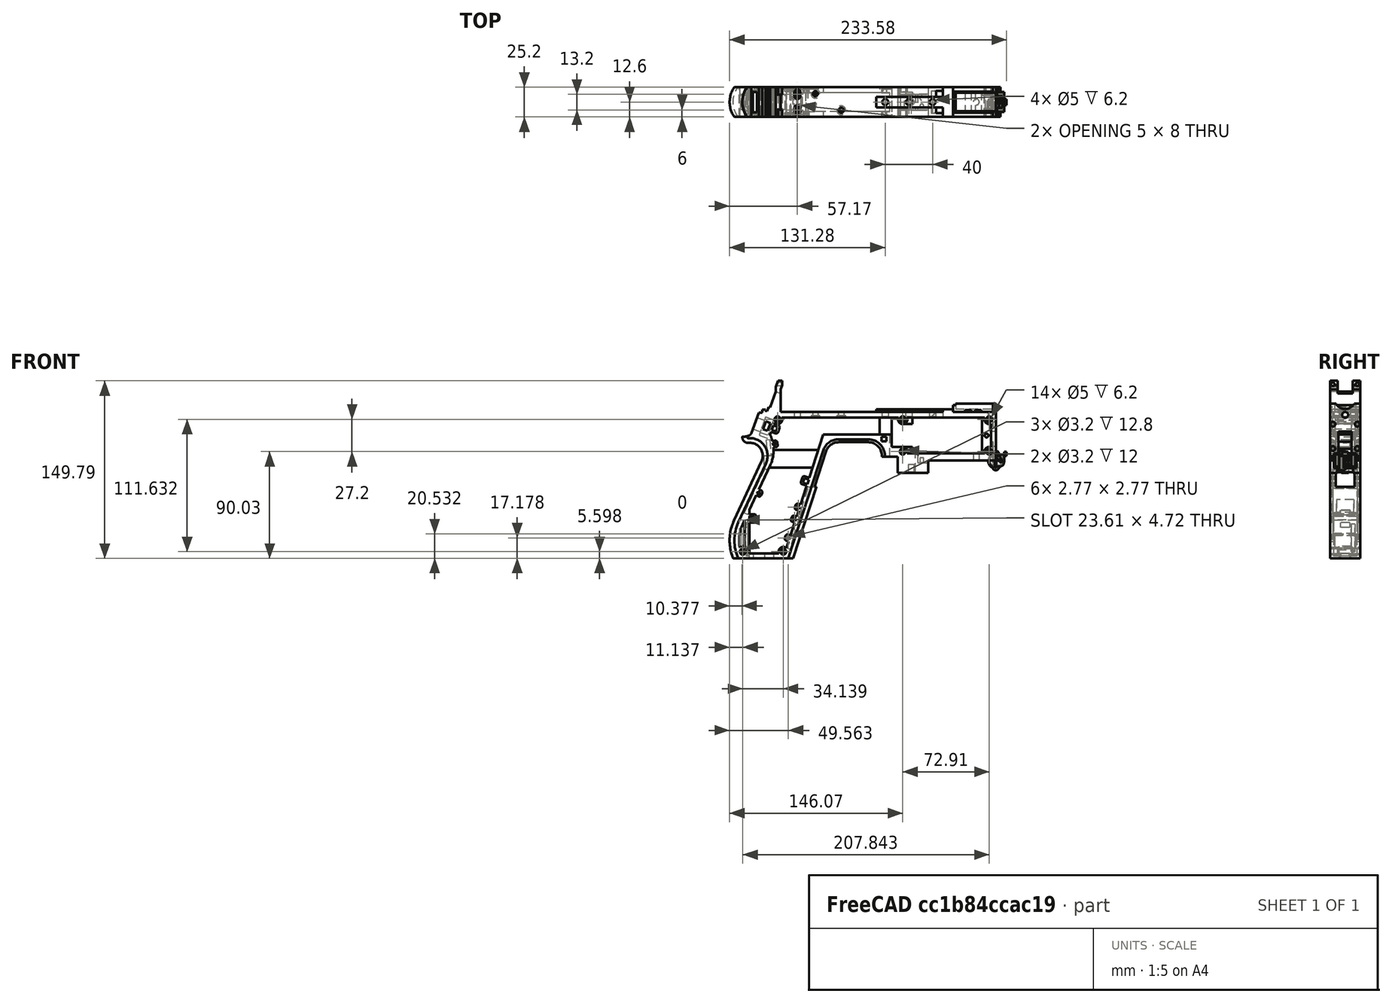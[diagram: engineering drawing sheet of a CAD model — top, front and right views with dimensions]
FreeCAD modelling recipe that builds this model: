
FCSTD DOCUMENT  (FreeCAD 1.0R39319 (Git))
Label: PICON-OF_ver_44
License: All rights reserved
LicenseURL: https://en.wikipedia.org/wiki/All_rights_reserved
objects: Sketcher::SketchObject×114, Part::Extrusion×57, Part::Cut×43, PartDesign::Pad×29, PartDesign::Pocket×18, PartDesign::Chamfer×15, PartDesign::Body×10, PartDesign::Fillet×6, Part::MultiFuse×4, PartDesign::SubtractivePipe×4, Part::Part2DObjectPython×4, PartDesign::SubtractiveLoft×4, PartDesign::Plane×2, PartDesign::SubShapeBinder×2, Part::Sweep×1, PartDesign::ShapeBinder×1, Mesh::Feature×1
note: 580 computed .brp shape members not serialized (recipe doc carries the construction recipe); baked Part::Feature solids carry a one-line shape summary decoded from their .brp

FEATURE [Sketcher::SketchObject] Sketch  label="corpo principale"
  ArcFitTolerance = 1e-06
  AttacherType = Attacher::AttachEngine3D
  AttachmentSupport = -> [XZ_Plane]
  FullyConstrained = true
  MakeInternals = false
  MapMode = 5
  Placement = pos=(0,0,0) rot=(1,0,0;1.5708rad)
  sketch-geometry (65):
    g0: LineSegment StartX=0 StartY=0 StartZ=0 EndX=-57.2 EndY=0 EndZ=0
    g1: LineSegment StartX=-57.2 StartY=0 StartZ=0 EndX=-57.2 EndY=-10.4 EndZ=0
    g2: LineSegment StartX=-57.2 StartY=-10.4 StartZ=0 EndX=-82.8 EndY=-10.4 EndZ=0
    g3: LineSegment StartX=-82.8 StartY=-10.4 StartZ=0 EndX=-82.8 EndY=3.2 EndZ=0
    g4: LineSegment StartX=-82.8 StartY=3.2 StartZ=0 EndX=-93.6 EndY=3.2 EndZ=0
    g5: LineSegment StartX=-93.6 StartY=3.2 StartZ=0 EndX=-93.6 EndY=4 EndZ=0
    g6: LineSegment StartX=-107.6 StartY=18 StartZ=0 EndX=-132.428 EndY=18 EndZ=0
    g7: LineSegment StartX=-145.743 StartY=8.32624 StartZ=0 EndX=-175.232 EndY=-82.4316 EndZ=0
    g8: LineSegment StartX=-175.232 StartY=-82.4316 StartZ=0 EndX=-217.232 EndY=-82.4316 EndZ=0
    g9: LineSegment StartX=-217.232 StartY=-52.1862 StartZ=0 EndX=-193.988 EndY=-2.33927 EndZ=0
    g10: LineSegment StartX=-206.196 StartY=23.0857 StartZ=0 EndX=-199.861 EndY=40.4914 EndZ=0
    g11: LineSegment StartX=-199.861 StartY=40.4914 StartZ=0 EndX=-197.061 EndY=40.4914 EndZ=0
    g12: LineSegment StartX=-197.061 StartY=40.4914 StartZ=0 EndX=-197.061 EndY=42.8914 EndZ=0
    g13: LineSegment StartX=-197.061 StartY=42.8914 StartZ=0 EndX=-194.261 EndY=42.8914 EndZ=0
    g14: LineSegment StartX=-194.261 StartY=42.8914 StartZ=0 EndX=-194.535 EndY=42.1397 EndZ=0
    g15: LineSegment StartX=-194.535 StartY=42.1397 StartZ=0 EndX=-193.031 EndY=41.5924 EndZ=0
    g16: LineSegment StartX=-193.031 StartY=41.5924 StartZ=0 EndX=-191.663 EndY=45.3512 EndZ=0
    g17: LineSegment StartX=-191.663 StartY=45.3512 StartZ=0 EndX=-190.536 EndY=44.9408 EndZ=0
    g18: LineSegment StartX=-190.536 StartY=44.9408 StartZ=0 EndX=-185.747 EndY=58.0965 EndZ=0
    g19: LineSegment StartX=-185.747 StartY=58.0965 StartZ=0 EndX=-185.747 EndY=62.0965 EndZ=0
    g20: LineSegment StartX=-185.747 StartY=62.0965 StartZ=0 EndX=-183.832 EndY=67.3588 EndZ=0
    g21: LineSegment StartX=-183.832 StartY=67.3588 StartZ=0 EndX=-180.232 EndY=67.3588 EndZ=0
    g22: LineSegment StartX=-180.232 StartY=67.3588 StartZ=0 EndX=-180.232 EndY=63.7588 EndZ=0
    g23: LineSegment StartX=-180.232 StartY=63.7588 StartZ=0 EndX=-181.6 EndY=60 EndZ=0
    g24: LineSegment StartX=-181.6 StartY=60 StartZ=0 EndX=-181.6 EndY=41.2 EndZ=0
    g25: LineSegment StartX=-181.6 StartY=41.2 StartZ=0 EndX=-100.8 EndY=41.2 EndZ=0
    g26: LineSegment StartX=-36 StartY=43.2 StartZ=0 EndX=-36 EndY=41.2 EndZ=0
    g27: LineSegment StartX=0 StartY=48 StartZ=0 EndX=0 EndY=0 EndZ=0
    g28: LineSegment StartX=-209.901 StartY=19.85 StartZ=0 EndX=-209.901 EndY=20.1 EndZ=0
    g29: LineSegment StartX=-208.001 StartY=22 StartZ=0 EndX=-207.747 EndY=22 EndZ=0
    g30: LineSegment StartX=-207.583 StartY=19 StartZ=0 EndX=-209.051 EndY=19 EndZ=0
    g31: ArcOfCircle CenterX=-208.001 CenterY=20.1 CenterZ=0 NormalX=0 NormalY=0 NormalZ=1 AngleXU=0 Radius=1.9 StartAngle=1.5708 EndAngle=3.14159
    g32: GeomPoint [constr] X=-209.901 Y=22 Z=0
    g33: ArcOfCircle CenterX=-209.051 CenterY=19.85 CenterZ=0 NormalX=0 NormalY=0 NormalZ=1 AngleXU=0 Radius=0.85 StartAngle=3.14159 EndAngle=4.71239
    g34: GeomPoint [constr] X=-209.901 Y=19 Z=0
    g35: ArcOfCircle CenterX=-207.747 CenterY=23.65 CenterZ=0 NormalX=0 NormalY=0 NormalZ=1 AngleXU=0 Radius=1.65 StartAngle=4.71239 EndAngle=5.93412
    g36: GeomPoint [constr] X=-206.591 Y=22 Z=0
    g37: LineSegment StartX=-4 StartY=6 StartZ=0 EndX=-4 EndY=36.4 EndZ=0
    g38: LineSegment StartX=-4 StartY=36.4 StartZ=0 EndX=-185.2 EndY=36.4 EndZ=0
    g39: LineSegment StartX=-185.2 StartY=36.4 StartZ=0 EndX=-190.441 EndY=22 EndZ=0
    g40: LineSegment StartX=-214.575 StartY=-78.4316 StartZ=0 EndX=-178.142 EndY=-78.4316 EndZ=0
    g41: LineSegment StartX=-178.142 StartY=-78.4316 StartZ=0 EndX=-145.51 EndY=22 EndZ=0
    g42: LineSegment StartX=-145.51 StartY=22 StartZ=0 EndX=-87.91 EndY=22 EndZ=0
    g43: LineSegment StartX=-87.91 StartY=22 StartZ=0 EndX=-87.91 EndY=11.6 EndZ=0
    g44: LineSegment StartX=-87.91 StartY=11.6 StartZ=0 EndX=-80.11 EndY=11.6 EndZ=0
    g45: LineSegment StartX=-80.11 StartY=11.6 StartZ=0 EndX=-80.11 EndY=6 EndZ=0
    g46: LineSegment StartX=-80.11 StartY=6 StartZ=0 EndX=-4 EndY=6 EndZ=0
    g47: LineSegment StartX=-190.363 StartY=-4.02975 StartZ=0 EndX=-213.607 EndY=-53.8767 EndZ=0
    g48: ArcOfCircle CenterX=-132.428 CenterY=4 CenterZ=0 NormalX=0 NormalY=0 NormalZ=1 AngleXU=0 Radius=14 StartAngle=1.5708 EndAngle=2.82743
    g49: GeomPoint [constr] X=-142.6 Y=18 Z=0
    g50: ArcOfCircle CenterX=-107.6 CenterY=4 CenterZ=0 NormalX=0 NormalY=0 NormalZ=1 AngleXU=0 Radius=14 StartAngle=0 EndAngle=1.5708
    g51: GeomPoint [constr] X=-93.6 Y=18 Z=0
    g52: ArcOfCircle CenterX=-184.801 CenterY=-67.3089 CenterZ=0 NormalX=0 NormalY=0 NormalZ=1 AngleXU=0 Radius=35.7833 StartAngle=2.70526 EndAngle=3.57792
    g53: ArcOfCircle CenterX=-207.583 CenterY=4 CenterZ=0 NormalX=0 NormalY=0 NormalZ=1 AngleXU=0 Radius=15 StartAngle=5.84685 EndAngle=7.85398
    g54: LineSegment [constr] StartX=-213.607 StartY=-53.8767 StartZ=0 EndX=-217.232 EndY=-52.1862 EndZ=0
    g55: ArcOfCircle CenterX=-184.801 CenterY=-67.3089 CenterZ=0 NormalX=0 NormalY=0 NormalZ=1 AngleXU=0 Radius=31.7833 StartAngle=2.70526 EndAngle=3.49911
    g56: ArcOfCircle CenterX=-218.095 CenterY=8.90192 CenterZ=0 NormalX=0 NormalY=0 NormalZ=1 AngleXU=0 Radius=30.5989 StartAngle=5.84685 EndAngle=6.72553
    g57: LineSegment StartX=-44.6 StartY=43.2 StartZ=0 EndX=-36 EndY=43.2 EndZ=0
    g58: LineSegment StartX=-100.8 StartY=41.2 StartZ=0 EndX=-44.6 EndY=41.2 EndZ=0
    g59: LineSegment StartX=-44.6 StartY=41.2 StartZ=0 EndX=-44.6 EndY=43.2 EndZ=0
    g60: LineSegment StartX=-2.4 StartY=48 StartZ=0 EndX=0 EndY=48 EndZ=0
    g61: LineSegment StartX=-36 StartY=41.2 StartZ=0 EndX=-2.4 EndY=41.2 EndZ=0
    g62: LineSegment StartX=-2.4 StartY=41.2 StartZ=0 EndX=-2.4 EndY=48 EndZ=0
    g63: LineSegment [constr] StartX=-181.6 StartY=36.4 StartZ=0 EndX=-152.209 EndY=36.4 EndZ=0
    g64: LineSegment [constr] StartX=-181.6 StartY=36.4 StartZ=0 EndX=-130.41 EndY=36.4 EndZ=0
  constraints (183):
    c: Coincident(g-1,g0)
    c: PointOnObject(g0,g-1)
    c: Coincident(g0,g1)
    c: Vertical(g1)
    c: Coincident(g1,g2)
    c: Horizontal(g2)
    c: Coincident(g2,g3)
    c: Vertical(g3)
    c: Coincident(g3,g4)
    c: Coincident(g4,g5)
    c: Vertical(g5)
    c: Horizontal(g6)
    c: Coincident(g7,g8)
    c: Horizontal(g8)
    c: Coincident(g10,g11)
    c: Horizontal(g11)
    c: Coincident(g11,g12)
    c: Vertical(g12)
    c: Coincident(g12,g13)
    c: Horizontal(g13)
    c: Coincident(g13,g14)
    c: Coincident(g14,g15)
    c: Coincident(g15,g16)
    c: Coincident(g16,g17)
    c: Coincident(g17,g18)
    c: Coincident(g18,g19)
    c: Vertical(g19)
    c: Coincident(g19,g20)
    c: Coincident(g20,g21)
    c: Horizontal(g21)
    c: Coincident(g21,g22)
    c: Vertical(g22)
    c: Coincident(g22,g23)
    c: Coincident(g23,g24)
    c: Vertical(g24)
    c: Coincident(g24,g25)
    c: Horizontal(g25)
    c: Coincident(g57,g26)
    c: Vertical(g26)
    c: Coincident(g26,g61)
    c: PointOnObject(g60,g-2)
    c: Coincident(g60,g27)
    c: Coincident(g27,g0)
    c: DistanceY(g27,g27) = 48
    c: DistanceY(g1,g1) = 10.4
    c: DistanceX(g0,g0) = 57.2
    c: DistanceX(g2,g2) = 25.6
    c: Horizontal(g4)
    c: DistanceY(g3,g3) = 13.6
    c: DistanceX(g4,g4) = 10.8
    c: DistanceY(g5,g51) = 14.8
    c: DistanceX(g49,g51) = 49
    c: Distance(g7,g49) = 105.6
    c: DistanceX(g61,g60) = 36
    c: DistanceX(g25,g25) = 80.8
    c: DistanceY(g24,g24) = 18.8
    c: DistanceY(g22,g22) = 3.6
    c: Distance(g23) = 4
    c: Angle(g-1,g23) = 1.22173
    c: DistanceX(g21,g21) = 3.6
    c: Distance(g20) = 5.6
    c: Angle(g-1,g20) = 1.22173
    c: DistanceY(g19,g19) = 4
    c: Distance(g18) = 14
    c: Angle(g-1,g18) = 1.22173
    c: Distance(g17) = 1.2
    c: Distance(g16) = 4
    c: Angle(g16) = 1.22173
    c: Perpendicular(g18,g17)
    c: Distance(g15) = 1.6
    c: Perpendicular(g16,g15)
    c: Distance(g14) = 0.8
    c: DistanceX(g13,g13) = 2.8
    c: Perpendicular(g15,g14)
    c: DistanceY(g12,g12) = 2.4
    c: DistanceX(g11,g11) = 2.8
    c: Distance(g9) = 55
    c: Angle(g9,g-1) = 2.00713
    c: Horizontal(g29)
    c: Vertical(g28)
    c: Horizontal(g30)
    c: PointOnObject(g32,g29)
    c: PointOnObject(g32,g28)
    c: Tangent(g29,g31) = 1.5708
    c: Tangent(g28,g31) = 1.5708
    c: PointOnObject(g34,g28)
    c: PointOnObject(g34,g30)
    c: Tangent(g28,g33) = 1.5708
    c: Tangent(g30,g33) = 1.5708
    c: PointOnObject(g36,g29)
    c: PointOnObject(g36,g10)
    c: Tangent(g29,g35) = -1.5708
    c: Tangent(g10,g35) = -1.5708
    c: Angle(g-1,g10) = 1.22173
    c: Radius(g35) = 1.65
    c: Vertical(g37)
    c: Coincident(g37,g38)
    c: Horizontal(g38)
    c: Coincident(g38,g39)
    c: Horizontal(g40)
    c: Coincident(g40,g41)
    c: Coincident(g41,g42)
    c: Horizontal(g42)
    c: Coincident(g42,g43)
    c: Vertical(g43)
    c: Coincident(g43,g44)
    c: Horizontal(g44)
    c: Coincident(g44,g45)
    c: Vertical(g45)
    c: Coincident(g45,g46)
    c: Coincident(g46,g37)
    c: Horizontal(g46)
    c: DistanceY(g0,g37) = 6
    c: DistanceX(g37,g0) = 4
    c: DistanceY(g37,g25) = 4.8
    c: DistanceX(g38,g38) = 181.2
    c: DistanceX(g42,g42) = 57.6
    c: DistanceY(g49,g41) = 4
    c: DistanceX(g41,g49) = 2.91
    c: DistanceY(g43,g43) = 10.4
    c: DistanceX(g44,g44) = 7.8
    c: DistanceY(g7,g40) = 4
    c: Distance(g47) = 55
    c: Angle(g-1,g39) = 1.22173
    c: PointOnObject(g49,g7)
    c: PointOnObject(g49,g6)
    c: Tangent(g7,g48) = -1.5708
    c: Tangent(g6,g48) = -1.5708
    c: PointOnObject(g51,g5)
    c: PointOnObject(g51,g6)
    c: Tangent(g5,g50) = -1.5708
    c: Tangent(g6,g50) = -1.5708
    c: Radius(g50) = 14
    c: Radius(g48) = 14
    c: DistanceX(g8,g8) = 42
    c: Angle(g7,g-1) = 1.88496
    c: Parallel(g41,g7)
    c: Parallel(g47,g9)
    c: Coincident(g52,g8)
    c: Tangent(g52,g9) = 1.5708
    c: DistanceX(g9,g8) = 0
    c: Tangent(g53,g9) = -1.5708
    c: Tangent(g53,g30) = -1.5708
    c: Diameter(g53) = 30
    c: DistanceY(g53,g0) = -4
    c: Coincident(g54,g47)
    c: Distance(g54) = 4
    c: Coincident(g54,g9)
    c: Coincident(g55,g40)
    c: Tangent(g55,g47) = -1.5708
    c: Coincident(g52,g55)
    c: Coincident(g56,g39)
    c: Tangent(g56,g47) = 1.5708
    c: Horizontal(g57)
    c: DistanceX(g57,g57) = 8.6
    c: Coincident(g58,g25)
    c: Horizontal(g58)
    c: Coincident(g59,g58)
    c: Vertical(g59)
    c: DistanceY(g58,g57) = 2
    c: DistanceX(g58,g58) = 56.2
    c: Coincident(g59,g57)
    c: DistanceY(g41,g36) = 0
    c: DistanceY(g36,g39) = 0
    c: DistanceY(g28,g28) = 0.25
    c: DistanceX(g30,g36) = 2.46
    c: DistanceX(g28,g29) = 1.9
    c: Coincident(g62,g60)
    c: Horizontal(g60)
    c: DistanceX(g62,g27) = 2.4
    c: Coincident(g61,g62)
    c: DistanceY(g26,g26) = 2
    c: Vertical(g62)
    c: DistanceY(g61,g60) = 6.8
    c: Horizontal(g61)
    c: Distance(g63) = 29.391
    c: PointOnObject(g63,g38)
    c: PointOnObject(g63,g38)
    c: Distance(g64) = 51.19
    c: PointOnObject(g64,g38)
    c: PointOnObject(g64,g38)
    c: DistanceX(g24,g63) = 0
    c: DistanceX(g24,g64) = 0
FEATURE [Part::Extrusion] Extrude  label="Extrude corpo principale"
  Base = -> Sketch
  Dir = (0,-1,2e-16)
  DirMode = 2
  FaceMakerClass = Part::FaceMakerBullseye
  FaceMakerMode = 3
  LengthFwd = 25.2
  LengthRev = 12.6
  Solid = true
  Symmetric = true
FEATURE [Sketcher::SketchObject] Sketch002  label="scavo grilletto"
  ArcFitTolerance = 1e-06
  AttachmentSupport = -> [XZ_Plane]
  ExternalGeometry = -> [Sketch]
  FullyConstrained = true
  MakeInternals = false
  MapMode = 5
  Placement = pos=(0,0,0) rot=(1,0,0;1.5708rad)
  sketch-geometry (4):
    g0: LineSegment StartX=-89.51 StartY=22 StartZ=0 EndX=-152.71 EndY=22 EndZ=0
    g1: LineSegment StartX=-152.71 StartY=22 StartZ=0 EndX=-167.006 EndY=-22 EndZ=0
    g2: LineSegment StartX=-167.006 StartY=-22 StartZ=0 EndX=-89.51 EndY=-22 EndZ=0
    g3: LineSegment StartX=-89.51 StartY=-22 StartZ=0 EndX=-89.51 EndY=22 EndZ=0
  constraints (12):
    c: Horizontal(g0)
    c: Coincident(g0,g1)
    c: Coincident(g1,g2)
    c: Horizontal(g2)
    c: Coincident(g2,g3)
    c: Coincident(g3,g0)
    c: Vertical(g3)
    c: Angle(g1,g0) = 1.88496
    c: DistanceY(g3,g3) = 44
    c: DistanceX(g0,g0) = 63.2
    c: DistanceX(g0,g-3) = 1.6
    c: DistanceY(g-3,g0) = 0
FEATURE [Sketcher::SketchObject] Sketch004  label="traiettoria arrotondamento impugnatura anteriore"
  ArcFitTolerance = 1e-06
  AttachmentSupport = -> [XZ_Plane]
  ExternalGeometry = -> [Sketch]
  FullyConstrained = true
  MakeInternals = false
  MapMode = 5
  Placement = pos=(0,0,0) rot=(1,0,0;1.5708rad)
  sketch-geometry (13):
    g0: LineSegment StartX=-175.232 StartY=-82.4316 StartZ=0 EndX=-145.743 EndY=8.32624 EndZ=0
    g1: LineSegment StartX=-93.6 StartY=3.2 StartZ=0 EndX=-93.6 EndY=4 EndZ=0
    g2: LineSegment StartX=-132.428 StartY=18 StartZ=0 EndX=-107.6 EndY=18 EndZ=0
    g3: ArcOfCircle CenterX=-132.428 CenterY=4 CenterZ=0 NormalX=0 NormalY=0 NormalZ=1 AngleXU=0 Radius=14 StartAngle=1.5708 EndAngle=2.82743
    g4: ArcOfCircle CenterX=-107.6 CenterY=4 CenterZ=0 NormalX=0 NormalY=0 NormalZ=1 AngleXU=0 Radius=14 StartAngle=0 EndAngle=1.5708
    g5: LineSegment StartX=-175.232 StartY=-82.4316 StartZ=0 EndX=-217.232 EndY=-82.4316 EndZ=0
    g6: LineSegment StartX=-217.232 StartY=-52.1862 StartZ=0 EndX=-193.988 EndY=-2.33927 EndZ=0
    g7: LineSegment StartX=-209.051 StartY=19 StartZ=0 EndX=-207.583 EndY=19 EndZ=0
    g8: LineSegment StartX=-209.901 StartY=20.1 StartZ=0 EndX=-209.901 EndY=19.85 EndZ=0
    g9: ArcOfCircle CenterX=-184.801 CenterY=-67.3089 CenterZ=0 NormalX=0 NormalY=0 NormalZ=1 AngleXU=0 Radius=35.7833 StartAngle=2.70526 EndAngle=3.57792
    g10: ArcOfCircle CenterX=-207.583 CenterY=4 CenterZ=0 NormalX=0 NormalY=0 NormalZ=1 AngleXU=0 Radius=15 StartAngle=5.84685 EndAngle=7.85398
    g11: ArcOfCircle CenterX=-209.051 CenterY=19.85 CenterZ=0 NormalX=0 NormalY=0 NormalZ=1 AngleXU=0 Radius=0.85 StartAngle=3.14159 EndAngle=4.71239
    g12: ArcOfCircle CenterX=-208.001 CenterY=20.1 CenterZ=0 NormalX=0 NormalY=0 NormalZ=1 AngleXU=0 Radius=1.9 StartAngle=1.5708 EndAngle=3.14159
  constraints (26):
    c: Coincident(g0,g-3)
    c: Coincident(g0,g-6)
    c: Coincident(g1,g-8)
    c: Coincident(g1,g-7)
    c: Coincident(g2,g-5)
    c: Coincident(g2,g-4)
    c: Coincident(g3,g2)
    c: Tangent(g3,g0) = 1.5708
    c: Coincident(g4,g1)
    c: Tangent(g4,g2) = 1.5708
    c: Coincident(g5,g0)
    c: Coincident(g5,g-9)
    c: Coincident(g6,g-12)
    c: Coincident(g6,g-11)
    c: Coincident(g7,g-15)
    c: Coincident(g7,g-14)
    c: Coincident(g8,g-16)
    c: Coincident(g8,g-17)
    c: Tangent(g9,g6) = 1.5708
    c: Coincident(g9,g5)
    c: Coincident(g10,g7)
    c: Tangent(g10,g6) = -1.5708
    c: Tangent(g11,g7) = -1.5708
    c: Coincident(g11,g8)
    c: Tangent(g12,g8) = -1.5708
    c: Coincident(g12,g-17)
FEATURE [PartDesign::Plane] DatumPlane  label="Piano per disegno arrotondamento impugnatura"
  AttachmentSupport = -> [Sketch]
  Length = 73.6581
  MapMode = 7
  Placement = pos=(-145.743,1.8e-15,8.32624) rot=(0.154555,0.154555,0.97582;1.59527rad)
  ResizeMode = 0
  Width = 303.511
FEATURE [Sketcher::SketchObject] Sketch005  label="forma arrotondamento impugnatura anteriore"
  ArcFitTolerance = 1e-06
  AttachmentSupport = -> [DatumPlane]
  FullyConstrained = true
  MakeInternals = false
  MapMode = 5
  Placement = pos=(-145.743,1.8e-15,8.32624) rot=(0.154555,0.154555,0.97582;1.59527rad)
  sketch-geometry (5):
    g0: GeomPoint [constr] X=0 Y=-4 Z=0
    g1: GeomPoint [constr] X=-12.6 Y=7.1e-15 Z=0
    g2: GeomPoint [constr] X=12.6 Y=4.97e-14 Z=0
    g3: LineSegment StartX=-12.6 StartY=7.1e-15 StartZ=0 EndX=12.6 EndY=4.97e-14 EndZ=0
    g4: ArcOfCircle CenterX=-3.88e-14 CenterY=17.845 CenterZ=0 NormalX=0 NormalY=0 NormalZ=1 AngleXU=0 Radius=21.845 StartAngle=4.09759 EndAngle=5.32718
  constraints (11):
    c: DistanceY(g0,g-1) = 4
    c: DistanceX(g-1,g0) = 0
    c: DistanceX(g1,g-1) = 12.6
    c: DistanceX(g-1,g2) = 12.6
    c: DistanceY(g-1,g2) = 0
    c: DistanceY(g-1,g1) = 0
    c: Coincident(g3,g1)
    c: Coincident(g3,g2)
    c: Coincident(g4,g1)
    c: Coincident(g4,g2)
    c: PointOnObject(g0,g4)
FEATURE [Part::Sweep] Sweep  label="Sweep impugnatura"
  Frenet = true
  Sections = -> [Sketch005]
  Solid = true
  Spine = -> Sketch [Edge32,Edge33,Edge34,Edge35,Edge36,Edge37,Edge38,Edge39,Edge40,Edge41,Edge42,Edge43,Edge44]
  Transition = 1
FEATURE [Sketcher::SketchObject] Sketch008  label="buchi e pulizie varie"
  ArcFitTolerance = 1e-06
  AttachmentSupport = -> [XZ_Plane]
  ExternalGeometry = -> [Sketch]
  FullyConstrained = true
  MakeInternals = false
  MapMode = 5
  Placement = pos=(0,0,0) rot=(1,0,0;1.5708rad)
  sketch-geometry (26):
    g0: LineSegment StartX=-96.278 StartY=20.155 StartZ=0 EndX=-92.278 EndY=20.155 EndZ=0
    g1: LineSegment StartX=-92.278 StartY=20.155 StartZ=0 EndX=-92.278 EndY=16.155 EndZ=0
    g2: LineSegment StartX=-92.278 StartY=16.155 StartZ=0 EndX=-96.278 EndY=16.155 EndZ=0
    g3: LineSegment StartX=-96.278 StartY=16.155 StartZ=0 EndX=-96.278 EndY=20.155 EndZ=0
    g4: LineSegment StartX=-222.232 StartY=-82.4316 StartZ=0 EndX=-170.232 EndY=-82.4316 EndZ=0
    g5: LineSegment StartX=-170.232 StartY=-82.4316 StartZ=0 EndX=-170.232 EndY=-86.4316 EndZ=0
    g6: LineSegment StartX=-170.232 StartY=-86.4316 StartZ=0 EndX=-222.232 EndY=-86.4316 EndZ=0
    g7: LineSegment StartX=-222.232 StartY=-86.4316 StartZ=0 EndX=-222.232 EndY=-82.4316 EndZ=0
    g8: LineSegment StartX=-213.901 StartY=20.1 StartZ=0 EndX=-213.901 EndY=26 EndZ=0
    g9: LineSegment StartX=-213.901 StartY=26 StartZ=0 EndX=-206.196 EndY=26 EndZ=0
    g10: LineSegment StartX=-17.4 StartY=42.8 StartZ=0 EndX=-12.4 EndY=42.8 EndZ=0
    g11: LineSegment StartX=-12.4 StartY=42.8 StartZ=0 EndX=-12.4 EndY=41.2 EndZ=0
    g12: LineSegment StartX=-12.4 StartY=41.2 StartZ=0 EndX=-17.4 EndY=41.2 EndZ=0
    g13: LineSegment StartX=-17.4 StartY=41.2 StartZ=0 EndX=-17.4 EndY=42.8 EndZ=0
    g14: LineSegment StartX=-25.9 StartY=42.8 StartZ=0 EndX=-20.9 EndY=42.8 EndZ=0
    g15: LineSegment StartX=-20.9 StartY=42.8 StartZ=0 EndX=-20.9 EndY=41.2 EndZ=0
    g16: LineSegment StartX=-20.9 StartY=41.2 StartZ=0 EndX=-25.9 EndY=41.2 EndZ=0
    g17: LineSegment StartX=-25.9 StartY=41.2 StartZ=0 EndX=-25.9 EndY=42.8 EndZ=0
    g18: GeomPoint [constr] X=-206.196 Y=23.0857 Z=0
    g19: GeomPoint [constr] X=-213.901 Y=20.1 Z=0
    g20: BSplineCurve PolesCount=4 KnotsCount=2 Degree=3 IsPeriodic=0
    g21-g24: Circle [constr] x4 (B-spline internal-alignment scaffolding for g20; pole/knot coordinates omitted)
    g25: LineSegment StartX=-206.196 StartY=26 StartZ=0 EndX=-206.196 EndY=23.0857 EndZ=0
  constraints (73):
    c: Horizontal(g0)
    c: Coincident(g1,g0)
    c: Vertical(g1)
    c: Coincident(g2,g1)
    c: Horizontal(g2)
    c: Coincident(g3,g2)
    c: Coincident(g3,g0)
    c: Vertical(g3)
    c: DistanceX(g0,g-4) = 4.368
    c: DistanceY(g0,g-4) = 1.845
    c: DistanceY(g1,g1) = 4
    c: DistanceX(g2,g2) = 4
    c: Horizontal(g4)
    c: Coincident(g5,g4)
    c: Vertical(g5)
    c: Coincident(g6,g5)
    c: Horizontal(g6)
    c: Coincident(g7,g6)
    c: Coincident(g7,g4)
    c: Vertical(g7)
    c: DistanceY(g7,g7) = 4
    c: DistanceX(g4,g-5) = 5
    c: DistanceX(g-5,g4) = 5
    c: DistanceY(g4,g-5) = 0
    c: Coincident(g9,g8)
    c: Parallel(g9,g-6)
    c: DistanceX(g8,g-8) = 4
    c: Horizontal(g10)
    c: Coincident(g11,g10)
    c: Vertical(g11)
    c: Coincident(g12,g11)
    c: Horizontal(g12)
    c: Coincident(g13,g12)
    c: Coincident(g13,g10)
    c: Vertical(g13)
    c: Horizontal(g14)
    c: Coincident(g15,g14)
    c: Vertical(g15)
    c: Coincident(g16,g15)
    c: Horizontal(g16)
    c: Coincident(g17,g16)
    c: Coincident(g17,g14)
    c: Vertical(g17)
    c: DistanceY(g11,g10) = 1.6
    c: DistanceX(g10,g10) = 5
    c: DistanceY(g15,g14) = 1.6
    c: DistanceX(g14,g14) = 5
    c: DistanceX(g15,g12) = 3.5
    c: DistanceX(g11,g-9) = 10
    c: DistanceY(g-9,g11) = 0
    c: DistanceY(g-9,g15) = 0
    c: Perpendicular(g8,g9)
    c: DistanceY(g-7,g9) = 4
    c: DistanceY(g8,g-8) = 0
    c: InternalAlignment(g18,g20)
    c: InternalAlignment(g19,g20)
    c: InternalAlignment(g21,g20)
    c: Weight(g21) = 1
    c: InternalAlignment(g22,g20)
    c: Equal(g22,g21)
    c: InternalAlignment(g23,g20)
    c: Equal(g23,g21)
    c: InternalAlignment(g24,g20)
    c: Equal(g24,g21)
    c: Coincident(g18,g-12)
    c: Coincident(g19,g8)
    c: Coincident(g25,g9)
    c: Coincident(g25,g20)
    c: Vertical(g25)
    c: DistanceY(g20,g23) = 0
    c: DistanceY(g22,g18) = 2.26
    c: DistanceX(g22,g18) = 0.93
    c: DistanceX(g20,g23) = 2.9
FEATURE [Part::Extrusion] Extrude004  label="Extrude Buchi e pulizie varie"
  Base = -> Sketch008
  Dir = (0,-1,2e-16)
  DirMode = 2
  FaceMakerClass = Part::FaceMakerBullseye
  FaceMakerMode = 3
  LengthFwd = 25.2
  LengthRev = 0
  Solid = true
  Symmetric = true
FEATURE [Sketcher::SketchObject] Sketch009  label="rinforzi"
  ArcFitTolerance = 1e-06
  AttachmentSupport = -> [XZ_Plane]
  ExternalGeometry = -> [Sketch]
  FullyConstrained = true
  MakeInternals = false
  MapMode = 5
  Placement = pos=(0,0,0) rot=(1,0,0;1.5708rad)
  sketch-geometry (9):
    g0: LineSegment StartX=-87.91 StartY=22 StartZ=0 EndX=-87.91 EndY=36.4 EndZ=0
    g1: LineSegment StartX=-87.91 StartY=36.4 StartZ=0 EndX=-97.91 EndY=36.4 EndZ=0
    g2: LineSegment StartX=-97.91 StartY=36.4 StartZ=0 EndX=-97.91 EndY=22 EndZ=0
    g3: LineSegment StartX=-97.91 StartY=22 StartZ=0 EndX=-87.91 EndY=22 EndZ=0
    g4: LineSegment StartX=-149.713 StartY=9.06563 StartZ=0 EndX=-154.586 EndY=-5.93437 EndZ=0
    g5: LineSegment StartX=-154.586 StartY=-5.93437 StartZ=0 EndX=-191.863 EndY=-5.93437 EndZ=0
    g6: LineSegment StartX=-191.863 StartY=-5.93437 StartZ=0 EndX=-191.863 EndY=9.06563 EndZ=0
    g7: LineSegment StartX=-191.863 StartY=9.06563 StartZ=0 EndX=-149.713 EndY=9.06563 EndZ=0
    g8: LineSegment [constr] StartX=-145.51 StartY=22 StartZ=0 EndX=-149.713 EndY=9.06563 EndZ=0
  constraints (25):
    c: Vertical(g0)
    c: Coincident(g1,g0)
    c: Horizontal(g1)
    c: Coincident(g2,g1)
    c: Vertical(g2)
    c: Coincident(g3,g2)
    c: Coincident(g3,g0)
    c: Horizontal(g3)
    c: Coincident(g0,g-4)
    c: DistanceX(g3,g3) = 10
    c: DistanceY(g0,g-3) = 0
    c: Coincident(g5,g4)
    c: Horizontal(g5)
    c: Coincident(g6,g5)
    c: Vertical(g6)
    c: Coincident(g7,g6)
    c: Coincident(g7,g4)
    c: Horizontal(g7)
    c: Distance(g8) = 13.6
    c: Parallel(g-6,g8)
    c: Coincident(g-6,g8)
    c: Parallel(g4,g-6)
    c: DistanceY(g4,g4) = 15
    c: Coincident(g4,g8)
    c: DistanceX(g-5,g5) = -1.5
FEATURE [Part::Extrusion] Extrude001  label="Extrude scavo grilletto"
  Base = -> Sketch002
  Dir = (0,-1,2e-16)
  DirMode = 2
  FaceMakerClass = Part::FaceMakerBullseye
  FaceMakerMode = 3
  LengthFwd = 16
  LengthRev = 0
  Solid = true
  Symmetric = true
FEATURE [Part::Extrusion] Extrude005  label="Extrude Rinforzi"
  Base = -> Sketch009
  Dir = (0,-1,2e-16)
  DirMode = 2
  FaceMakerClass = Part::FaceMakerBullseye
  FaceMakerMode = 3
  LengthFwd = 2
  LengthRev = 0
  Placement = pos=(0,12.6,0) rot=(0,0,1;0rad)
  Solid = true
  Symmetric = false
FEATURE [PartDesign::ShapeBinder] CopyCut
  TraceSupport = false
FEATURE [PartDesign::Plane] DatumPlane001
  AttachmentSupport = -> [CopyCut]
  Length = 283.944
  MapMode = 5
  Placement = pos=(0,12.6,0) rot=(0,0.707107,0.707107;3.14159rad)
  ResizeMode = 0
  Width = 188.15
FEATURE [Sketcher::SketchObject] Sketch010  label="buco neopixel"
  ArcFitTolerance = 1e-06
  AttachmentSupport = -> [XZ_Plane]
  ExternalGeometry = -> [Sketch]
  FullyConstrained = true
  MakeInternals = false
  MapMode = 5
  Placement = pos=(0,0,0) rot=(1,0,0;1.5708rad)
  sketch-geometry (5):
    g0: LineSegment [constr] StartX=-199.861 StartY=40.4914 StartZ=0 EndX=-201.368 EndY=36.3521 EndZ=0
    g1: LineSegment StartX=-201.368 StartY=36.3521 StartZ=0 EndX=-204.932 EndY=26.5605 EndZ=0
    g2: LineSegment StartX=-201.368 StartY=36.3521 StartZ=0 EndX=-180.2 EndY=28.6477 EndZ=0
    g3: LineSegment StartX=-180.2 StartY=28.6477 StartZ=0 EndX=-183.764 EndY=18.8561 EndZ=0
    g4: LineSegment StartX=-183.764 StartY=18.8561 StartZ=0 EndX=-204.932 EndY=26.5605 EndZ=0
  constraints (14):
    c: Parallel(g0,g-3)
    c: Distance(g0) = 4.405
    c: Coincident(g0,g-3)
    c: Coincident(g2,g1)
    c: Coincident(g3,g2)
    c: Coincident(g4,g3)
    c: Coincident(g4,g1)
    c: Parallel(g1,g-3)
    c: Distance(g1) = 10.42
    c: Coincident(g1,g0)
    c: Parallel(g2,g4)
    c: Perpendicular(g1,g2)
    c: DistanceX(g-4,g2) = 5
    c: Parallel(g3,g1)
FEATURE [Part::Extrusion] Extrude006  label="Extrude buco neopixel"
  Base = -> Sketch010
  Dir = (0,-1,2e-16)
  DirMode = 2
  FaceMakerClass = Part::FaceMakerBullseye
  FaceMakerMode = 3
  LengthFwd = 17.2
  LengthRev = 0
  Solid = true
  Symmetric = true
FEATURE [Sketcher::SketchObject] Sketch011  label="fermo grilletto"
  ArcFitTolerance = 1e-06
  AttachmentSupport = -> [XZ_Plane]
  ExternalGeometry = -> [Sketch]
  FullyConstrained = true
  MakeInternals = false
  MapMode = 5
  Placement = pos=(0,0,0) rot=(1,0,0;1.5708rad)
  sketch-geometry (18):
    g0: LineSegment [constr] StartX=-145.51 StartY=22 StartZ=0 EndX=-157.347 EndY=-14.4293 EndZ=0
    g1: LineSegment [constr] StartX=-157.347 StartY=-14.4293 StartZ=0 EndX=-157.841 EndY=-15.951 EndZ=0
    g2: LineSegment StartX=-161.151 StartY=-13.1932 StartZ=0 EndX=-155.825 EndY=-14.9237 EndZ=0
    g3: LineSegment StartX=-163.167 StartY=-14.2205 StartZ=0 EndX=-164.403 EndY=-18.0247 EndZ=0
    g4: LineSegment StartX=-163.376 StartY=-20.0408 StartZ=0 EndX=-158.05 EndY=-21.7713 EndZ=0
    g5: LineSegment StartX=-158.05 StartY=-21.7713 StartZ=0 EndX=-155.825 EndY=-14.9237 EndZ=0
    g6: LineSegment StartX=-161.645 StartY=-14.7149 StartZ=0 EndX=-157.841 EndY=-15.951 EndZ=0
    g7: LineSegment StartX=-157.841 StartY=-15.951 StartZ=0 EndX=-159.077 EndY=-19.7552 EndZ=0
    g8: LineSegment StartX=-159.077 StartY=-19.7552 StartZ=0 EndX=-162.881 EndY=-18.5191 EndZ=0
    g9: LineSegment StartX=-162.881 StartY=-18.5191 StartZ=0 EndX=-161.645 EndY=-14.7149 EndZ=0
    g10: LineSegment [constr] StartX=-161.645 StartY=-14.7149 StartZ=0 EndX=-161.151 EndY=-13.1932 EndZ=0
    g11: LineSegment [constr] StartX=-159.077 StartY=-19.7552 StartZ=0 EndX=-157.555 EndY=-20.2496 EndZ=0
    g12: LineSegment [constr] StartX=-159.077 StartY=-19.7552 StartZ=0 EndX=-159.572 EndY=-21.2769 EndZ=0
    g13: LineSegment [constr] StartX=-161.645 StartY=-14.7149 StartZ=0 EndX=-163.167 EndY=-14.2205 EndZ=0
    g14: ArcOfCircle CenterX=-161.645 CenterY=-14.7149 CenterZ=0 NormalX=0 NormalY=0 NormalZ=1 AngleXU=0 Radius=1.6 StartAngle=1.25664 EndAngle=2.82743
    g15: GeomPoint [constr] X=-162.673 Y=-12.6988 Z=0
    g16: ArcOfCircle CenterX=-162.881 CenterY=-18.5191 CenterZ=0 NormalX=0 NormalY=0 NormalZ=1 AngleXU=0 Radius=1.6 StartAngle=2.82743 EndAngle=4.39823
    g17: GeomPoint [constr] X=-164.897 Y=-19.5464 Z=0
  constraints (48):
    c: Parallel(g0,g-3)
    c: Distance(g0) = 38.304
    c: Coincident(g0,g-3)
    c: Parallel(g1,g-3)
    c: Distance(g1) = 1.6
    c: Coincident(g1,g0)
    c: Coincident(g5,g4)
    c: Coincident(g5,g2)
    c: Coincident(g7,g6)
    c: Coincident(g8,g7)
    c: Coincident(g9,g8)
    c: Coincident(g9,g6)
    c: Parallel(g7,g-3)
    c: Parallel(g9,g7)
    c: Perpendicular(g6,g7)
    c: Parallel(g6,g8)
    c: Distance(g6) = 4
    c: Distance(g9) = 4
    c: Parallel(g5,g7)
    c: Parallel(g9,g3)
    c: Parallel(g2,g6)
    c: Parallel(g4,g8)
    c: Parallel(g13,g6)
    c: Parallel(g10,g9)
    c: Parallel(g11,g8)
    c: Parallel(g12,g7)
    c: Distance(g10) = 1.6
    c: Distance(g13) = 1.6
    c: Distance(g12) = 1.6
    c: Distance(g11) = 1.6
    c: Coincident(g10,g6)
    c: Coincident(g13,g6)
    c: Coincident(g12,g7)
    c: Coincident(g11,g7)
    c: Distance(g10,g15) = 1.6
    c: Distance(g15,g13) = 1.6
    c: Distance(g4,g12) = 1.6
    c: Distance(g4,g11) = 1.6
    c: PointOnObject(g15,g2)
    c: Tangent(g3,g14) = -1.5708
    c: Tangent(g2,g14) = 1.5708
    c: PointOnObject(g17,g4)
    c: PointOnObject(g17,g3)
    c: Tangent(g4,g16) = -1.5708
    c: Tangent(g3,g16) = -1.5708
    c: Equal(g16,g14)
    c: Coincident(g16,g8)
    c: Coincident(g6,g1)
FEATURE [Part::Extrusion] Extrude007  label="Extrude fermo grilletto"
  Base = -> Sketch011
  Dir = (0,-1,2e-16)
  DirMode = 2
  FaceMakerClass = Part::FaceMakerBullseye
  FaceMakerMode = 3
  LengthFwd = 25.2
  LengthRev = 0
  Solid = true
  Symmetric = true
FEATURE [Sketcher::SketchObject] Sketch012  label="buco oled"
  ArcFitTolerance = 1e-06
  AttachmentSupport = -> [XZ_Plane]
  ExternalGeometry = -> [Sketch]
  FullyConstrained = true
  MakeInternals = false
  MapMode = 5
  Placement = pos=(0,0,0) rot=(1,0,0;1.5708rad)
  sketch-geometry (4):
    g0: LineSegment StartX=-185.747 StartY=58.0965 StartZ=0 EndX=-180.232 EndY=56.0891 EndZ=0
    g1: LineSegment StartX=-185.747 StartY=58.0965 StartZ=0 EndX=-185.747 EndY=67.3588 EndZ=0
    g2: LineSegment StartX=-185.747 StartY=67.3588 StartZ=0 EndX=-180.232 EndY=67.3588 EndZ=0
    g3: LineSegment StartX=-180.232 StartY=67.3588 StartZ=0 EndX=-180.232 EndY=56.0891 EndZ=0
  constraints (10):
    c: Coincident(g1,g0)
    c: Coincident(g2,g1)
    c: Coincident(g3,g2)
    c: Coincident(g3,g0)
    c: Parallel(g1,g-5)
    c: Perpendicular(g-3,g0)
    c: Parallel(g2,g-6)
    c: Parallel(g3,g-4)
    c: Coincident(g0,g-5)
    c: Coincident(g2,g-6)
FEATURE [Part::Extrusion] Extrude008  label="Extrude buco oled"
  Base = -> Sketch012
  Dir = (0,-1,2e-16)
  DirMode = 2
  FaceMakerClass = Part::FaceMakerBullseye
  FaceMakerMode = 3
  LengthFwd = 12.8
  LengthRev = 0
  Solid = true
  Symmetric = true
FEATURE [Sketcher::SketchObject] Sketch013  label="buco pompa"
  ArcFitTolerance = 1e-06
  AttachmentSupport = -> [XZ_Plane]
  ExternalGeometry = -> [Sketch]
  FullyConstrained = true
  MakeInternals = false
  MapMode = 5
  Placement = pos=(0,0,0) rot=(1,0,0;1.5708rad)
  sketch-geometry (8):
    g0: LineSegment StartX=-82.8 StartY=-10.4 StartZ=0 EndX=-82.8 EndY=-9.6 EndZ=0
    g1: LineSegment StartX=-82.8 StartY=-9.6 StartZ=0 EndX=-67.9 EndY=-9.6 EndZ=0
    g2: LineSegment StartX=-67.9 StartY=-9.6 StartZ=0 EndX=-67.9 EndY=6 EndZ=0
    g3: LineSegment StartX=-67.9 StartY=6 StartZ=0 EndX=-65.9 EndY=6 EndZ=0
    g4: LineSegment StartX=-65.9 StartY=6 StartZ=0 EndX=-65.9 EndY=-1.7 EndZ=0
    g5: LineSegment StartX=-65.9 StartY=-1.7 StartZ=0 EndX=-57.2 EndY=-1.7 EndZ=0
    g6: LineSegment StartX=-57.2 StartY=-1.7 StartZ=0 EndX=-57.2 EndY=-10.4 EndZ=0
    g7: LineSegment StartX=-57.2 StartY=-10.4 StartZ=0 EndX=-82.8 EndY=-10.4 EndZ=0
  constraints (22):
    c: Vertical(g0)
    c: Coincident(g1,g0)
    c: Horizontal(g1)
    c: Coincident(g2,g1)
    c: Vertical(g2)
    c: Coincident(g3,g2)
    c: Horizontal(g3)
    c: Coincident(g4,g3)
    c: Vertical(g4)
    c: Coincident(g5,g4)
    c: Horizontal(g5)
    c: Coincident(g6,g5)
    c: Vertical(g6)
    c: Coincident(g7,g6)
    c: Coincident(g7,g0)
    c: DistanceY(g0,g0) = 0.8
    c: DistanceY(g6,g6) = 8.7
    c: DistanceX(g1,g1) = 14.9
    c: DistanceX(g3,g3) = 2
    c: Coincident(g0,g-4)
    c: DistanceY(g2,g-6) = 0
    c: Coincident(g6,g-5)
FEATURE [Part::Extrusion] Extrude009  label="Extrude buco pompa"
  Base = -> Sketch013
  Dir = (0,-1,2e-16)
  DirMode = 2
  FaceMakerClass = Part::FaceMakerBullseye
  FaceMakerMode = 3
  LengthFwd = 13.2
  LengthRev = 0
  Solid = true
  Symmetric = true
FEATURE [Sketcher::SketchObject] Sketch014  label="buco frontale"
  ArcFitTolerance = 1e-06
  AttachmentSupport = -> [XZ_Plane]
  ExternalGeometry = -> [Sketch]
  FullyConstrained = true
  MakeInternals = false
  MapMode = 5
  Placement = pos=(0,0,0) rot=(1,0,0;1.5708rad)
  sketch-geometry (10):
    g0: LineSegment StartX=0 StartY=0 StartZ=0 EndX=0 EndY=24.671 EndZ=0
    g1: LineSegment StartX=0 StartY=24.671 StartZ=0 EndX=-4 EndY=24.671 EndZ=0
    g2: LineSegment StartX=-4 StartY=24.671 StartZ=0 EndX=-4 EndY=16 EndZ=0
    g3: LineSegment StartX=-4 StartY=16 StartZ=0 EndX=-2.4 EndY=16 EndZ=0
    g4: LineSegment StartX=-2.4 StartY=16 StartZ=0 EndX=-2.4 EndY=10 EndZ=0
    g5: LineSegment StartX=-2.4 StartY=10 StartZ=0 EndX=-12 EndY=10 EndZ=0
    g6: LineSegment StartX=-12 StartY=10 StartZ=0 EndX=-12 EndY=6 EndZ=0
    g7: LineSegment StartX=-12 StartY=6 StartZ=0 EndX=-2.4 EndY=6 EndZ=0
    g8: LineSegment StartX=-2.4 StartY=6 StartZ=0 EndX=-2.4 EndY=0 EndZ=0
    g9: LineSegment StartX=-2.4 StartY=0 StartZ=0 EndX=0 EndY=0 EndZ=0
  constraints (29):
    c: Vertical(g0)
    c: Coincident(g1,g0)
    c: Horizontal(g1)
    c: Coincident(g2,g1)
    c: Vertical(g2)
    c: Coincident(g3,g2)
    c: Horizontal(g3)
    c: Coincident(g4,g3)
    c: Vertical(g4)
    c: Coincident(g5,g4)
    c: Horizontal(g5)
    c: Coincident(g6,g5)
    c: Vertical(g6)
    c: Coincident(g7,g6)
    c: Coincident(g8,g7)
    c: Vertical(g8)
    c: Coincident(g9,g8)
    c: Coincident(g9,g0)
    c: Horizontal(g9)
    c: DistanceY(g0,g0) = 24.671
    c: Horizontal(g7)
    c: DistanceY(g6,g6) = 4
    c: DistanceY(g4,g4) = 6
    c: DistanceX(g9,g9) = 2.4
    c: Coincident(g0,g-1)
    c: DistanceY(g-3,g7) = 0
    c: DistanceX(g8,g4) = 0
    c: DistanceX(g-3,g1) = 0
    c: DistanceX(g6,g-3) = 8
FEATURE [Part::Extrusion] Extrude010  label="Extrude buco frontale"
  Base = -> Sketch014
  Dir = (0,-1,2e-16)
  DirMode = 2
  FaceMakerClass = Part::FaceMakerBullseye
  FaceMakerMode = 3
  LengthFwd = 11.2
  LengthRev = 0
  Solid = true
  Symmetric = true
FEATURE [Sketcher::SketchObject] Sketch015  label="guida rail"
  ArcFitTolerance = 1e-06
  AttachmentSupport = -> [XZ_Plane]
  ExternalGeometry = -> [Sketch]
  FullyConstrained = true
  MakeInternals = false
  MapMode = 5
  Placement = pos=(0,0,0) rot=(1,0,0;1.5708rad)
  sketch-geometry (4):
    g0: LineSegment StartX=-100.8 StartY=43.2 StartZ=0 EndX=-44.6 EndY=43.2 EndZ=0
    g1: LineSegment StartX=-44.6 StartY=43.2 StartZ=0 EndX=-44.6 EndY=41.2 EndZ=0
    g2: LineSegment StartX=-44.6 StartY=41.2 StartZ=0 EndX=-100.8 EndY=41.2 EndZ=0
    g3: LineSegment StartX=-100.8 StartY=41.2 StartZ=0 EndX=-100.8 EndY=43.2 EndZ=0
  constraints (9):
    c: Horizontal(g0)
    c: Coincident(g1,g0)
    c: Coincident(g2,g1)
    c: Coincident(g3,g2)
    c: Coincident(g3,g0)
    c: Vertical(g3)
    c: Coincident(g2,g-3)
    c: Coincident(g1,g-3)
    c: Coincident(g0,g-4)
FEATURE [Part::Extrusion] Extrude011  label="Extrude guida rail"
  Base = -> Sketch015
  Dir = (0,-1,2e-16)
  DirMode = 2
  FaceMakerClass = Part::FaceMakerBullseye
  FaceMakerMode = 3
  LengthFwd = 9
  LengthRev = 0
  Solid = true
  Symmetric = true
FEATURE [Sketcher::SketchObject] Sketch016  label="guide per coperture laterali"
  ArcFitTolerance = 1e-06
  AttachmentSupport = -> [XZ_Plane]
  ExternalGeometry = -> [Sketch]
  FullyConstrained = true
  MakeInternals = false
  MapMode = 5
  Placement = pos=(0,0,0) rot=(1,0,0;1.5708rad)
  sketch-geometry (14):
    g0: Circle CenterX=-5.6 CenterY=7.6 CenterZ=0 NormalX=0 NormalY=0 NormalZ=1 AngleXU=0 Radius=1.6
    g1: Circle CenterX=-5.6 CenterY=7.6 CenterZ=0 NormalX=0 NormalY=0 NormalZ=1 AngleXU=0 Radius=4
    g2: Circle CenterX=-5.6 CenterY=34.8 CenterZ=0 NormalX=0 NormalY=0 NormalZ=1 AngleXU=0 Radius=1.6
    g3: Circle CenterX=-5.6 CenterY=34.8 CenterZ=0 NormalX=0 NormalY=0 NormalZ=1 AngleXU=0 Radius=4
    g4: Circle CenterX=-184.08 CenterY=34.8 CenterZ=0 NormalX=0 NormalY=0 NormalZ=1 AngleXU=0 Radius=1.6
    g5: Circle CenterX=-184.08 CenterY=34.8 CenterZ=0 NormalX=0 NormalY=0 NormalZ=1 AngleXU=0 Radius=4
    g6: Circle CenterX=-179.305 CenterY=-76.8316 CenterZ=0 NormalX=0 NormalY=0 NormalZ=1 AngleXU=0 Radius=1.6
    g7: Circle CenterX=-179.305 CenterY=-76.8316 CenterZ=0 NormalX=0 NormalY=0 NormalZ=1 AngleXU=0 Radius=4
    g8: Circle CenterX=-213.443 CenterY=-76.8316 CenterZ=0 NormalX=0 NormalY=0 NormalZ=1 AngleXU=0 Radius=1.6
    g9: Circle CenterX=-213.443 CenterY=-76.8316 CenterZ=0 NormalX=0 NormalY=0 NormalZ=1 AngleXU=0 Radius=4
    g10: Circle CenterX=-78.51 CenterY=7.6 CenterZ=0 NormalX=0 NormalY=0 NormalZ=1 AngleXU=0 Radius=1.6
    g11: Circle CenterX=-78.51 CenterY=7.6 CenterZ=0 NormalX=0 NormalY=0 NormalZ=1 AngleXU=0 Radius=4
    g12: Circle CenterX=-78.51 CenterY=34.8 CenterZ=0 NormalX=0 NormalY=0 NormalZ=1 AngleXU=0 Radius=1.6
    g13: Circle CenterX=-78.51 CenterY=34.8 CenterZ=0 NormalX=0 NormalY=0 NormalZ=1 AngleXU=0 Radius=4
  constraints (35):
    c: Diameter(g0) = 3.2
    c: Diameter(g1) = 8
    c: Coincident(g0,g1)
    c: Diameter(g2) = 3.2
    c: Diameter(g3) = 8
    c: Coincident(g3,g2)
    c: Tangent(g2,g-7)
    c: Diameter(g4) = 3.2
    c: Diameter(g5) = 8
    c: Coincident(g5,g4)
    c: Tangent(g4,g-7)
    c: Tangent(g4,g-8)
    c: Diameter(g6) = 3.2
    c: Diameter(g7) = 8
    c: Coincident(g7,g6)
    c: Tangent(g6,g-9)
    c: Tangent(g6,g-10)
    c: Diameter(g8) = 3.2
    c: Diameter(g9) = 8
    c: Coincident(g9,g8)
    c: Tangent(g8,g-10)
    c: Tangent(g8,g-11)
    c: Diameter(g10) = 3.2
    c: Diameter(g11) = 8
    c: Diameter(g12) = 3.2
    c: Diameter(g13) = 8
    c: Coincident(g12,g13)
    c: Coincident(g10,g11)
    c: Tangent(g12,g-7)
    c: DistanceX(g12,g10) = 0
    c: Tangent(g2,g-6)
    c: Tangent(g0,g-6)
    c: Tangent(g0,g-3)
    c: Tangent(g10,g-3)
    c: Tangent(g10,g-4)
FEATURE [Part::Extrusion] Extrude012  label="extrude guide per coperture laterali"
  Base = -> Sketch016
  Dir = (0,-1,2e-16)
  DirMode = 2
  FaceMakerClass = Part::FaceMakerBullseye
  FaceMakerMode = 3
  LengthFwd = 25.2
  LengthRev = 0
  Solid = true
  Symmetric = true
FEATURE [Sketcher::SketchObject] Sketch017  label="supporto CAM"
  ArcFitTolerance = 1e-06
  AttachmentSupport = -> [XZ_Plane]
  ExternalGeometry = -> [Sketch]
  FullyConstrained = true
  MakeInternals = false
  MapMode = 5
  Placement = pos=(0,0,0) rot=(1,0,0;1.5708rad)
  sketch-geometry (6):
    g0: LineSegment StartX=-2.4 StartY=48 StartZ=0 EndX=-2.4 EndY=41.2 EndZ=0
    g1: LineSegment StartX=-2.4 StartY=48 StartZ=0 EndX=-34 EndY=48 EndZ=0
    g2: LineSegment StartX=-34 StartY=48 StartZ=0 EndX=-34 EndY=46.72 EndZ=0
    g3: LineSegment StartX=-34 StartY=46.72 StartZ=0 EndX=-36 EndY=46.72 EndZ=0
    g4: LineSegment StartX=-36 StartY=46.72 StartZ=0 EndX=-36 EndY=41.2 EndZ=0
    g5: LineSegment StartX=-36 StartY=41.2 StartZ=0 EndX=-2.4 EndY=41.2 EndZ=0
  constraints (15):
    c: Coincident(g1,g0)
    c: Horizontal(g1)
    c: Coincident(g2,g1)
    c: Vertical(g2)
    c: Coincident(g3,g2)
    c: Horizontal(g3)
    c: Coincident(g4,g3)
    c: Coincident(g5,g4)
    c: DistanceX(g1,g0) = 31.6
    c: Coincident(g5,g0)
    c: Vertical(g4)
    c: DistanceY(g2,g1) = 1.28
    c: Coincident(g0,g-3)
    c: Coincident(g0,g-3)
    c: Coincident(g4,g-4)
FEATURE [Part::Extrusion] Extrude013  label="Extrude supporto CAM"
  Base = -> Sketch017
  Dir = (0,-1,2e-16)
  DirMode = 2
  FaceMakerClass = Part::FaceMakerBullseye
  FaceMakerMode = 3
  LengthFwd = 17.8
  LengthRev = 0
  Solid = true
  Symmetric = true
FEATURE [Sketcher::SketchObject] Sketch018  label="Scavo CAM"
  ArcFitTolerance = 1e-06
  AttachmentSupport = -> [YZ_Plane]
  ExternalGeometry = -> [Sketch]
  FullyConstrained = true
  MakeInternals = false
  MapMode = 5
  Placement = pos=(0,0,0) rot=(0.57735,0.57735,0.57735;2.0944rad)
  sketch-geometry (4):
    g0: LineSegment StartX=-7.73 StartY=48 StartZ=0 EndX=7.73 EndY=48 EndZ=0
    g1: LineSegment [constr] StartX=1.07e-14 StartY=48 StartZ=0 EndX=0 EndY=43.5155 EndZ=0
    g2: ArcOfCircle CenterX=9e-15 CenterY=52.42 CenterZ=0 NormalX=0 NormalY=0 NormalZ=1 AngleXU=0 Radius=8.90445 StartAngle=3.66102 EndAngle=5.76376
    g3: Circle [constr] CenterX=9e-15 CenterY=52.42 CenterZ=0 NormalX=0 NormalY=0 NormalZ=1 AngleXU=0 Radius=8.9
  constraints (13):
    c: Horizontal(g0)
    c: DistanceY(g-3,g0) = 0
    c: DistanceX(g0,g0) = 15.46
    c: DistanceX(g0,g-3) = 7.73
    c: DistanceX(g-3) = 0
    c: Coincident(g1,g-3)
    c: PointOnObject(g1,g-2)
    c: Coincident(g2,g0)
    c: Coincident(g2,g0)
    c: PointOnObject(g1,g2)
    c: Diameter(g3) = 17.8
    c: DistanceY(g1,g3) = 4.42
    c: Coincident(g2,g3)
FEATURE [Part::Extrusion] Extrude014  label="Extrude Scavo CAM"
  Base = -> Sketch018
  Dir = (1,0,0)
  DirMode = 2
  FaceMakerClass = Part::FaceMakerBullseye
  FaceMakerMode = 3
  LengthFwd = -34
  LengthRev = 0
  Solid = true
  Symmetric = false
FEATURE [Sketcher::SketchObject] Sketch019  label="scavo rumble"
  ArcFitTolerance = 1e-06
  AttachmentSupport = -> [XZ_Plane]
  ExternalGeometry = -> [Sketch]
  FullyConstrained = true
  MakeInternals = false
  MapMode = 5
  Placement = pos=(0,0,0) rot=(1,0,0;1.5708rad)
  sketch-geometry (6):
    g0: LineSegment StartX=-163.771 StartY=-21.9058 StartZ=0 EndX=-158.636 EndY=-23.5745 EndZ=0
    g1: LineSegment StartX=-158.636 StartY=-23.5745 StartZ=0 EndX=-165.743 EndY=-45.4488 EndZ=0
    g2: LineSegment StartX=-165.743 StartY=-45.4488 StartZ=0 EndX=-170.879 EndY=-43.7801 EndZ=0
    g3: LineSegment StartX=-170.879 StartY=-43.7801 StartZ=0 EndX=-163.771 EndY=-21.9058 EndZ=0
    g4: LineSegment [constr] StartX=-145.51 StartY=22 StartZ=0 EndX=-160.157 EndY=-23.0801 EndZ=0
    g5: LineSegment [constr] StartX=-158.636 StartY=-23.5745 StartZ=0 EndX=-160.157 EndY=-23.0801 EndZ=0
  constraints (17):
    c: Coincident(g1,g0)
    c: Coincident(g2,g1)
    c: Coincident(g3,g2)
    c: Coincident(g3,g0)
    c: Parallel(g3,g-3)
    c: Parallel(g3,g1)
    c: Perpendicular(g3,g0)
    c: Perpendicular(g2,g3)
    c: Distance(g2,g0) = 23
    c: Parallel(g4,g-3)
    c: Distance(g4) = 47.4
    c: Coincident(g4,g-3)
    c: Parallel(g5,g0)
    c: Distance(g5) = 1.6
    c: Coincident(g5,g0)
    c: Distance(g5,g0) = 3.8
    c: Coincident(g5,g4)
FEATURE [Part::Extrusion] Extrude015  label="scavo rumble001"
  Base = -> Sketch019
  Dir = (0,-1,2e-16)
  DirMode = 2
  FaceMakerClass = Part::FaceMakerBullseye
  FaceMakerMode = 3
  LengthFwd = 21
  LengthRev = 0
  Solid = true
  Symmetric = true
FEATURE [Sketcher::SketchObject] Sketch020  label="fermo rumble"
  ArcFitTolerance = 1e-06
  AttachmentSupport = -> [XZ_Plane]
  ExternalGeometry = -> [Sketch019,Sketch]
  FullyConstrained = true
  MakeInternals = false
  MapMode = 5
  Placement = pos=(0,0,0) rot=(1,0,0;1.5708rad)
  sketch-geometry (16):
    g0: LineSegment [constr] StartX=-165.905 StartY=-40.7697 StartZ=0 EndX=-167.265 EndY=-44.9544 EndZ=0
    g1: LineSegment [constr] StartX=-167.265 StartY=-44.9544 StartZ=0 EndX=-165.743 EndY=-45.4488 EndZ=0
    g2: LineSegment StartX=-167.318 StartY=-37.9976 StartZ=0 EndX=-165.225 EndY=-38.6774 EndZ=0
    g3: LineSegment StartX=-165.225 StartY=-38.6774 StartZ=0 EndX=-165.905 EndY=-40.7697 EndZ=0
    g4: LineSegment StartX=-165.905 StartY=-40.7697 StartZ=0 EndX=-167.997 EndY=-40.0899 EndZ=0
    g5: LineSegment StartX=-167.997 StartY=-40.0899 StartZ=0 EndX=-167.318 EndY=-37.9976 EndZ=0
    g6: LineSegment StartX=-166.823 StartY=-36.4759 StartZ=0 EndX=-163.399 EndY=-37.5883 EndZ=0
    g7: LineSegment StartX=-163.399 StartY=-37.5883 StartZ=0 EndX=-165.006 EndY=-42.5338 EndZ=0
    g8: LineSegment StartX=-165.006 StartY=-42.5338 StartZ=0 EndX=-168.43 EndY=-41.4214 EndZ=0
    g9: LineSegment StartX=-169.457 StartY=-39.4053 StartZ=0 EndX=-168.839 EndY=-37.5031 EndZ=0
    g10: LineSegment [constr] StartX=-168.839 StartY=-37.5031 StartZ=0 EndX=-168.345 EndY=-35.9815 EndZ=0
    g11: LineSegment [constr] StartX=-168.345 StartY=-35.9815 StartZ=0 EndX=-166.823 EndY=-36.4759 EndZ=0
    g12: ArcOfCircle CenterX=-167.936 CenterY=-39.8997 CenterZ=0 NormalX=0 NormalY=0 NormalZ=1 AngleXU=0 Radius=1.6 StartAngle=2.82743 EndAngle=4.39823
    g13: GeomPoint [constr] X=-169.952 Y=-40.9269 Z=0
    g14: ArcOfCircle CenterX=-167.318 CenterY=-37.9976 CenterZ=0 NormalX=0 NormalY=0 NormalZ=1 AngleXU=0 Radius=1.6 StartAngle=1.25664 EndAngle=2.82743
    g15: GeomPoint [constr] X=-168.345 Y=-35.9815 Z=0
  constraints (42):
    c: Parallel(g0,g-4)
    c: Distance(g0) = 4.4
    c: Coincident(g1,g0)
    c: Perpendicular(g0,g1)
    c: Distance(g1) = 1.6
    c: Coincident(g1,g-5)
    c: Coincident(g3,g2)
    c: Coincident(g4,g3)
    c: Coincident(g5,g4)
    c: Coincident(g5,g2)
    c: Parallel(g3,g-4)
    c: Parallel(g3,g5)
    c: Perpendicular(g2,g3)
    c: Parallel(g4,g2)
    c: Distance(g2) = 2.2
    c: Distance(g3) = 2.2
    c: Coincident(g7,g6)
    c: Coincident(g8,g7)
    c: Parallel(g7,g-4)
    c: Parallel(g7,g9)
    c: Perpendicular(g6,g7)
    c: Parallel(g6,g8)
    c: Distance(g6,g15) = 5.2
    c: Distance(g7) = 5.2
    c: Coincident(g11,g10)
    c: Parallel(g10,g9)
    c: Parallel(g11,g6)
    c: Distance(g10) = 1.6
    c: Distance(g11) = 1.6
    c: Coincident(g10,g15)
    c: Distance(g11,g2) = 1.6
    c: Distance(g2,g10) = 1.6
    c: PointOnObject(g13,g8)
    c: PointOnObject(g13,g9)
    c: Tangent(g8,g12) = 1.5708
    c: Tangent(g9,g12) = 1.5708
    c: PointOnObject(g15,g9)
    c: Tangent(g6,g14) = 1.5708
    c: Tangent(g9,g14) = 1.5708
    c: Equal(g12,g14)
    c: Coincident(g6,g11)
    c: Coincident(g3,g0)
FEATURE [Part::Extrusion] Extrude016  label="Extrude fermo rumble"
  Base = -> Sketch020
  Dir = (0,-1,2e-16)
  DirMode = 2
  FaceMakerClass = Part::FaceMakerBullseye
  FaceMakerMode = 3
  LengthFwd = 25.2
  LengthRev = 0
  Solid = true
  Symmetric = true
FEATURE [Sketcher::SketchObject] Sketch021  label="perno fermo rumble001"
  ArcFitTolerance = 1e-06
  AttachmentSupport = -> [XZ_Plane001]
  FullyConstrained = true
  MakeInternals = false
  MapMode = 5
  Placement = pos=(0,0,0) rot=(1,0,0;1.5708rad)
  sketch-geometry (16):
    g0: LineSegment StartX=0 StartY=0.45 StartZ=0 EndX=0 EndY=1.55 EndZ=0
    g1: LineSegment StartX=0.45 StartY=2 StartZ=0 EndX=1.55 EndY=2 EndZ=0
    g2: LineSegment StartX=2 StartY=1.55 StartZ=0 EndX=2 EndY=0.45 EndZ=0
    g3: LineSegment StartX=1.55 StartY=0 StartZ=0 EndX=0.45 EndY=0 EndZ=0
    g4: ArcOfCircle [constr] CenterX=0.45 CenterY=1.55 CenterZ=0 NormalX=0 NormalY=0 NormalZ=1 AngleXU=0 Radius=0.45 StartAngle=1.5708 EndAngle=3.14159
    g5: GeomPoint [constr] X=0 Y=2 Z=0
    g6: LineSegment StartX=0.45 StartY=2 StartZ=0 EndX=0 EndY=1.55 EndZ=0
    g7: ArcOfCircle [constr] CenterX=1.55 CenterY=1.55 CenterZ=0 NormalX=0 NormalY=0 NormalZ=1 AngleXU=0 Radius=0.45 StartAngle=0 EndAngle=1.5708
    g8: GeomPoint [constr] X=2 Y=2 Z=0
    g9: LineSegment StartX=2 StartY=1.55 StartZ=0 EndX=1.55 EndY=2 EndZ=0
    g10: ArcOfCircle [constr] CenterX=1.55 CenterY=0.45 CenterZ=0 NormalX=0 NormalY=0 NormalZ=1 AngleXU=0 Radius=0.45 StartAngle=4.71239 EndAngle=6.28319
    g11: GeomPoint [constr] X=2 Y=0 Z=0
    g12: LineSegment StartX=1.55 StartY=0 StartZ=0 EndX=2 EndY=0.45 EndZ=0
    g13: ArcOfCircle [constr] CenterX=0.45 CenterY=0.45 CenterZ=0 NormalX=0 NormalY=0 NormalZ=1 AngleXU=0 Radius=0.45 StartAngle=3.14159 EndAngle=4.71239
    g14: GeomPoint [constr] X=0 Y=0 Z=0
    g15: LineSegment StartX=0 StartY=0.45 StartZ=0 EndX=0.45 EndY=0 EndZ=0
  constraints (35):
    c: Coincident(g14,g-1)
    c: PointOnObject(g5,g-2)
    c: Horizontal(g1)
    c: Vertical(g2)
    c: Horizontal(g3)
    c: DistanceX(g5,g8) = 2
    c: DistanceY(g11,g8) = 2
    c: PointOnObject(g5,g0)
    c: PointOnObject(g5,g1)
    c: Tangent(g0,g4) = 1.5708
    c: Tangent(g1,g4) = 1.5708
    c: Coincident(g6,g0)
    c: Coincident(g6,g1)
    c: PointOnObject(g8,g2)
    c: PointOnObject(g8,g1)
    c: Tangent(g2,g7) = 1.5708
    c: Tangent(g1,g7) = 1.5708
    c: Coincident(g9,g2)
    c: Coincident(g9,g1)
    c: PointOnObject(g11,g2)
    c: PointOnObject(g11,g3)
    c: Tangent(g2,g10) = 1.5708
    c: Tangent(g3,g10) = 1.5708
    c: Coincident(g12,g2)
    c: Coincident(g12,g3)
    c: PointOnObject(g14,g0)
    c: PointOnObject(g14,g3)
    c: Tangent(g0,g13) = 1.5708
    c: Tangent(g3,g13) = 1.5708
    c: Coincident(g15,g0)
    c: Coincident(g15,g3)
    c: Equal(g6,g9)
    c: Equal(g9,g12)
    c: Equal(g12,g15)
    c: DistanceX(g14,g3) = 0.45
FEATURE [Sketcher::SketchObject] Sketch022  label="fori per M3x5(OD)x6(L)"
  ArcFitTolerance = 1e-06
  AttachmentSupport = -> [XZ_Plane]
  ExternalGeometry = -> [Sketch016]
  FullyConstrained = true
  MakeInternals = false
  MapMode = 5
  Placement = pos=(0,0,0) rot=(1,0,0;1.5708rad)
  sketch-geometry (7):
    g0: Circle CenterX=-5.6 CenterY=34.8 CenterZ=0 NormalX=0 NormalY=0 NormalZ=1 AngleXU=0 Radius=2.5
    g1: Circle CenterX=-5.6 CenterY=7.6 CenterZ=0 NormalX=0 NormalY=0 NormalZ=1 AngleXU=0 Radius=2.5
    g2: Circle CenterX=-78.51 CenterY=34.8 CenterZ=0 NormalX=0 NormalY=0 NormalZ=1 AngleXU=0 Radius=2.5
    g3: Circle CenterX=-78.51 CenterY=7.6 CenterZ=0 NormalX=0 NormalY=0 NormalZ=1 AngleXU=0 Radius=2.5
    g4: Circle CenterX=-184.08 CenterY=34.8 CenterZ=0 NormalX=0 NormalY=0 NormalZ=1 AngleXU=0 Radius=2.5
    g5: Circle CenterX=-179.305 CenterY=-76.8316 CenterZ=0 NormalX=0 NormalY=0 NormalZ=1 AngleXU=0 Radius=2.5
    g6: Circle CenterX=-213.443 CenterY=-76.8316 CenterZ=0 NormalX=0 NormalY=0 NormalZ=1 AngleXU=0 Radius=2.5
  constraints (14):
    c: Diameter(g0) = 5
    c: Diameter(g1) = 5
    c: Diameter(g2) = 5
    c: Diameter(g3) = 5
    c: Diameter(g4) = 5
    c: Diameter(g5) = 5
    c: Diameter(g6) = 5
    c: Coincident(g0,g-8)
    c: Coincident(g1,g-9)
    c: Coincident(g2,g-6)
    c: Coincident(g3,g-7)
    c: Coincident(g4,g-5)
    c: Coincident(g5,g-4)
    c: Coincident(g6,g-3)
FEATURE [Part::Extrusion] Extrude018  label="Extrude fori M3x5x6 - dx"
  Base = -> Sketch022
  Dir = (0,-1,2e-16)
  DirMode = 2
  FaceMakerClass = Part::FaceMakerBullseye
  FaceMakerMode = 3
  LengthFwd = 6.2
  LengthRev = 0
  Placement = pos=(0,-9.5,0) rot=(0,0,1;0rad)
  Solid = true
  Symmetric = true
FEATURE [Part::Extrusion] Extrude019  label="Extrude fori M3x5x6 - sx"
  Base = -> Sketch022
  Dir = (0,-1,2e-16)
  DirMode = 2
  FaceMakerClass = Part::FaceMakerBullseye
  FaceMakerMode = 3
  LengthFwd = 6.2
  LengthRev = 0
  Placement = pos=(0,9.5,0) rot=(0,0,1;0rad)
  Solid = true
  Symmetric = true
FEATURE [Sketcher::SketchObject] Sketch023  label="foro anteriore M3x5x6"
  ArcFitTolerance = 1e-06
  AttachmentSupport = -> [YZ_Plane]
  FullyConstrained = true
  MakeInternals = false
  MapMode = 5
  Placement = pos=(0,0,0) rot=(0.57735,0.57735,0.57735;2.0944rad)
  sketch-geometry (2):
    g0: LineSegment [constr] StartX=0 StartY=0 StartZ=0 EndX=0 EndY=38.6 EndZ=0
    g1: Circle CenterX=0 CenterY=38.6 CenterZ=0 NormalX=0 NormalY=0 NormalZ=1 AngleXU=0 Radius=2.5
  constraints (5):
    c: Coincident(g0,g-1)
    c: PointOnObject(g0,g-2)
    c: DistanceY(g0,g0) = 38.6
    c: Diameter(g1) = 5
    c: Coincident(g1,g0)
FEATURE [Part::Extrusion] Extrude020  label="Extrude foro anteriore M3x5x6"
  Base = -> Sketch023
  Dir = (1,0,0)
  DirMode = 2
  FaceMakerClass = Part::FaceMakerBullseye
  FaceMakerMode = 3
  LengthFwd = -6.2
  LengthRev = 0
  Solid = true
  Symmetric = false
FEATURE [Sketcher::SketchObject] Sketch024  label="fori per viti frontale"
  ArcFitTolerance = 1e-06
  AttachmentSupport = -> [YZ_Plane]
  FullyConstrained = true
  MakeInternals = false
  MapMode = 5
  Placement = pos=(0,0,0) rot=(0.57735,0.57735,0.57735;2.0944rad)
  sketch-geometry (9):
    g0: LineSegment [constr] StartX=-10.3 StartY=30.721 StartZ=0 EndX=10.3 EndY=30.721 EndZ=0
    g1: LineSegment [constr] StartX=10.3 StartY=30.721 StartZ=0 EndX=10.3 EndY=10.121 EndZ=0
    g2: LineSegment [constr] StartX=10.3 StartY=10.121 StartZ=0 EndX=-10.3 EndY=10.121 EndZ=0
    g3: LineSegment [constr] StartX=-10.3 StartY=10.121 StartZ=0 EndX=-10.3 EndY=30.721 EndZ=0
    g4: LineSegment [constr] StartX=0 StartY=0 StartZ=0 EndX=0 EndY=10.121 EndZ=0
    g5: Circle CenterX=-10.3 CenterY=30.721 CenterZ=0 NormalX=0 NormalY=0 NormalZ=1 AngleXU=0 Radius=2
    g6: Circle CenterX=10.3 CenterY=30.721 CenterZ=0 NormalX=0 NormalY=0 NormalZ=1 AngleXU=0 Radius=2
    g7: Circle CenterX=-10.3 CenterY=10.121 CenterZ=0 NormalX=0 NormalY=0 NormalZ=1 AngleXU=0 Radius=2
    g8: Circle CenterX=10.3 CenterY=10.121 CenterZ=0 NormalX=0 NormalY=0 NormalZ=1 AngleXU=0 Radius=2
  constraints (22):
    c: Horizontal(g0)
    c: Coincident(g1,g0)
    c: Vertical(g1)
    c: Coincident(g2,g1)
    c: Horizontal(g2)
    c: Coincident(g3,g2)
    c: Coincident(g3,g0)
    c: Vertical(g3)
    c: DistanceX(g0,g0) = 20.6
    c: DistanceY(g3,g3) = 20.6
    c: Coincident(g4,g-1)
    c: PointOnObject(g4,g-2)
    c: DistanceY(g4,g4) = 10.121
    c: Symmetric(g2,g2,g4)
    c: Diameter(g5) = 4
    c: Diameter(g6) = 4
    c: Diameter(g7) = 4
    c: Diameter(g8) = 4
    c: Coincident(g5,g0)
    c: Coincident(g6,g0)
    c: Coincident(g7,g2)
    c: Coincident(g8,g1)
FEATURE [Part::Extrusion] Extrude021  label="Extrude fori per viti frontale"
  Base = -> Sketch024
  Dir = (1,0,0)
  DirMode = 2
  FaceMakerClass = Part::FaceMakerBullseye
  FaceMakerMode = 3
  LengthFwd = -2.4
  LengthRev = 0
  Solid = true
  Symmetric = false
FEATURE [Sketcher::SketchObject] Sketch025  label="foro per filo CAM"
  ArcFitTolerance = 1e-06
  AttachmentSupport = -> [XZ_Plane]
  ExternalGeometry = -> [Sketch]
  FullyConstrained = true
  MakeInternals = false
  MapMode = 5
  Placement = pos=(0,0,0) rot=(1,0,0;1.5708rad)
  sketch-geometry (4):
    g0: LineSegment StartX=-44.6 StartY=41.2 StartZ=0 EndX=-44.6 EndY=36.4 EndZ=0
    g1: LineSegment StartX=-44.6 StartY=36.4 StartZ=0 EndX=-54.6 EndY=36.4 EndZ=0
    g2: LineSegment StartX=-54.6 StartY=36.4 StartZ=0 EndX=-50.4 EndY=41.2 EndZ=0
    g3: LineSegment StartX=-50.4 StartY=41.2 StartZ=0 EndX=-44.6 EndY=41.2 EndZ=0
  constraints (11):
    c: Vertical(g0)
    c: Coincident(g1,g0)
    c: Horizontal(g1)
    c: Coincident(g2,g1)
    c: Coincident(g3,g2)
    c: Coincident(g3,g0)
    c: Horizontal(g3)
    c: Coincident(g0,g-3)
    c: DistanceY(g0,g-4) = 0
    c: DistanceX(g3,g3) = 5.8
    c: DistanceX(g1,g1) = 10
FEATURE [Part::Extrusion] Extrude022  label="Extrude foro per filo CAM dx"
  Base = -> Sketch025
  Dir = (0,-1,2e-16)
  DirMode = 2
  FaceMakerClass = Part::FaceMakerBullseye
  FaceMakerMode = 3
  LengthFwd = 4.9
  LengthRev = 0
  Placement = pos=(0,6.95,0) rot=(0,0,1;0rad)
  Solid = true
  Symmetric = true
FEATURE [Part::Extrusion] Extrude023  label="Extrude foro per filo CAM sx"
  Base = -> Sketch025
  Dir = (0,-1,2e-16)
  DirMode = 2
  FaceMakerClass = Part::FaceMakerBullseye
  FaceMakerMode = 3
  LengthFwd = 4.9
  LengthRev = 0
  Placement = pos=(0,-6.95,0) rot=(0,0,1;0rad)
  Solid = true
  Symmetric = true
FEATURE [Sketcher::SketchObject] Sketch026  label="foro sotto anteriore M3x5x6"
  ArcFitTolerance = 1e-06
  AttachmentSupport = -> [XY_Plane]
  FullyConstrained = true
  MakeInternals = false
  MapMode = 5
  sketch-geometry (2):
    g0: LineSegment [constr] StartX=0 StartY=0 StartZ=0 EndX=-16.5 EndY=0 EndZ=0
    g1: Circle CenterX=-16.5 CenterY=0 CenterZ=0 NormalX=0 NormalY=0 NormalZ=1 AngleXU=0 Radius=2.5
  constraints (5):
    c: Distance(g0) = 16.5
    c: Coincident(g0,g-1)
    c: PointOnObject(g0,g-1)
    c: Diameter(g1) = 5
    c: Coincident(g0,g1)
FEATURE [Sketcher::SketchObject] Sketch027  label="foro sotto posteriore M3x5x6"
  ArcFitTolerance = 1e-06
  AttachmentSupport = -> [XY_Plane]
  ExternalGeometry = -> [Sketch]
  FullyConstrained = true
  MakeInternals = false
  MapMode = 5
  sketch-geometry (2):
    g0: LineSegment [constr] StartX=-82.8 StartY=2e-16 StartZ=0 EndX=-71.3 EndY=2e-16 EndZ=0
    g1: Circle CenterX=-71.3 CenterY=2e-16 CenterZ=0 NormalX=0 NormalY=0 NormalZ=1 AngleXU=0 Radius=2.5
  constraints (5):
    c: Distance(g0) = 11.5
    c: Coincident(g0,g-3)
    c: PointOnObject(g0,g-3)
    c: Diameter(g1) = 5
    c: Coincident(g1,g0)
FEATURE [Sketcher::SketchObject] Sketch029  label="fori sotto impugnatura"
  ArcFitTolerance = 1e-06
  AttachmentSupport = -> [XY_Plane]
  ExternalGeometry = -> [Sketch]
  FullyConstrained = true
  MakeInternals = false
  MapMode = 5
  sketch-geometry (15):
    g0: LineSegment [constr] StartX=-175.232 StartY=-1.83e-14 StartZ=0 EndX=-191.232 EndY=0 EndZ=0
    g1: Circle CenterX=-191.232 CenterY=0 CenterZ=0 NormalX=0 NormalY=0 NormalZ=1 AngleXU=0 Radius=3.95
    g2: LineSegment [constr] StartX=-175.232 StartY=-1.83e-14 StartZ=0 EndX=-204.275 EndY=0 EndZ=0
    g3: LineSegment StartX=-204.275 StartY=3.525 StartZ=0 EndX=-204.275 EndY=-3.525 EndZ=0
    g4: LineSegment StartX=-205.4 StartY=-4.65 StartZ=0 EndX=-206.65 EndY=-4.65 EndZ=0
    g5: LineSegment StartX=-207.775 StartY=-3.525 StartZ=0 EndX=-207.775 EndY=3.525 EndZ=0
    g6: LineSegment StartX=-206.65 StartY=4.65 StartZ=0 EndX=-205.4 EndY=4.65 EndZ=0
    g7: ArcOfCircle CenterX=-206.65 CenterY=3.525 CenterZ=0 NormalX=0 NormalY=0 NormalZ=1 AngleXU=0 Radius=1.125 StartAngle=1.5708 EndAngle=3.14159
    g8: GeomPoint [constr] X=-207.775 Y=4.65 Z=0
    g9: ArcOfCircle CenterX=-205.4 CenterY=3.525 CenterZ=0 NormalX=0 NormalY=0 NormalZ=1 AngleXU=0 Radius=1.125 StartAngle=0 EndAngle=1.5708
    g10: GeomPoint [constr] X=-204.275 Y=4.65 Z=0
    g11: ArcOfCircle CenterX=-205.4 CenterY=-3.525 CenterZ=0 NormalX=0 NormalY=0 NormalZ=1 AngleXU=0 Radius=1.125 StartAngle=4.71239 EndAngle=6.28319
    g12: GeomPoint [constr] X=-204.275 Y=-4.65 Z=0
    g13: ArcOfCircle CenterX=-206.65 CenterY=-3.525 CenterZ=0 NormalX=0 NormalY=0 NormalZ=1 AngleXU=0 Radius=1.125 StartAngle=3.14159 EndAngle=4.71239
    g14: GeomPoint [constr] X=-207.775 Y=-4.65 Z=0
  constraints (35):
    c: Distance(g0) = 16
    c: Coincident(g0,g-3)
    c: PointOnObject(g0,g-1)
    c: Diameter(g1) = 7.9
    c: Coincident(g1,g0)
    c: Coincident(g2,g0)
    c: PointOnObject(g2,g-1)
    c: Vertical(g3)
    c: Horizontal(g4)
    c: Vertical(g5)
    c: Horizontal(g6)
    c: DistanceY(g12,g10) = 9.3
    c: DistanceX(g8,g10) = 3.5
    c: Symmetric(g10,g12,g2)
    c: PointOnObject(g8,g5)
    c: PointOnObject(g8,g6)
    c: Tangent(g5,g7) = 1.5708
    c: Tangent(g6,g7) = 1.5708
    c: PointOnObject(g10,g3)
    c: PointOnObject(g10,g6)
    c: Tangent(g3,g9) = 1.5708
    c: Tangent(g6,g9) = 1.5708
    c: PointOnObject(g12,g3)
    c: PointOnObject(g12,g4)
    c: Tangent(g3,g11) = 1.5708
    c: Tangent(g4,g11) = 1.5708
    c: PointOnObject(g14,g4)
    c: PointOnObject(g14,g5)
    c: Tangent(g4,g13) = 1.5708
    c: Tangent(g5,g13) = 1.5708
    c: Equal(g7,g9)
    c: Equal(g9,g11)
    c: Equal(g11,g13)
    c: DistanceX(g6,g6) = 1.25
    c: DistanceX(g-5,g5) = 6.8
FEATURE [Sketcher::SketchObject] Sketch030  label="fori superiori per solenoide e oled"
  ArcFitTolerance = 1e-06
  AttachmentSupport = -> [XY_Plane]
  ExternalGeometry = -> [Sketch]
  FullyConstrained = true
  MakeInternals = false
  MapMode = 5
  sketch-geometry (33):
    g0: LineSegment [constr] StartX=-181.6 StartY=1.12e-14 StartZ=0 EndX=-169.91 EndY=0 EndZ=0
    g1: LineSegment [constr] StartX=-169.91 StartY=0 StartZ=0 EndX=-169.91 EndY=-2.6 EndZ=0
    g2: LineSegment [constr] StartX=-169.91 StartY=0 StartZ=0 EndX=-169.91 EndY=2.6 EndZ=0
    g3: LineSegment StartX=-169.91 StartY=4.975 StartZ=0 EndX=-169.91 EndY=8.225 EndZ=0
    g4: LineSegment StartX=-167.535 StartY=10.6 StartZ=0 EndX=-167.285 EndY=10.6 EndZ=0
    g5: LineSegment StartX=-164.91 StartY=8.225 StartZ=0 EndX=-164.91 EndY=4.975 EndZ=0
    g6: LineSegment StartX=-167.285 StartY=2.6 StartZ=0 EndX=-167.535 EndY=2.6 EndZ=0
    g7: LineSegment StartX=-169.91 StartY=-4.975 StartZ=0 EndX=-169.91 EndY=-8.225 EndZ=0
    g8: LineSegment StartX=-167.535 StartY=-10.6 StartZ=0 EndX=-167.285 EndY=-10.6 EndZ=0
    g9: LineSegment StartX=-164.91 StartY=-8.225 StartZ=0 EndX=-164.91 EndY=-4.975 EndZ=0
    g10: LineSegment StartX=-167.285 StartY=-2.6 StartZ=0 EndX=-167.535 EndY=-2.6 EndZ=0
    g11: ArcOfCircle CenterX=-167.535 CenterY=8.225 CenterZ=0 NormalX=0 NormalY=0 NormalZ=1 AngleXU=0 Radius=2.375 StartAngle=1.5708 EndAngle=3.14159
    g12: GeomPoint [constr] X=-169.91 Y=10.6 Z=0
    g13: ArcOfCircle CenterX=-167.285 CenterY=8.225 CenterZ=0 NormalX=0 NormalY=0 NormalZ=1 AngleXU=0 Radius=2.375 StartAngle=0 EndAngle=1.5708
    g14: GeomPoint [constr] X=-164.91 Y=10.6 Z=0
    g15: ArcOfCircle CenterX=-167.285 CenterY=4.975 CenterZ=0 NormalX=0 NormalY=0 NormalZ=1 AngleXU=0 Radius=2.375 StartAngle=4.71239 EndAngle=6.28319
    g16: GeomPoint [constr] X=-164.91 Y=2.6 Z=0
    g17: ArcOfCircle CenterX=-167.535 CenterY=4.975 CenterZ=0 NormalX=0 NormalY=0 NormalZ=1 AngleXU=0 Radius=2.375 StartAngle=3.14159 EndAngle=4.71239
    g18: GeomPoint [constr] X=-169.91 Y=2.6 Z=0
    g19: ArcOfCircle CenterX=-167.535 CenterY=-4.975 CenterZ=0 NormalX=0 NormalY=0 NormalZ=1 AngleXU=0 Radius=2.375 StartAngle=1.5708 EndAngle=3.14159
    g20: GeomPoint [constr] X=-169.91 Y=-2.6 Z=0
    g21: ArcOfCircle CenterX=-167.285 CenterY=-4.975 CenterZ=0 NormalX=0 NormalY=0 NormalZ=1 AngleXU=0 Radius=2.375 StartAngle=0 EndAngle=1.5708
    g22: GeomPoint [constr] X=-164.91 Y=-2.6 Z=0
    g23: ArcOfCircle CenterX=-167.285 CenterY=-8.225 CenterZ=0 NormalX=0 NormalY=0 NormalZ=1 AngleXU=0 Radius=2.375 StartAngle=4.71239 EndAngle=6.28319
    g24: GeomPoint [constr] X=-164.91 Y=-10.6 Z=0
    g25: ArcOfCircle CenterX=-167.535 CenterY=-8.225 CenterZ=0 NormalX=0 NormalY=0 NormalZ=1 AngleXU=0 Radius=2.375 StartAngle=3.14159 EndAngle=4.71239
    g26: GeomPoint [constr] X=-169.91 Y=-10.6 Z=0
    g27: LineSegment [constr] StartX=-181.6 StartY=1.12e-14 StartZ=0 EndX=-152.209 EndY=0 EndZ=0
    g28: LineSegment [constr] StartX=-181.6 StartY=1.12e-14 StartZ=0 EndX=-130.41 EndY=0 EndZ=0
    g29: LineSegment [constr] StartX=-152.209 StartY=0 StartZ=0 EndX=-152.209 EndY=6.95 EndZ=0
    g30: LineSegment [constr] StartX=-130.41 StartY=0 StartZ=0 EndX=-130.41 EndY=-6.95 EndZ=0
    g31: Circle CenterX=-152.209 CenterY=6.95 CenterZ=0 NormalX=0 NormalY=0 NormalZ=1 AngleXU=0 Radius=2.1
    g32: Circle CenterX=-130.41 CenterY=-6.95 CenterZ=0 NormalX=0 NormalY=0 NormalZ=1 AngleXU=0 Radius=2.1
  constraints (79):
    c: Distance(g0) = 11.69
    c: PointOnObject(g0,g-1)
    c: Coincident(g-4,g0)
    c: Distance(g1) = 2.6
    c: Coincident(g1,g0)
    c: Vertical(g1)
    c: Distance(g2) = 2.6
    c: Coincident(g2,g0)
    c: Vertical(g2)
    c: Distance(g18,g12) = 8
    c: Coincident(g18,g2)
    c: Vertical(g3)
    c: Distance(g14,g12) = 5
    c: Horizontal(g4)
    c: Distance(g16,g14) = 8
    c: Vertical(g5)
    c: Distance(g26,g20) = 8
    c: Coincident(g20,g1)
    c: Vertical(g7)
    c: Distance(g26,g24) = 5
    c: Horizontal(g8)
    c: Distance(g24,g22) = 8
    c: Vertical(g9)
    c: PointOnObject(g12,g3)
    c: PointOnObject(g12,g4)
    c: Tangent(g3,g11) = 1.5708
    c: Tangent(g4,g11) = 1.5708
    c: PointOnObject(g14,g5)
    c: PointOnObject(g14,g4)
    c: Tangent(g5,g13) = 1.5708
    c: Tangent(g4,g13) = 1.5708
    c: PointOnObject(g16,g5)
    c: PointOnObject(g16,g6)
    c: Tangent(g5,g15) = 1.5708
    c: Tangent(g6,g15) = 1.5708
    c: PointOnObject(g18,g3)
    c: PointOnObject(g18,g6)
    c: Tangent(g3,g17) = 1.5708
    c: Tangent(g6,g17) = 1.5708
    c: Equal(g11,g13)
    c: Equal(g13,g15)
    c: Equal(g15,g17)
    c: DistanceX(g4,g4) = 0.25
    c: PointOnObject(g20,g7)
    c: PointOnObject(g20,g10)
    c: Tangent(g7,g19) = -1.5708
    c: Tangent(g10,g19) = -1.5708
    c: PointOnObject(g22,g9)
    c: PointOnObject(g22,g10)
    c: Tangent(g9,g21) = -1.5708
    c: Tangent(g10,g21) = -1.5708
    c: PointOnObject(g24,g9)
    c: PointOnObject(g24,g8)
    c: Tangent(g9,g23) = -1.5708
    c: Tangent(g8,g23) = -1.5708
    c: PointOnObject(g26,g8)
    c: PointOnObject(g26,g7)
    c: Tangent(g8,g25) = -1.5708
    c: Tangent(g7,g25) = -1.5708
    c: Equal(g19,g21)
    c: Equal(g21,g23)
    c: Equal(g23,g25)
    c: DistanceX(g10,g10) = 0.25
    c: Distance(g27) = 29.391
    c: Coincident(g27,g0)
    c: PointOnObject(g27,g-1)
    c: Distance(g28) = 51.19
    c: Coincident(g28,g0)
    c: PointOnObject(g28,g-1)
    c: Distance(g29) = 6.95
    c: Coincident(g29,g27)
    c: Vertical(g29)
    c: Distance(g30) = 6.95
    c: Coincident(g30,g28)
    c: Vertical(g30)
    c: Diameter(g31) = 4.2
    c: Diameter(g32) = 4.2
    c: Coincident(g32,g30)
    c: Coincident(g31,g29)
FEATURE [Sketcher::SketchObject] Sketch031  label="fori inferiori switch pompa"
  ArcFitTolerance = 1e-06
  AttachmentSupport = -> [XY_Plane]
  ExternalGeometry = -> [Sketch]
  FullyConstrained = true
  MakeInternals = false
  MapMode = 5
  sketch-geometry (4):
    g0: LineSegment [constr] StartX=-57.2 StartY=1.9e-15 StartZ=0 EndX=-62.45 EndY=1.9e-15 EndZ=0
    g1: LineSegment [constr] StartX=-62.45 StartY=3.25 StartZ=0 EndX=-62.45 EndY=-3.25 EndZ=0
    g2: Circle CenterX=-62.45 CenterY=3.25 CenterZ=0 NormalX=0 NormalY=0 NormalZ=1 AngleXU=0 Radius=1.6
    g3: Circle CenterX=-62.45 CenterY=-3.25 CenterZ=0 NormalX=0 NormalY=0 NormalZ=1 AngleXU=0 Radius=1.6
  constraints (10):
    c: Distance(g0) = 5.25
    c: Coincident(g0,g-3)
    c: PointOnObject(g0,g-3)
    c: Vertical(g1)
    c: DistanceY(g1,g1) = 6.5
    c: Symmetric(g1,g1,g0)
    c: Diameter(g2) = 3.2
    c: Diameter(g3) = 3.2
    c: Coincident(g2,g1)
    c: Coincident(g3,g1)
FEATURE [Sketcher::SketchObject] Sketch032  label="spazio per PILA 18650"
  ArcFitTolerance = 1e-06
  AttachmentSupport = -> [XY_Plane]
  ExternalGeometry = -> [Sketch]
  FullyConstrained = true
  MakeInternals = false
  MapMode = 5
  sketch-geometry (2):
    g0: LineSegment [constr] StartX=-178.142 StartY=-1.74e-14 StartZ=0 EndX=-191.142 EndY=-1.83e-14 EndZ=0
    g1: Circle CenterX=-191.142 CenterY=-1.83e-14 CenterZ=0 NormalX=0 NormalY=0 NormalZ=1 AngleXU=0 Radius=10.5
  constraints (5):
    c: Distance(g0) = 13
    c: Coincident(g0,g-3)
    c: PointOnObject(g0,g-4)
    c: Diameter(g1) = 21
    c: Coincident(g1,g0)
FEATURE [Part::Extrusion] Extrude030  label="Extrude spazio per PILA 18650"
  Base = -> Sketch032
  Dir = (0,0,1)
  DirLink = -> Sketch [Edge45]
  DirMode = 2
  FaceMakerClass = Part::FaceMakerBullseye
  FaceMakerMode = 3
  LengthFwd = 76
  LengthRev = 0
  Placement = pos=(6,0,-72) rot=(0,0,1;0rad)
  Solid = true
  Symmetric = false
FEATURE [Sketcher::SketchObject] Sketch033  label="fermo per scheda micro"
  ArcFitTolerance = 1e-06
  AttachmentSupport = -> [XZ_Plane]
  ExternalGeometry = -> [Sketch]
  FullyConstrained = true
  MakeInternals = false
  MapMode = 5
  Placement = pos=(0,0,0) rot=(1,0,0;1.5708rad)
  sketch-geometry (12):
    g0: LineSegment StartX=-11.6 StartY=6 StartZ=0 EndX=-4 EndY=6 EndZ=0
    g1: LineSegment StartX=-4 StartY=6 StartZ=0 EndX=-4 EndY=36.4 EndZ=0
    g2: LineSegment StartX=-4 StartY=36.4 StartZ=0 EndX=-11.6 EndY=36.4 EndZ=0
    g3: LineSegment StartX=-11.6 StartY=36.4 StartZ=0 EndX=-11.6 EndY=6 EndZ=0
    g4: LineSegment StartX=-80.11 StartY=11.6 StartZ=0 EndX=-70.51 EndY=11.6 EndZ=0
    g5: LineSegment StartX=-70.51 StartY=11.6 StartZ=0 EndX=-70.51 EndY=6 EndZ=0
    g6: LineSegment StartX=-70.51 StartY=6 StartZ=0 EndX=-80.11 EndY=6 EndZ=0
    g7: LineSegment StartX=-80.11 StartY=6 StartZ=0 EndX=-80.11 EndY=11.6 EndZ=0
    g8: LineSegment StartX=-78.51 StartY=36.4 StartZ=0 EndX=-70.51 EndY=36.4 EndZ=0
    g9: LineSegment StartX=-70.51 StartY=36.4 StartZ=0 EndX=-70.51 EndY=30.8 EndZ=0
    g10: LineSegment StartX=-70.51 StartY=30.8 StartZ=0 EndX=-78.51 EndY=30.8 EndZ=0
    g11: LineSegment StartX=-78.51 StartY=30.8 StartZ=0 EndX=-78.51 EndY=36.4 EndZ=0
  constraints (33):
    c: Horizontal(g0)
    c: Coincident(g1,g0)
    c: Coincident(g2,g1)
    c: Horizontal(g2)
    c: Coincident(g3,g2)
    c: Coincident(g3,g0)
    c: Vertical(g3)
    c: DistanceX(g2,g2) = 7.6
    c: Coincident(g1,g-3)
    c: Coincident(g0,g-3)
    c: Horizontal(g4)
    c: Coincident(g5,g4)
    c: Vertical(g5)
    c: Coincident(g6,g5)
    c: Horizontal(g6)
    c: Coincident(g7,g6)
    c: Coincident(g7,g4)
    c: Vertical(g7)
    c: DistanceY(g5,g5) = 5.6
    c: DistanceX(g4,g4) = 9.6
    c: Coincident(g9,g8)
    c: Vertical(g9)
    c: Coincident(g10,g9)
    c: Horizontal(g10)
    c: Coincident(g11,g10)
    c: Coincident(g11,g8)
    c: Vertical(g11)
    c: DistanceY(g9,g9) = 5.6
    c: DistanceX(g10,g10) = 8
    c: Coincident(g4,g-4)
    c: DistanceX(g4,g10) = 1.6
    c: Horizontal(g8)
    c: DistanceY(g8,g1) = 0
FEATURE [Sketcher::SketchObject] Sketch034  label="buchi guida rail"
  ArcFitTolerance = 1e-06
  AttachmentSupport = -> [XY_Plane]
  ExternalGeometry = -> [Sketch]
  FullyConstrained = true
  MakeInternals = false
  MapMode = 5
  sketch-geometry (6):
    g0: LineSegment [constr] StartX=-100.8 StartY=9.1e-15 StartZ=0 EndX=-93.3 EndY=0 EndZ=0
    g1: LineSegment [constr] StartX=-93.3 StartY=0 StartZ=0 EndX=-73.3 EndY=0 EndZ=0
    g2: LineSegment [constr] StartX=-73.3 StartY=0 StartZ=0 EndX=-53.3 EndY=0 EndZ=0
    g3: Circle CenterX=-93.3 CenterY=0 CenterZ=0 NormalX=0 NormalY=0 NormalZ=1 AngleXU=0 Radius=2.5
    g4: Circle CenterX=-73.3 CenterY=0 CenterZ=0 NormalX=0 NormalY=0 NormalZ=1 AngleXU=0 Radius=2.5
    g5: Circle CenterX=-53.3 CenterY=0 CenterZ=0 NormalX=0 NormalY=0 NormalZ=1 AngleXU=0 Radius=2.5
  constraints (15):
    c: Distance(g0) = 7.5
    c: Coincident(g0,g-3)
    c: PointOnObject(g0,g-1)
    c: Distance(g1) = 20
    c: Coincident(g1,g0)
    c: PointOnObject(g1,g-1)
    c: Distance(g2) = 20
    c: Coincident(g2,g1)
    c: PointOnObject(g2,g-1)
    c: Diameter(g3) = 5
    c: Diameter(g4) = 5
    c: Diameter(g5) = 5
    c: Coincident(g3,g0)
    c: Coincident(g4,g1)
    c: Coincident(g5,g2)
FEATURE [Part::Extrusion] Extrude032  label="Extrude buchi guida rail"
  Base = -> Sketch034
  Dir = (0,0,1)
  DirMode = 2
  FaceMakerClass = Part::FaceMakerBullseye
  FaceMakerMode = 3
  LengthFwd = -6.2
  LengthRev = 0
  Placement = pos=(0,0,43.2) rot=(0,0,1;0rad)
  Solid = true
  Symmetric = false
FEATURE [Part::Extrusion] Extrude033  label="Extrude fori superiori per solenoide e oled001"
  Base = -> Sketch030
  Dir = (0,0,1)
  DirMode = 2
  FaceMakerClass = Part::FaceMakerBullseye
  FaceMakerMode = 3
  LengthFwd = -4.8
  LengthRev = 0
  Placement = pos=(0,0,41.2) rot=(0,0,1;0rad)
  Solid = true
  Symmetric = false
FEATURE [Part::Extrusion] Extrude034  label="Extrude fori sotto impugnatura001"
  Base = -> Sketch029
  Dir = (0,0,1)
  DirMode = 2
  FaceMakerClass = Part::FaceMakerBullseye
  FaceMakerMode = 3
  LengthFwd = 5
  LengthRev = 0
  Placement = pos=(0,0,-83) rot=(0,0,1;0rad)
  Solid = true
  Symmetric = false
FEATURE [Part::Extrusion] Extrude035  label="Extrude fori inferiori switch pompa001"
  Base = -> Sketch031
  Dir = (0,0,1)
  DirMode = 2
  FaceMakerClass = Part::FaceMakerBullseye
  FaceMakerMode = 3
  LengthFwd = 4
  LengthRev = 0
  Placement = pos=(0,0,-1.7) rot=(0,0,1;0rad)
  Solid = true
  Symmetric = false
FEATURE [Part::Extrusion] Extrude036  label="Extrude foro sotto posteriore M3x5x007"
  Base = -> Sketch027
  Dir = (0,0,1)
  DirMode = 2
  FaceMakerClass = Part::FaceMakerBullseye
  FaceMakerMode = 3
  LengthFwd = 6.2
  LengthRev = 0
  Placement = pos=(0,0,-9.6) rot=(0,0,1;0rad)
  Solid = true
  Symmetric = false
FEATURE [Part::Extrusion] Extrude037  label="Extrude foro sotto anteriore M3x5x007"
  Base = -> Sketch026
  Dir = (0,0,1)
  DirMode = 2
  FaceMakerClass = Part::FaceMakerBullseye
  FaceMakerMode = 3
  LengthFwd = 6.2
  LengthRev = 0
  Solid = true
  Symmetric = false
FEATURE [Sketcher::SketchObject] Sketch035  label="foro per fissaggio micro"
  ArcFitTolerance = 1e-06
  AttachmentSupport = -> [XZ_Plane]
  ExternalGeometry = -> [Sketch,Sketch033]
  FullyConstrained = true
  MakeInternals = false
  MapMode = 5
  Placement = pos=(0,0,0) rot=(1,0,0;1.5708rad)
  sketch-geometry (3):
    g0: Circle CenterX=-7.8 CenterY=21.2 CenterZ=0 NormalX=0 NormalY=0 NormalZ=1 AngleXU=0 Radius=1.6
    g1: GeomPoint [constr] X=-4 Y=21.2 Z=0
    g2: LineSegment [constr] StartX=-4 StartY=21.2 StartZ=0 EndX=-11.6 EndY=21.2 EndZ=0
  constraints (6):
    c: Diameter(g0) = 3.2
    c: Symmetric(g-3,g-3,g1)
    c: Coincident(g2,g1)
    c: Horizontal(g2)
    c: DistanceX(g-4,g2) = 0
    c: Symmetric(g2,g1,g0)
FEATURE [Part::Extrusion] Extrude038  label="Extrude foro per fissaggio micro"
  Base = -> Sketch035
  Dir = (0,-1,2e-16)
  DirMode = 2
  FaceMakerClass = Part::FaceMakerBullseye
  FaceMakerMode = 3
  LengthFwd = 3
  LengthRev = 0
  Placement = pos=(0,8.6,0) rot=(0,0,1;0rad)
  Solid = true
  Symmetric = false
FEATURE [Sketcher::SketchObject] Sketch036  label="supporto per alimentatore"
  ArcFitTolerance = 1e-06
  AttachmentSupport = -> [XZ_Plane]
  ExternalGeometry = -> [Sketch,Sketch016,Sketch022]
  FullyConstrained = true
  MakeInternals = false
  MapMode = 5
  Placement = pos=(0,0,0) rot=(1,0,0;1.5708rad)
  sketch-geometry (5):
    g0: LineSegment StartX=-211.843 StartY=-50.0944 StartZ=0 EndX=-211.843 EndY=-80.4316 EndZ=0
    g1: LineSegment StartX=-211.843 StartY=-50.0944 StartZ=0 EndX=-207.775 EndY=-41.3701 EndZ=0
    g2: LineSegment [constr] StartX=-209.443 StartY=-50.0944 StartZ=0 EndX=-209.443 EndY=-80.4316 EndZ=0
    g3: LineSegment StartX=-207.775 StartY=-41.3701 StartZ=0 EndX=-207.775 EndY=-80.4316 EndZ=0
    g4: LineSegment StartX=-211.843 StartY=-80.4316 StartZ=0 EndX=-207.775 EndY=-80.4316 EndZ=0
  constraints (15):
    c: Vertical(g0)
    c: Coincident(g1,g0)
    c: Vertical(g2)
    c: Tangent(g2,g-5)
    c: Coincident(g3,g1)
    c: Vertical(g3)
    c: DistanceY(g-3,g3) = -2
    c: Tangent(g1,g-8)
    c: DistanceY(g-3,g0) = -2
    c: Coincident(g4,g0)
    c: Coincident(g4,g3)
    c: Tangent(g0,g-6)
    c: DistanceY(g-3,g2) = -2
    c: DistanceY(g2,g0) = 0
    c: DistanceX(g-3,g3) = 6.8
FEATURE [Part::Extrusion] Extrude039  label="Extrude039 supporto alimentatore"
  Base = -> Sketch036
  Dir = (0,-1,2e-16)
  DirMode = 2
  FaceMakerClass = Part::FaceMakerBullseye
  FaceMakerMode = 3
  LengthFwd = 25.2
  LengthRev = 0
  Solid = true
  Symmetric = true
FEATURE [Sketcher::SketchObject] Sketch037  label="scavo per alimentatore"
  ArcFitTolerance = 1e-06
  AttachmentSupport = -> [XZ_Plane]
  ExternalGeometry = -> [Sketch036]
  FullyConstrained = true
  MakeInternals = false
  MapMode = 5
  Placement = pos=(0,0,0) rot=(1,0,0;1.5708rad)
  sketch-geometry (4):
    g0: LineSegment StartX=-209.575 StartY=-50.4316 StartZ=0 EndX=-209.575 EndY=-80.4316 EndZ=0
    g1: LineSegment StartX=-209.575 StartY=-50.4316 StartZ=0 EndX=-207.775 EndY=-50.4316 EndZ=0
    g2: LineSegment StartX=-207.775 StartY=-50.4316 StartZ=0 EndX=-207.775 EndY=-80.4316 EndZ=0
    g3: LineSegment StartX=-207.775 StartY=-80.4316 StartZ=0 EndX=-209.575 EndY=-80.4316 EndZ=0
  constraints (11):
    c: Vertical(g0)
    c: Coincident(g1,g0)
    c: Horizontal(g1)
    c: Coincident(g2,g1)
    c: Vertical(g2)
    c: Coincident(g3,g2)
    c: Coincident(g3,g0)
    c: Horizontal(g3)
    c: DistanceX(g1,g1) = 1.8
    c: Coincident(g2,g-3)
    c: DistanceY(g2,g2) = 30
FEATURE [Part::Extrusion] Extrude040  label="Extrude040 scavo alimentatore"
  Base = -> Sketch037
  Dir = (0,-1,2e-16)
  DirMode = 2
  FaceMakerClass = Part::FaceMakerBullseye
  FaceMakerMode = 3
  LengthFwd = 19.5
  LengthRev = 0
  Solid = true
  Symmetric = true
FEATURE [Part::Extrusion] Extrude031  label="Extrude fermo per scheda micro"
  Base = -> Sketch033
  Dir = (0,-1,2e-16)
  DirMode = 2
  FaceMakerClass = Part::FaceMakerBullseye
  FaceMakerMode = 3
  LengthFwd = 3
  LengthRev = 0
  Placement = pos=(0,8.6,0) rot=(0,0,1;0rad)
  Solid = true
  Symmetric = false
FEATURE [Sketcher::SketchObject] Sketch038  label="scavo driver solenoide"
  ArcFitTolerance = 1e-06
  AttachmentSupport = -> [XZ_Plane]
  ExternalGeometry = -> [Sketch,Sketch036]
  FullyConstrained = true
  MakeInternals = false
  MapMode = 5
  Placement = pos=(0,0,0) rot=(1,0,0;1.5708rad)
  sketch-geometry (7):
    g0: LineSegment StartX=-192.222 StartY=-8.0175 StartZ=0 EndX=-194.941 EndY=-6.74965 EndZ=0
    g1: LineSegment StartX=-194.941 StartY=-6.74965 StartZ=0 EndX=-212.269 EndY=-43.9083 EndZ=0
    g2: LineSegment StartX=-192.222 StartY=-8.0175 StartZ=0 EndX=-188.779 EndY=-9.62345 EndZ=0
    g3: LineSegment StartX=-188.779 StartY=-9.62345 StartZ=0 EndX=-205.357 EndY=-45.1761 EndZ=0
    g4: LineSegment StartX=-205.357 StartY=-45.1761 StartZ=0 EndX=-209.55 EndY=-45.1761 EndZ=0
    g5: LineSegment [constr] StartX=-212.269 StartY=-43.9083 StartZ=0 EndX=-209.55 EndY=-45.1761 EndZ=0
    g6: LineSegment StartX=-212.269 StartY=-43.9083 StartZ=0 EndX=-209.55 EndY=-45.1761 EndZ=0
  constraints (20):
    c: Coincident(g1,g0)
    c: Coincident(g3,g2)
    c: Coincident(g4,g3)
    c: Distance(g2) = 3.8
    c: Distance(g1) = 41
    c: Coincident(g5,g1)
    c: Distance(g5) = 3
    c: Perpendicular(g5,g-3)
    c: Parallel(g1,g-3)
    c: Perpendicular(g1,g0)
    c: Distance(g0) = 3
    c: Coincident(g6,g1)
    c: Parallel(g3,g-3)
    c: Perpendicular(g2,g3)
    c: Coincident(g2,g0)
    c: Perpendicular(g-4,g4)
    c: PointOnObject(g5,g-3)
    c: Distance(g-3,g5) = 9.6
    c: Coincident(g4,g5)
    c: Coincident(g6,g4)
FEATURE [Part::Extrusion] Extrude041  label="Extrude scavo driver solenoide"
  Base = -> Sketch038
  Dir = (0,-1,2e-16)
  DirMode = 2
  FaceMakerClass = Part::FaceMakerBullseye
  FaceMakerMode = 3
  LengthFwd = 20.6
  LengthRev = 0
  Solid = true
  Symmetric = true
FEATURE [Sketcher::SketchObject] Sketch039  label="scavo per cavo usb per micro"
  ArcFitTolerance = 1e-06
  AttachmentSupport = -> [XZ_Plane]
  ExternalGeometry = -> [Sketch,Sketch016]
  FullyConstrained = true
  MakeInternals = false
  MapMode = 5
  Placement = pos=(0,0,0) rot=(1,0,0;1.5708rad)
  sketch-geometry (4):
    g0: LineSegment StartX=-82.51 StartY=36.4 StartZ=0 EndX=-74.51 EndY=36.4 EndZ=0
    g1: LineSegment StartX=-74.51 StartY=36.4 StartZ=0 EndX=-74.51 EndY=30.8 EndZ=0
    g2: LineSegment StartX=-74.51 StartY=30.8 StartZ=0 EndX=-82.51 EndY=30.8 EndZ=0
    g3: LineSegment StartX=-82.51 StartY=30.8 StartZ=0 EndX=-82.51 EndY=36.4 EndZ=0
  constraints (11):
    c: Coincident(g1,g0)
    c: Vertical(g1)
    c: Coincident(g2,g1)
    c: Horizontal(g2)
    c: Coincident(g3,g2)
    c: Coincident(g3,g0)
    c: Vertical(g3)
    c: Tangent(g0,g-3)
    c: Tangent(g2,g-4)
    c: Tangent(g3,g-4)
    c: Tangent(g1,g-4)
FEATURE [Part::Extrusion] Extrude042  label="Extrude scavo per cavo usb per micro"
  Base = -> Sketch039
  Dir = (0,-1,2e-16)
  DirMode = 2
  FaceMakerClass = Part::FaceMakerBullseye
  FaceMakerMode = 3
  LengthFwd = 11.2
  LengthRev = 0
  Solid = true
  Symmetric = true
FEATURE [Sketcher::SketchObject] Sketch040  label="scavo saldature alimentatore connettore 5v"
  ArcFitTolerance = 1e-06
  AttachmentSupport = -> [XZ_Plane]
  ExternalGeometry = -> [Sketch037]
  FullyConstrained = true
  MakeInternals = false
  MapMode = 5
  Placement = pos=(0,0,0) rot=(1,0,0;1.5708rad)
  sketch-geometry (4):
    g0: LineSegment StartX=-211.175 StartY=-52.4316 StartZ=0 EndX=-211.175 EndY=-56.4316 EndZ=0
    g1: LineSegment StartX=-211.175 StartY=-52.4316 StartZ=0 EndX=-209.575 EndY=-52.4316 EndZ=0
    g2: LineSegment StartX=-209.575 StartY=-52.4316 StartZ=0 EndX=-209.575 EndY=-56.4316 EndZ=0
    g3: LineSegment StartX=-209.575 StartY=-56.4316 StartZ=0 EndX=-211.175 EndY=-56.4316 EndZ=0
  constraints (11):
    c: Vertical(g0)
    c: Coincident(g1,g0)
    c: Horizontal(g1)
    c: Coincident(g2,g1)
    c: Coincident(g3,g2)
    c: Coincident(g3,g0)
    c: Horizontal(g3)
    c: DistanceX(g1,g1) = 1.6
    c: DistanceY(g2,g2) = 4
    c: Tangent(g2,g-3)
    c: DistanceY(g1,g-3) = 2
FEATURE [Part::Extrusion] Extrude043  label="Extrude scavo saldature alimentatore connettore 5v"
  Base = -> Sketch040
  Dir = (0,-1,2e-16)
  DirMode = 2
  FaceMakerClass = Part::FaceMakerBullseye
  FaceMakerMode = 3
  LengthFwd = 8
  LengthRev = 0
  Solid = true
  Symmetric = true
FEATURE [Sketcher::SketchObject] Sketch041  label="scavo saldature alimentatore connettore 5v verticali"
  ArcFitTolerance = 1e-06
  AttachmentSupport = -> [XZ_Plane]
  ExternalGeometry = -> [Sketch037]
  FullyConstrained = true
  MakeInternals = false
  MapMode = 5
  Placement = pos=(0,0,0) rot=(1,0,0;1.5708rad)
  sketch-geometry (4):
    g0: LineSegment StartX=-211.175 StartY=-53.6316 StartZ=0 EndX=-209.575 EndY=-53.6316 EndZ=0
    g1: LineSegment StartX=-209.575 StartY=-53.6316 StartZ=0 EndX=-209.575 EndY=-76.6316 EndZ=0
    g2: LineSegment StartX=-209.575 StartY=-76.6316 StartZ=0 EndX=-211.175 EndY=-76.6316 EndZ=0
    g3: LineSegment StartX=-211.175 StartY=-76.6316 StartZ=0 EndX=-211.175 EndY=-53.6316 EndZ=0
  constraints (11):
    c: Horizontal(g0)
    c: Coincident(g1,g0)
    c: Coincident(g2,g1)
    c: Horizontal(g2)
    c: Coincident(g3,g2)
    c: Coincident(g3,g0)
    c: Vertical(g3)
    c: DistanceY(g3,g3) = 23
    c: DistanceX(g0,g0) = 1.6
    c: Tangent(g1,g-3)
    c: DistanceY(g0,g-3) = 3.2
FEATURE [Part::Extrusion] Extrude044  label="Extrude scavo saldature alimentatore connettore 5v verticali"
  Base = -> Sketch041
  Dir = (0,-1,2e-16)
  DirMode = 2
  FaceMakerClass = Part::FaceMakerBullseye
  FaceMakerMode = 3
  LengthFwd = 3.2
  LengthRev = 0
  Placement = pos=(0,8.3,0) rot=(0,0,1;0rad)
  Solid = true
  Symmetric = false
FEATURE [Sketcher::SketchObject] Sketch042  label="fermi per driver solenoide e alimentatore"
  ArcFitTolerance = 1e-06
  AttachmentSupport = -> [XZ_Plane]
  ExternalGeometry = -> [Sketch036,Sketch037,Sketch,Sketch038]
  FullyConstrained = true
  MakeInternals = false
  MapMode = 5
  Placement = pos=(0,0,0) rot=(1,0,0;1.5708rad)
  sketch-geometry (27):
    g0: LineSegment StartX=-200.506 StartY=-25.7811 StartZ=0 EndX=-201.436 EndY=-27.775 EndZ=0
    g1: LineSegment StartX=-201.436 StartY=-27.775 StartZ=0 EndX=-199.442 EndY=-28.7048 EndZ=0
    g2: LineSegment StartX=-199.442 StartY=-28.7048 StartZ=0 EndX=-198.512 EndY=-26.7109 EndZ=0
    g3: LineSegment StartX=-198.512 StartY=-26.7109 StartZ=0 EndX=-200.506 EndY=-25.7811 EndZ=0
    g4: LineSegment StartX=-201.28 StartY=-23.6549 StartZ=0 EndX=-203.562 EndY=-28.5489 EndZ=0
    g5: LineSegment StartX=-203.562 StartY=-28.5489 StartZ=0 EndX=-200.118 EndY=-30.1549 EndZ=0
    g6: LineSegment StartX=-197.992 StartY=-29.381 StartZ=0 EndX=-197.062 EndY=-27.3871 EndZ=0
    g7: LineSegment StartX=-197.836 StartY=-25.2608 StartZ=0 EndX=-201.28 EndY=-23.6549 EndZ=0
    g8: LineSegment [constr] StartX=-198.668 StartY=-30.8311 StartZ=0 EndX=-197.992 EndY=-29.381 EndZ=0
    g9: LineSegment [constr] StartX=-198.668 StartY=-30.8311 StartZ=0 EndX=-200.118 EndY=-30.1549 EndZ=0
    g10: ArcOfCircle CenterX=-198.512 CenterY=-26.7109 CenterZ=0 NormalX=0 NormalY=0 NormalZ=1 AngleXU=0 Radius=1.6 StartAngle=5.84685 EndAngle=7.41765
    g11: GeomPoint [constr] X=-196.386 Y=-25.937 Z=0
    g12: ArcOfCircle CenterX=-199.442 CenterY=-28.7048 CenterZ=0 NormalX=0 NormalY=0 NormalZ=1 AngleXU=0 Radius=1.6 StartAngle=4.27606 EndAngle=5.84685
    g13: GeomPoint [constr] X=-198.668 Y=-30.8311 Z=0
    g14: LineSegment StartX=-207.775 StartY=-46.8316 StartZ=0 EndX=-207.775 EndY=-50.8316 EndZ=0
    g15: LineSegment StartX=-207.775 StartY=-46.8316 StartZ=0 EndX=-203.775 EndY=-46.8316 EndZ=0
    g16: LineSegment StartX=-203.775 StartY=-46.8316 StartZ=0 EndX=-203.775 EndY=-50.8316 EndZ=0
    g17: LineSegment StartX=-207.775 StartY=-50.8316 StartZ=0 EndX=-203.775 EndY=-50.8316 EndZ=0
    g18: LineSegment StartX=-209.375 StartY=-52.4316 StartZ=0 EndX=-203.775 EndY=-52.4316 EndZ=0
    g19: LineSegment StartX=-202.175 StartY=-50.8316 StartZ=0 EndX=-202.175 EndY=-46.8316 EndZ=0
    g20: LineSegment StartX=-203.775 StartY=-45.2316 StartZ=0 EndX=-209.375 EndY=-45.2316 EndZ=0
    g21: LineSegment StartX=-209.375 StartY=-45.2316 StartZ=0 EndX=-209.375 EndY=-52.4316 EndZ=0
    g22: ArcOfCircle CenterX=-203.775 CenterY=-46.8316 CenterZ=0 NormalX=0 NormalY=0 NormalZ=1 AngleXU=0 Radius=1.6 StartAngle=1.8e-15 EndAngle=1.5708
    g23: GeomPoint [constr] X=-202.175 Y=-45.2316 Z=0
    g24: ArcOfCircle CenterX=-203.775 CenterY=-50.8316 CenterZ=0 NormalX=0 NormalY=0 NormalZ=1 AngleXU=0 Radius=1.6 StartAngle=4.71239 EndAngle=6.28319
    g25: GeomPoint [constr] X=-202.175 Y=-52.4316 Z=0
    g26: LineSegment [constr] StartX=-207.775 StartY=-50.4316 StartZ=0 EndX=-207.775 EndY=-50.8316 EndZ=0
  constraints (69):
    c: Coincident(g1,g0)
    c: Coincident(g2,g1)
    c: Coincident(g3,g2)
    c: Coincident(g3,g0)
    c: Parallel(g0,g2)
    c: Perpendicular(g3,g0)
    c: Perpendicular(g1,g0)
    c: Coincident(g5,g4)
    c: Coincident(g7,g4)
    c: Distance(g3) = 2.2
    c: Distance(g2) = 2.2
    c: Parallel(g6,g2)
    c: Parallel(g6,g4)
    c: Perpendicular(g5,g6)
    c: Perpendicular(g7,g6)
    c: Distance(g13,g11) = 5.4
    c: Distance(g5,g13) = 5.4
    c: Coincident(g9,g8)
    c: Distance(g8) = 1.6
    c: Distance(g9) = 1.6
    c: Perpendicular(g9,g8)
    c: Parallel(g8,g6)
    c: Coincident(g8,g13)
    c: Distance(g8,g1) = 1.6
    c: Distance(g9,g1) = 1.6
    c: Tangent(g0,g-5)
    c: Distance(g0,g-6) = 19.2
    c: PointOnObject(g11,g7)
    c: PointOnObject(g11,g6)
    c: Tangent(g7,g10) = -1.5708
    c: Tangent(g6,g10) = -1.5708
    c: PointOnObject(g13,g5)
    c: Tangent(g5,g12) = -1.5708
    c: Tangent(g6,g12) = -1.5708
    c: Equal(g10,g12)
    c: Coincident(g10,g2)
    c: Vertical(g14)
    c: Coincident(g15,g14)
    c: Horizontal(g15)
    c: Coincident(g16,g15)
    c: Vertical(g16)
    c: Coincident(g17,g14)
    c: Coincident(g17,g16)
    c: Horizontal(g17)
    c: Distance(g16) = 4
    c: Distance(g15) = 4
    c: Horizontal(g18)
    c: Vertical(g19)
    c: Horizontal(g20)
    c: Coincident(g21,g20)
    c: Coincident(g21,g18)
    c: Vertical(g21)
    c: Distance(g20,g23) = 7.2
    c: Distance(g25,g23) = 7.2
    c: DistanceY(g18,g14) = 1.6
    c: DistanceX(g18,g14) = 1.6
    c: PointOnObject(g23,g20)
    c: PointOnObject(g23,g19)
    c: Tangent(g20,g22) = -1.5708
    c: Tangent(g19,g22) = -1.5708
    c: PointOnObject(g25,g19)
    c: Tangent(g18,g24) = -1.5708
    c: Tangent(g19,g24) = -1.5708
    c: Equal(g22,g24)
    c: Coincident(g22,g15)
    c: Vertical(g26)
    c: Distance(g26) = 0.4
    c: Coincident(g26,g-4)
    c: Coincident(g14,g26)
FEATURE [Part::Extrusion] Extrude045  label="Extrude fermi per driver solenoide e alimentatore"
  Base = -> Sketch042
  Dir = (0,-1,2e-16)
  DirMode = 2
  FaceMakerClass = Part::FaceMakerBullseye
  FaceMakerMode = 3
  LengthFwd = 25.2
  LengthRev = 0
  Solid = true
  Symmetric = true
FEATURE [Sketcher::SketchObject] Sketch043  label="scavo pulizia fermo alimentatore"
  ArcFitTolerance = 1e-06
  AttachmentSupport = -> [XZ_Plane]
  ExternalGeometry = -> [Sketch042,Sketch036,Sketch037]
  FullyConstrained = true
  MakeInternals = false
  MapMode = 5
  Placement = pos=(0,0,0) rot=(1,0,0;1.5708rad)
  sketch-geometry (6):
    g0: LineSegment StartX=-209.375 StartY=-52.4316 StartZ=0 EndX=-209.375 EndY=-50.4316 EndZ=0
    g1: LineSegment StartX=-209.375 StartY=-50.4316 StartZ=0 EndX=-207.775 EndY=-50.4316 EndZ=0
    g2: LineSegment StartX=-207.775 StartY=-50.4316 StartZ=0 EndX=-207.775 EndY=-45.2316 EndZ=0
    g3: LineSegment StartX=-207.775 StartY=-45.2316 StartZ=0 EndX=-202.175 EndY=-45.2316 EndZ=0
    g4: LineSegment StartX=-202.175 StartY=-45.2316 StartZ=0 EndX=-202.175 EndY=-52.4316 EndZ=0
    g5: LineSegment StartX=-202.175 StartY=-52.4316 StartZ=0 EndX=-209.375 EndY=-52.4316 EndZ=0
  constraints (13):
    c: Vertical(g0)
    c: Coincident(g1,g0)
    c: Coincident(g2,g1)
    c: Coincident(g3,g2)
    c: Coincident(g4,g3)
    c: Coincident(g5,g4)
    c: Coincident(g5,g0)
    c: Horizontal(g5)
    c: Coincident(g0,g-6)
    c: Tangent(g1,g-8)
    c: Tangent(g2,g-4)
    c: Tangent(g3,g-7)
    c: Tangent(g4,g-3)
FEATURE [Part::Extrusion] Extrude046  label="Extrude scavo pulizia fermo alimentatore"
  Base = -> Sketch043
  Dir = (0,-1,2e-16)
  DirMode = 2
  FaceMakerClass = Part::FaceMakerBullseye
  FaceMakerMode = 3
  LengthFwd = 19.5
  LengthRev = 0
  Solid = true
  Symmetric = true
FEATURE [Sketcher::SketchObject] Sketch044  label="buchini per fissaggio oled"
  ArcFitTolerance = 1e-06
  AttachmentSupport = -> [YZ_Plane]
  ExternalGeometry = -> [Sketch]
  FullyConstrained = true
  MakeInternals = false
  MapMode = 5
  Placement = pos=(0,0,0) rot=(0.57735,0.57735,0.57735;2.0944rad)
  sketch-geometry (5):
    g0: LineSegment [constr] StartX=1.5e-14 StartY=67.3588 StartZ=0 EndX=0 EndY=64.3588 EndZ=0
    g1: LineSegment [constr] StartX=0 StartY=64.3588 StartZ=0 EndX=10.4 EndY=64.3588 EndZ=0
    g2: LineSegment [constr] StartX=0 StartY=64.3588 StartZ=0 EndX=-10.4 EndY=64.3588 EndZ=0
    g3: Circle CenterX=10.4 CenterY=64.3588 CenterZ=0 NormalX=0 NormalY=0 NormalZ=1 AngleXU=0 Radius=1.5
    g4: Circle CenterX=-10.4 CenterY=64.3588 CenterZ=0 NormalX=0 NormalY=0 NormalZ=1 AngleXU=0 Radius=1.5
  constraints (13):
    c: Distance(g0) = 3
    c: PointOnObject(g0,g-2)
    c: Coincident(g1,g0)
    c: Horizontal(g1)
    c: Coincident(g2,g0)
    c: Horizontal(g2)
    c: DistanceX(g1,g1) = 10.4
    c: Coincident(g3,g1)
    c: Diameter(g4) = 3
    c: Coincident(g4,g2)
    c: Coincident(g0,g-7)
    c: Equal(g1,g2)
    c: Equal(g4,g3)
FEATURE [Part::Extrusion] Extrude047  label="Extrude buchini per fissaggio oled"
  Base = -> Sketch044
  Dir = (1,0,0)
  DirMode = 2
  FaceMakerClass = Part::FaceMakerBullseye
  FaceMakerMode = 3
  LengthFwd = 10
  LengthRev = 0
  Placement = pos=(-186,0,0) rot=(0,0,1;0rad)
  Solid = true
  Symmetric = false
FEATURE [Sketcher::SketchObject] Sketch046  label="scavo 5x5 neopixel"
  ArcFitTolerance = 1e-06
  AttachmentSupport = -> [YZ_Plane002]
  FullyConstrained = true
  MakeInternals = false
  MapMode = 5
  Placement = pos=(0,0,0) rot=(0.57735,0.57735,0.57735;2.0944rad)
  sketch-geometry (4):
    g0: LineSegment StartX=-2.7 StartY=2.7 StartZ=0 EndX=2.7 EndY=2.7 EndZ=0
    g1: LineSegment StartX=2.7 StartY=2.7 StartZ=0 EndX=2.7 EndY=-2.7 EndZ=0
    g2: LineSegment StartX=2.7 StartY=-2.7 StartZ=0 EndX=-2.7 EndY=-2.7 EndZ=0
    g3: LineSegment StartX=-2.7 StartY=-2.7 StartZ=0 EndX=-2.7 EndY=2.7 EndZ=0
  constraints (11):
    c: Horizontal(g0)
    c: Coincident(g1,g0)
    c: Vertical(g1)
    c: Coincident(g2,g1)
    c: Horizontal(g2)
    c: Coincident(g3,g2)
    c: Coincident(g3,g0)
    c: Vertical(g3)
    c: DistanceX(g0,g0) = 5.4
    c: DistanceY(g1,g1) = 5.4
    c: Symmetric(g0,g1,g-1)
FEATURE [Sketcher::SketchObject] Sketch047  label="scavo 10x10 neopixel corpo"
  ArcFitTolerance = 1e-06
  AttachmentOffset = pos=(0,0,1) rot=(0,0,1;0rad)
  AttachmentSupport = -> [YZ_Plane002]
  FullyConstrained = true
  MakeInternals = false
  MapMode = 5
  Placement = pos=(1,0,0) rot=(0.57735,0.57735,0.57735;2.0944rad)
  sketch-geometry (4):
    g0: LineSegment StartX=-5 StartY=5.1 StartZ=0 EndX=5 EndY=5.1 EndZ=0
    g1: LineSegment StartX=5 StartY=5.1 StartZ=0 EndX=5 EndY=-5.1 EndZ=0
    g2: LineSegment StartX=5 StartY=-5.1 StartZ=0 EndX=-5 EndY=-5.1 EndZ=0
    g3: LineSegment StartX=-5 StartY=-5.1 StartZ=0 EndX=-5 EndY=5.1 EndZ=0
  constraints (11):
    c: Horizontal(g0)
    c: Coincident(g1,g0)
    c: Vertical(g1)
    c: Coincident(g2,g1)
    c: Horizontal(g2)
    c: Coincident(g3,g2)
    c: Coincident(g3,g0)
    c: Vertical(g3)
    c: DistanceX(g0,g0) = 10
    c: DistanceY(g1,g1) = 10.2
    c: Symmetric(g0,g2,g-1)
FEATURE [Sketcher::SketchObject] Sketch048  label="buco per perno blocco neopixel"
  ArcFitTolerance = 1e-06
  AttachmentSupport = -> [XZ_Plane002]
  FullyConstrained = true
  MakeInternals = false
  MapMode = 5
  Placement = pos=(0,0,0) rot=(1,0,0;1.5708rad)
  sketch-geometry (4):
    g0: LineSegment StartX=3 StartY=1.2 StartZ=0 EndX=3 EndY=-1.2 EndZ=0
    g1: LineSegment StartX=3 StartY=-1.2 StartZ=0 EndX=5.4 EndY=-1.2 EndZ=0
    g2: LineSegment StartX=5.4 StartY=-1.2 StartZ=0 EndX=5.4 EndY=1.2 EndZ=0
    g3: LineSegment StartX=5.4 StartY=1.2 StartZ=0 EndX=3 EndY=1.2 EndZ=0
  constraints (11):
    c: Coincident(g1,g0)
    c: Horizontal(g1)
    c: Coincident(g2,g1)
    c: Vertical(g2)
    c: Coincident(g3,g2)
    c: Coincident(g3,g0)
    c: Horizontal(g3)
    c: DistanceX(g1,g1) = 2.4
    c: DistanceY(g2,g2) = 2.4
    c: Symmetric(g0,g0,g-1)
    c: DistanceX(g-1,g0) = 3
FEATURE [Sketcher::SketchObject] Sketch045  label="blocco principale per neopixel"
  ArcFitTolerance = 1e-06
  AttachmentSupport = -> [XZ_Plane002]
  ExternalGeometry = -> [Sketch048]
  FullyConstrained = true
  MakeInternals = false
  MapMode = 5
  Placement = pos=(0,0,0) rot=(1,0,0;1.5708rad)
  sketch-geometry (6):
    g0: LineSegment StartX=0 StartY=5.1 StartZ=0 EndX=0 EndY=-5.1 EndZ=0
    g1: LineSegment StartX=0 StartY=-5.1 StartZ=0 EndX=3 EndY=-5.1 EndZ=0
    g2: LineSegment StartX=7 StartY=-1.1 StartZ=0 EndX=7 EndY=5.1 EndZ=0
    g3: LineSegment StartX=7 StartY=5.1 StartZ=0 EndX=0 EndY=5.1 EndZ=0
    g4: ArcOfCircle CenterX=3 CenterY=-1.1 CenterZ=0 NormalX=0 NormalY=0 NormalZ=1 AngleXU=0 Radius=4 StartAngle=4.71239 EndAngle=6.28319
    g5: GeomPoint [constr] X=7 Y=-5.1 Z=0
  constraints (15):
    c: Vertical(g0)
    c: Coincident(g1,g0)
    c: Horizontal(g1)
    c: Vertical(g2)
    c: Coincident(g3,g2)
    c: Coincident(g3,g0)
    c: Horizontal(g3)
    c: DistanceY(g0,g0) = 10.2
    c: Symmetric(g0,g0,g-1)
    c: DistanceX(g3,g3) = 7
    c: PointOnObject(g5,g2)
    c: PointOnObject(g5,g1)
    c: Tangent(g2,g4) = -1.5708
    c: Tangent(g1,g4) = -1.5708
    c: DistanceX(g-3,g1) = 0
FEATURE [Sketcher::SketchObject] Sketch049  label="rinforzi esterni per corpo neopoixel"
  ArcFitTolerance = 1e-06
  AttachmentSupport = -> [XZ_Plane002]
  ExternalGeometry = -> [Sketch045]
  FullyConstrained = true
  MakeInternals = false
  MapMode = 5
  Placement = pos=(0,0,0) rot=(1,0,0;1.5708rad)
  sketch-geometry (8):
    g0: LineSegment StartX=1 StartY=-4.1 StartZ=0 EndX=2 EndY=-4.1 EndZ=0
    g1: LineSegment StartX=2 StartY=-4.1 StartZ=0 EndX=2 EndY=-5.1 EndZ=0
    g2: LineSegment StartX=2 StartY=-5.1 StartZ=0 EndX=1 EndY=-5.1 EndZ=0
    g3: LineSegment StartX=1 StartY=-5.1 StartZ=0 EndX=1 EndY=-4.1 EndZ=0
    g4: LineSegment StartX=1 StartY=5.1 StartZ=0 EndX=2 EndY=5.1 EndZ=0
    g5: LineSegment StartX=2 StartY=5.1 StartZ=0 EndX=2 EndY=4.1 EndZ=0
    g6: LineSegment StartX=2 StartY=4.1 StartZ=0 EndX=1 EndY=4.1 EndZ=0
    g7: LineSegment StartX=1 StartY=4.1 StartZ=0 EndX=1 EndY=5.1 EndZ=0
  constraints (24):
    c: Horizontal(g0)
    c: Coincident(g1,g0)
    c: Vertical(g1)
    c: Coincident(g2,g1)
    c: Horizontal(g2)
    c: Coincident(g3,g2)
    c: Coincident(g3,g0)
    c: Vertical(g3)
    c: Horizontal(g4)
    c: Coincident(g5,g4)
    c: Vertical(g5)
    c: Coincident(g6,g5)
    c: Horizontal(g6)
    c: Coincident(g7,g6)
    c: Coincident(g7,g4)
    c: Vertical(g7)
    c: DistanceX(g4,g4) = 1
    c: DistanceY(g5,g5) = 1
    c: DistanceX(g0,g0) = 1
    c: DistanceY(g1,g1) = 1
    c: DistanceX(g-3,g4) = 1
    c: DistanceY(g-3,g4) = 0
    c: DistanceX(g-4,g2) = 1
    c: DistanceY(g2,g-4) = 0
FEATURE [Sketcher::SketchObject] Sketch052  label="scavo saldature driver solenoide"
  ArcFitTolerance = 1e-06
  AttachmentSupport = -> [XZ_Plane]
  ExternalGeometry = -> [Sketch038]
  FullyConstrained = true
  MakeInternals = false
  MapMode = 5
  Placement = pos=(0,0,0) rot=(1,0,0;1.5708rad)
  sketch-geometry (4):
    g0: LineSegment StartX=-195.304 StartY=-6.5806 StartZ=0 EndX=-196.994 EndY=-10.2058 EndZ=0
    g1: LineSegment StartX=-196.994 StartY=-10.2058 StartZ=0 EndX=-196.632 EndY=-10.3749 EndZ=0
    g2: LineSegment StartX=-196.632 StartY=-10.3749 StartZ=0 EndX=-194.941 EndY=-6.74965 EndZ=0
    g3: LineSegment StartX=-194.941 StartY=-6.74965 StartZ=0 EndX=-195.304 EndY=-6.5806 EndZ=0
  constraints (11):
    c: Coincident(g1,g0)
    c: Coincident(g2,g1)
    c: Coincident(g3,g2)
    c: Coincident(g3,g0)
    c: Parallel(g2,g0)
    c: Perpendicular(g2,g3)
    c: Perpendicular(g1,g2,g1) = 1.5708
    c: Parallel(g2,g-3)
    c: Distance(g2) = 4
    c: Distance(g3) = 0.4
    c: Coincident(g2,g-3)
FEATURE [Part::Extrusion] Extrude055  label="Extrude scavo saldature driver solenoide"
  Base = -> Sketch052
  Dir = (0,-1,2e-16)
  DirMode = 2
  FaceMakerClass = Part::FaceMakerBullseye
  FaceMakerMode = 3
  LengthFwd = 6
  LengthRev = 0
  Solid = true
  Symmetric = true
FEATURE [Sketcher::SketchObject] Sketch053  label="scavo saldature rumble"
  ArcFitTolerance = 1e-06
  AttachmentSupport = -> [XZ_Plane]
  ExternalGeometry = -> [Sketch019]
  FullyConstrained = true
  MakeInternals = false
  MapMode = 5
  Placement = pos=(0,0,0) rot=(1,0,0;1.5708rad)
  sketch-geometry (4):
    g0: LineSegment StartX=-164.507 StartY=-41.6446 StartZ=0 EndX=-165.743 EndY=-45.4488 EndZ=0
    g1: LineSegment StartX=-165.743 StartY=-45.4488 StartZ=0 EndX=-164.602 EndY=-45.8196 EndZ=0
    g2: LineSegment StartX=-164.602 StartY=-45.8196 StartZ=0 EndX=-163.366 EndY=-42.0154 EndZ=0
    g3: LineSegment StartX=-163.366 StartY=-42.0154 StartZ=0 EndX=-164.507 EndY=-41.6446 EndZ=0
  constraints (11):
    c: Coincident(g1,g0)
    c: Coincident(g2,g1)
    c: Coincident(g3,g2)
    c: Coincident(g3,g0)
    c: Parallel(g0,g2)
    c: Perpendicular(g3,g0)
    c: Perpendicular(g1,g0)
    c: Parallel(g0,g-3)
    c: Distance(g0) = 4
    c: Distance(g1) = 1.2
    c: Coincident(g0,g-3)
FEATURE [Part::Extrusion] Extrude056  label="Extrude scavo saldature rumble"
  Base = -> Sketch053
  Dir = (0,-1,2e-16)
  DirMode = 2
  FaceMakerClass = Part::FaceMakerBullseye
  FaceMakerMode = 3
  LengthFwd = 8.4
  LengthRev = 0
  Solid = true
  Symmetric = true
FEATURE [Sketcher::SketchObject] Sketch054  label="scavo saldature alimentatore connettore USB"
  ArcFitTolerance = 1e-06
  AttachmentSupport = -> [XZ_Plane]
  ExternalGeometry = -> [Sketch037]
  FullyConstrained = true
  MakeInternals = false
  MapMode = 5
  Placement = pos=(0,0,0) rot=(1,0,0;1.5708rad)
  sketch-geometry (4):
    g0: LineSegment StartX=-209.575 StartY=-80.4316 StartZ=0 EndX=-210.375 EndY=-80.4316 EndZ=0
    g1: LineSegment StartX=-210.375 StartY=-80.4316 StartZ=0 EndX=-210.375 EndY=-72.4316 EndZ=0
    g2: LineSegment StartX=-210.375 StartY=-72.4316 StartZ=0 EndX=-209.575 EndY=-72.4316 EndZ=0
    g3: LineSegment StartX=-209.575 StartY=-72.4316 StartZ=0 EndX=-209.575 EndY=-80.4316 EndZ=0
  constraints (11):
    c: Horizontal(g0)
    c: Coincident(g1,g0)
    c: Vertical(g1)
    c: Coincident(g2,g1)
    c: Horizontal(g2)
    c: Coincident(g3,g2)
    c: Coincident(g3,g0)
    c: Vertical(g3)
    c: DistanceX(g0,g0) = 0.8
    c: DistanceY(g3,g3) = 8
    c: Coincident(g0,g-4)
FEATURE [Part::Extrusion] Extrude057  label="Extrude scavo saldature alimentatore connettore USB"
  Base = -> Sketch054
  Dir = (0,-1,2e-16)
  DirMode = 2
  FaceMakerClass = Part::FaceMakerBullseye
  FaceMakerMode = 3
  LengthFwd = 11
  LengthRev = 0
  Solid = true
  Symmetric = true
FEATURE [Sketcher::SketchObject] Sketch055  label="buco interno per micro switch"
  ArcFitTolerance = 1e-06
  AttachmentSupport = -> [XZ_Plane]
  ExternalGeometry = -> [Sketch]
  FullyConstrained = true
  MakeInternals = false
  MapMode = 5
  Placement = pos=(0,0,0) rot=(1,0,0;1.5708rad)
  sketch-geometry (11):
    g0: LineSegment [constr] StartX=-194.483 StartY=34.2854 StartZ=0 EndX=-196.022 EndY=30.0568 EndZ=0
    g1: LineSegment [constr] StartX=-196.022 StartY=30.0568 StartZ=0 EndX=-197.561 EndY=25.8282 EndZ=0
    g2: LineSegment [constr] StartX=-196.022 StartY=30.0568 StartZ=0 EndX=-194.143 EndY=29.3727 EndZ=0
    g3: LineSegment [constr] StartX=-196.022 StartY=30.0568 StartZ=0 EndX=-197.902 EndY=30.7408 EndZ=0
    g4: LineSegment StartX=-196.362 StartY=34.9694 StartZ=0 EndX=-192.604 EndY=33.6014 EndZ=0
    g5: LineSegment StartX=-199.441 StartY=26.5122 StartZ=0 EndX=-195.682 EndY=25.1441 EndZ=0
    g6: LineSegment StartX=-192.604 StartY=33.6014 StartZ=0 EndX=-195.682 EndY=25.1441 EndZ=0
    g7: LineSegment StartX=-196.362 StartY=34.9694 StartZ=0 EndX=-199.441 EndY=26.5122 EndZ=0
    g8: GeomPoint [constr] X=-187.821 Y=29.2 Z=0
    g9: LineSegment [constr] StartX=-188.505 StartY=27.3206 StartZ=0 EndX=-196.022 EndY=30.0568 EndZ=0
    g10: LineSegment [constr] StartX=-187.821 StartY=29.2 StartZ=0 EndX=-188.505 EndY=27.3206 EndZ=0
  constraints (27):
    c: Coincident(g2,g0)
    c: Parallel(g0,g-3)
    c: Tangent(g1,g0) = -1.5708
    c: Perpendicular(g0,g2)
    c: Tangent(g2,g3)
    c: Distance(g0,g1) = 9
    c: Equal(g0,g1)
    c: Distance(g3,g2) = 4
    c: Equal(g2,g3)
    c: Parallel(g3,g4)
    c: Symmetric(g4,g4,g0)
    c: Parallel(g6,g1)
    c: Parallel(g7,g1)
    c: Symmetric(g6,g6,g2)
    c: Symmetric(g5,g5,g1)
    c: Symmetric(g7,g7,g3)
    c: Coincident(g7,g4)
    c: Coincident(g6,g4)
    c: Coincident(g5,g6)
    c: Symmetric(g-3,g-3,g8)
    c: Perpendicular(g-3,g9)
    c: Distance(g9) = 8
    c: Coincident(g3,g9)
    c: Coincident(g10,g8)
    c: Parallel(g10,g-3)
    c: Distance(g10) = 2
    c: Coincident(g10,g9)
FEATURE [Sketcher::SketchObject] Sketch056  label="buco esterno per micro switch"
  ArcFitTolerance = 1e-06
  AttachmentSupport = -> [XZ_Plane]
  ExternalGeometry = -> [Sketch055]
  FullyConstrained = true
  MakeInternals = false
  MapMode = 5
  Placement = pos=(0,0,0) rot=(1,0,0;1.5708rad)
  sketch-geometry (17):
    g0: GeomPoint [constr] X=-194.143 Y=29.3727 Z=0
    g1: GeomPoint [constr] X=-194.483 Y=34.2854 Z=0
    g2: GeomPoint [constr] X=-197.902 Y=30.7408 Z=0
    g3: GeomPoint [constr] X=-197.561 Y=25.8282 Z=0
    g4: GeomPoint [constr] X=-196.022 Y=30.0568 Z=0
    g5: LineSegment [constr] StartX=-194.483 StartY=34.2854 StartZ=0 EndX=-196.022 EndY=30.0568 EndZ=0
    g6: LineSegment [constr] StartX=-196.022 StartY=30.0568 StartZ=0 EndX=-197.561 EndY=25.8282 EndZ=0
    g7: LineSegment [constr] StartX=-197.902 StartY=30.7408 StartZ=0 EndX=-196.022 EndY=30.0568 EndZ=0
    g8: LineSegment [constr] StartX=-196.022 StartY=30.0568 StartZ=0 EndX=-194.143 EndY=29.3727 EndZ=0
    g9: LineSegment [constr] StartX=-195.338 StartY=31.9362 StartZ=0 EndX=-196.022 EndY=30.0568 EndZ=0
    g10: LineSegment [constr] StartX=-196.022 StartY=30.0568 StartZ=0 EndX=-196.706 EndY=28.1774 EndZ=0
    g11: LineSegment [constr] StartX=-196.022 StartY=30.0568 StartZ=0 EndX=-196.821 EndY=30.3475 EndZ=0
    g12: LineSegment [constr] StartX=-196.022 StartY=30.0568 StartZ=0 EndX=-195.223 EndY=29.7661 EndZ=0
    g13: LineSegment StartX=-194.539 StartY=31.6454 StartZ=0 EndX=-195.907 EndY=27.8867 EndZ=0
    g14: LineSegment StartX=-196.137 StartY=32.2269 StartZ=0 EndX=-197.505 EndY=28.4681 EndZ=0
    g15: LineSegment StartX=-196.137 StartY=32.2269 StartZ=0 EndX=-194.539 EndY=31.6454 EndZ=0
    g16: LineSegment StartX=-197.505 StartY=28.4681 StartZ=0 EndX=-195.907 EndY=27.8867 EndZ=0
  constraints (34):
    c: Symmetric(g-5,g-5,g1)
    c: Symmetric(g-5,g-6,g0)
    c: Symmetric(g-6,g-6,g3)
    c: Symmetric(g-5,g-6,g2)
    c: Coincident(g5,g1)
    c: Coincident(g5,g4)
    c: Coincident(g6,g4)
    c: Coincident(g6,g3)
    c: Equal(g5,g6)
    c: Coincident(g7,g2)
    c: Coincident(g7,g4)
    c: Coincident(g8,g4)
    c: Coincident(g8,g0)
    c: Equal(g7,g8)
    c: Coincident(g11,g9)
    c: Coincident(g12,g9)
    c: Tangent(g10,g9) = -1.5708
    c: Perpendicular(g11,g9)
    c: Parallel(g9,g-4)
    c: Equal(g9,g10)
    c: Parallel(g12,g11)
    c: Equal(g11,g12)
    c: Distance(g11,g12) = 1.7
    c: Distance(g9,g10) = 4
    c: Symmetric(g13,g13,g12)
    c: Parallel(g13,g9)
    c: Symmetric(g14,g14,g11)
    c: Symmetric(g15,g15,g9)
    c: Parallel(g15,g11)
    c: Symmetric(g16,g16,g10)
    c: Coincident(g16,g14)
    c: Coincident(g15,g14)
    c: Coincident(g13,g15)
    c: Coincident(g9,g4)
FEATURE [Sketcher::SketchObject] Sketch057  label="buco interno per SWITCH"
  ArcFitTolerance = 1e-06
  AttachmentSupport = -> [XZ_Plane]
  ExternalGeometry = -> [Sketch]
  FullyConstrained = true
  MakeInternals = false
  MapMode = 5
  Placement = pos=(0,0,0) rot=(1,0,0;1.5708rad)
  sketch-geometry (10):
    g0: GeomPoint [constr] X=-187.821 Y=29.2 Z=0
    g1: LineSegment [constr] StartX=-188.505 StartY=27.3206 StartZ=0 EndX=-193.203 EndY=29.0307 EndZ=0
    g2: LineSegment [constr] StartX=-190.809 StartY=35.6086 StartZ=0 EndX=-195.597 EndY=22.4529 EndZ=0
    g3: GeomPoint [constr] X=-193.203 Y=29.0307 Z=0
    g4: LineSegment [constr] StartX=-196.492 StartY=30.2278 StartZ=0 EndX=-189.914 EndY=27.8336 EndZ=0
    g5: LineSegment StartX=-194.098 StartY=36.8056 StartZ=0 EndX=-187.52 EndY=34.4115 EndZ=0
    g6: LineSegment StartX=-194.098 StartY=36.8056 StartZ=0 EndX=-198.886 EndY=23.6499 EndZ=0
    g7: LineSegment StartX=-187.52 StartY=34.4115 StartZ=0 EndX=-192.308 EndY=21.2558 EndZ=0
    g8: LineSegment StartX=-198.886 StartY=23.6499 StartZ=0 EndX=-192.308 EndY=21.2558 EndZ=0
    g9: LineSegment [constr] StartX=-187.821 StartY=29.2 StartZ=0 EndX=-188.505 EndY=27.3206 EndZ=0
  constraints (23):
    c: Symmetric(g-3,g-3,g0)
    c: Perpendicular(g1,g-3)
    c: Parallel(g2,g-3)
    c: Symmetric(g2,g2,g3)
    c: Perpendicular(g2,g4)
    c: Symmetric(g4,g4,g3)
    c: Distance(g2) = 14
    c: Distance(g4) = 7
    c: Distance(g1) = 5
    c: Parallel(g5,g4)
    c: Parallel(g7,g2)
    c: Symmetric(g5,g5,g2)
    c: Symmetric(g6,g6,g4)
    c: Symmetric(g7,g7,g4)
    c: Symmetric(g8,g8,g2)
    c: Coincident(g6,g5)
    c: Coincident(g7,g5)
    c: Coincident(g8,g7)
    c: Coincident(g3,g1)
    c: Coincident(g9,g0)
    c: Parallel(g9,g-3)
    c: Distance(g9) = 2
    c: Coincident(g1,g9)
FEATURE [Sketcher::SketchObject] Sketch058  label="buco esterno per SWITCH"
  ArcFitTolerance = 1e-06
  AttachmentSupport = -> [XZ_Plane]
  ExternalGeometry = -> [Sketch057]
  FullyConstrained = true
  MakeInternals = false
  MapMode = 5
  Placement = pos=(0,0,0) rot=(1,0,0;1.5708rad)
  sketch-geometry (12):
    g0: GeomPoint [constr] X=-190.809 Y=35.6086 Z=0
    g1: GeomPoint [constr] X=-196.492 Y=30.2278 Z=0
    g2: GeomPoint [constr] X=-189.914 Y=27.8336 Z=0
    g3: GeomPoint [constr] X=-195.597 Y=22.4529 Z=0
    g4: GeomPoint [constr] X=-193.203 Y=29.0307 Z=0
    g5: LineSegment [constr] StartX=-192.006 StartY=32.3196 StartZ=0 EndX=-194.4 EndY=25.7418 EndZ=0
    g6: GeomPoint [constr] X=-193.203 Y=29.0307 Z=0
    g7: LineSegment [constr] StartX=-195.082 StartY=29.7148 StartZ=0 EndX=-191.324 EndY=28.3467 EndZ=0
    g8: LineSegment StartX=-193.885 StartY=33.0037 StartZ=0 EndX=-190.127 EndY=31.6356 EndZ=0
    g9: LineSegment StartX=-190.127 StartY=31.6356 StartZ=0 EndX=-192.521 EndY=25.0578 EndZ=0
    g10: LineSegment StartX=-196.28 StartY=26.4258 StartZ=0 EndX=-192.521 EndY=25.0578 EndZ=0
    g11: LineSegment StartX=-193.885 StartY=33.0037 StartZ=0 EndX=-196.28 EndY=26.4258 EndZ=0
  constraints (21):
    c: Symmetric(g-6,g-6,g3)
    c: Symmetric(g-4,g-6,g2)
    c: Symmetric(g-5,g-4,g0)
    c: Symmetric(g-5,g-6,g1)
    c: Symmetric(g1,g2,g4)
    c: Parallel(g5,g-4)
    c: Symmetric(g5,g5,g6)
    c: Perpendicular(g7,g5)
    c: Symmetric(g7,g7,g6)
    c: Distance(g5) = 7
    c: Distance(g7) = 4
    c: Parallel(g8,g7)
    c: Parallel(g11,g5)
    c: Symmetric(g8,g8,g5)
    c: Symmetric(g9,g9,g7)
    c: Symmetric(g10,g10,g5)
    c: Symmetric(g11,g11,g7)
    c: Coincident(g11,g8)
    c: Coincident(g9,g8)
    c: Coincident(g9,g10)
    c: Coincident(g6,g4)
FEATURE [Part::Extrusion] Extrude060  label="Extrude buco interno per SWITCH destro"
  Base = -> Sketch057
  Dir = (0,-1,2e-16)
  DirMode = 2
  FaceMakerClass = Part::FaceMakerBullseye
  FaceMakerMode = 3
  LengthFwd = 13.2
  LengthRev = 0
  Placement = pos=(0,2.6,0) rot=(0,0,1;0rad)
  Solid = true
  Symmetric = false
FEATURE [Part::Extrusion] Extrude061  label="Extrude buco esterno per SWITCH destro"
  Base = -> Sketch058
  Dir = (0,-1,2e-16)
  DirMode = 2
  FaceMakerClass = Part::FaceMakerBullseye
  FaceMakerMode = 3
  LengthFwd = 2
  LengthRev = 0
  Placement = pos=(0,-10.6,0) rot=(0,0,1;0rad)
  Solid = true
  Symmetric = false
FEATURE [Sketcher::SketchObject] Sketch059  label="buco per spazio introduzione SWITCH"
  ArcFitTolerance = 1e-06
  AttachmentSupport = -> [XZ_Plane]
  ExternalGeometry = -> [Sketch057,Sketch010]
  FullyConstrained = true
  MakeInternals = false
  MapMode = 5
  Placement = pos=(0,0,0) rot=(1,0,0;1.5708rad)
  sketch-geometry (8):
    g0: LineSegment [constr] StartX=-201.368 StartY=36.3521 StartZ=0 EndX=-195.094 EndY=34.0687 EndZ=0
    g1: LineSegment [constr] StartX=-194.098 StartY=36.8056 StartZ=0 EndX=-195.094 EndY=34.0687 EndZ=0
    g2: LineSegment StartX=-198.658 StartY=24.2771 StartZ=0 EndX=-199.654 EndY=21.5401 EndZ=0
    g3: LineSegment StartX=-199.654 StartY=21.5401 StartZ=0 EndX=-181.196 EndY=14.822 EndZ=0
    g4: LineSegment StartX=-181.196 StartY=14.822 StartZ=0 EndX=-180.2 EndY=17.559 EndZ=0
    g5: LineSegment StartX=-180.2 StartY=17.559 StartZ=0 EndX=-198.658 EndY=24.2771 EndZ=0
    g6: LineSegment [constr] StartX=-204.932 StartY=26.5605 StartZ=0 EndX=-198.658 EndY=24.2771 EndZ=0
    g7: LineSegment [constr] StartX=-198.658 StartY=24.2771 StartZ=0 EndX=-199.654 EndY=21.5401 EndZ=0
  constraints (20):
    c: Parallel(g1,g-3)
    c: Parallel(g0,g-4)
    c: Coincident(g0,g-4)
    c: Coincident(g1,g-3)
    c: Coincident(g0,g1)
    c: Coincident(g3,g2)
    c: Coincident(g4,g3)
    c: Coincident(g5,g4)
    c: Coincident(g5,g2)
    c: Parallel(g5,g-5)
    c: Parallel(g3,g-5)
    c: Parallel(g4,g-6)
    c: DistanceX(g-6,g4) = 0
    c: Coincident(g6,g-5)
    c: Equal(g6,g0)
    c: Coincident(g7,g6)
    c: Equal(g7,g1)
    c: Tangent(g7,g-3)
    c: Coincident(g2,g6)
    c: Coincident(g2,g7)
FEATURE [Part::Extrusion] Extrude062  label="Extrude buco per spazio introduzione SWITCH"
  Base = -> Sketch059
  Dir = (0,-1,2e-16)
  DirMode = 2
  FaceMakerClass = Part::FaceMakerBullseye
  FaceMakerMode = 3
  LengthFwd = 13.2
  LengthRev = 0
  Solid = true
  Symmetric = true
FEATURE [Part::Extrusion] Extrude063  label="Extrude buco interno per SWITCH sinistro"
  Base = -> Sketch057
  Dir = (0,-1,2e-16)
  DirMode = 2
  FaceMakerClass = Part::FaceMakerBullseye
  FaceMakerMode = 3
  LengthFwd = 13.2
  LengthRev = 0
  Placement = pos=(0,10.6,0) rot=(0,0,1;0rad)
  Solid = true
  Symmetric = false
FEATURE [Part::Extrusion] Extrude064  label="Extrude buco esterno per SWITCH sinistro"
  Base = -> Sketch058
  Dir = (0,-1,2e-16)
  DirMode = 2
  FaceMakerClass = Part::FaceMakerBullseye
  FaceMakerMode = 3
  LengthFwd = 2
  LengthRev = 0
  Placement = pos=(0,12.6,0) rot=(0,0,1;0rad)
  Solid = true
  Symmetric = false
FEATURE [Sketcher::SketchObject] Sketch061  label="struttura esterna blocco switch"
  ArcFitTolerance = 1e-06
  AttachmentSupport = -> [XZ_Plane003]
  FullyConstrained = true
  MakeInternals = false
  MapMode = 5
  Placement = pos=(0,0,0) rot=(1,0,0;1.5708rad)
  sketch-geometry (5):
    g0: LineSegment StartX=-1 StartY=-5.1 StartZ=0 EndX=1 EndY=-5.1 EndZ=0
    g1: LineSegment StartX=1 StartY=-5.1 StartZ=0 EndX=1 EndY=5.1 EndZ=0
    g2: LineSegment StartX=1 StartY=5.1 StartZ=0 EndX=-1 EndY=5.1 EndZ=0
    g3: LineSegment StartX=-1 StartY=5.1 StartZ=0 EndX=-1 EndY=-5.1 EndZ=0
    g4: GeomPoint [constr] X=0 Y=0 Z=0
  constraints (12):
    c: Coincident(g0,g1)
    c: Coincident(g1,g2)
    c: Coincident(g2,g3)
    c: Coincident(g3,g0)
    c: Horizontal(g0)
    c: Horizontal(g2)
    c: Vertical(g1)
    c: Vertical(g3)
    c: Symmetric(g2,g0,g4)
    c: Distance(g1,g3) = 2
    c: Distance(g0,g2) = 10.2
    c: Coincident(g4,g-1)
FEATURE [Sketcher::SketchObject] Sketch062  label="struttura interna blocco switch"
  ArcFitTolerance = 1e-06
  AttachmentSupport = -> [XZ_Plane003]
  ExternalGeometry = -> [Sketch061]
  FullyConstrained = true
  MakeInternals = false
  MapMode = 5
  Placement = pos=(0,0,0) rot=(1,0,0;1.5708rad)
  sketch-geometry (5):
    g0: LineSegment StartX=-1 StartY=3.1 StartZ=0 EndX=-1 EndY=-3.1 EndZ=0
    g1: LineSegment StartX=-1 StartY=-3.1 StartZ=0 EndX=1 EndY=-3.1 EndZ=0
    g2: LineSegment StartX=1 StartY=-3.1 StartZ=0 EndX=1 EndY=3.1 EndZ=0
    g3: LineSegment StartX=1 StartY=3.1 StartZ=0 EndX=-1 EndY=3.1 EndZ=0
    g4: GeomPoint [constr] X=0 Y=0 Z=0
  constraints (12):
    c: Coincident(g0,g1)
    c: Coincident(g1,g2)
    c: Coincident(g2,g3)
    c: Coincident(g3,g0)
    c: Vertical(g0)
    c: Vertical(g2)
    c: Horizontal(g1)
    c: Horizontal(g3)
    c: Symmetric(g2,g0,g4)
    c: Coincident(g4,g-1)
    c: Distance(g0) = 6.2
    c: Equal(g3,g-3)
FEATURE [Sketcher::SketchObject] Sketch063  label="blocchi tra switch"
  ArcFitTolerance = 1e-06
  AttachmentSupport = -> [XZ_Plane003]
  ExternalGeometry = -> [Sketch061,Sketch062]
  FullyConstrained = true
  MakeInternals = false
  MapMode = 5
  Placement = pos=(0,0,0) rot=(1,0,0;1.5708rad)
  sketch-geometry (8):
    g0: LineSegment StartX=-3 StartY=5.1 StartZ=0 EndX=-1 EndY=5.1 EndZ=0
    g1: LineSegment StartX=-1 StartY=5.1 StartZ=0 EndX=-1 EndY=3.1 EndZ=0
    g2: LineSegment StartX=-1 StartY=3.1 StartZ=0 EndX=-3 EndY=3.1 EndZ=0
    g3: LineSegment StartX=-3 StartY=3.1 StartZ=0 EndX=-3 EndY=5.1 EndZ=0
    g4: LineSegment StartX=-3 StartY=-3.1 StartZ=0 EndX=-1 EndY=-3.1 EndZ=0
    g5: LineSegment StartX=-1 StartY=-3.1 StartZ=0 EndX=-1 EndY=-5.1 EndZ=0
    g6: LineSegment StartX=-1 StartY=-5.1 StartZ=0 EndX=-3 EndY=-5.1 EndZ=0
    g7: LineSegment StartX=-3 StartY=-5.1 StartZ=0 EndX=-3 EndY=-3.1 EndZ=0
  constraints (20):
    c: Horizontal(g0)
    c: Coincident(g1,g0)
    c: Coincident(g2,g1)
    c: Horizontal(g2)
    c: Coincident(g3,g2)
    c: Coincident(g3,g0)
    c: Vertical(g3)
    c: Horizontal(g4)
    c: Coincident(g5,g4)
    c: Coincident(g6,g5)
    c: Horizontal(g6)
    c: Coincident(g7,g6)
    c: Coincident(g7,g4)
    c: Vertical(g7)
    c: Coincident(g0,g-4)
    c: Coincident(g1,g-5)
    c: Coincident(g4,g-6)
    c: Coincident(g5,g-7)
    c: Distance(g0) = 2
    c: Distance(g4) = 2
FEATURE [Sketcher::SketchObject] Sketch066  label="piano per rampino"
  ArcFitTolerance = 1e-06
  AttachmentSupport = -> [XZ_Plane002]
  ExternalGeometry = -> [Sketch045]
  FullyConstrained = true
  MakeInternals = false
  MapMode = 5
  Placement = pos=(0,0,0) rot=(1,0,0;1.5708rad)
  sketch-geometry (4):
    g0: LineSegment StartX=5.4 StartY=5.1 StartZ=0 EndX=5.4 EndY=3.9 EndZ=0
    g1: LineSegment StartX=5.4 StartY=3.9 StartZ=0 EndX=7 EndY=3.9 EndZ=0
    g2: LineSegment StartX=7 StartY=3.9 StartZ=0 EndX=7 EndY=5.1 EndZ=0
    g3: LineSegment StartX=7 StartY=5.1 StartZ=0 EndX=5.4 EndY=5.1 EndZ=0
  constraints (11):
    c: Coincident(g0,g1)
    c: Coincident(g1,g2)
    c: Coincident(g2,g3)
    c: Coincident(g3,g0)
    c: Vertical(g0)
    c: Vertical(g2)
    c: Horizontal(g1)
    c: Horizontal(g3)
    c: Distance(g0,g2) = 1.6
    c: Distance(g1,g3) = 1.2
    c: Coincident(g2,g-3)
FEATURE [Sketcher::SketchObject] Sketch064  label="rampini_per_serraggio_struttura"
  ArcFitTolerance = 1e-06
  AttachmentSupport = -> [XZ_Plane002]
  ExternalGeometry = -> [Sketch066,Sketch045]
  FullyConstrained = true
  MakeInternals = false
  MapMode = 5
  Placement = pos=(0,0,0) rot=(1,0,0;1.5708rad)
  sketch-geometry (7):
    g0: LineSegment StartX=7 StartY=5.1 StartZ=0 EndX=7 EndY=3.9 EndZ=0
    g1: LineSegment StartX=7 StartY=3.9 StartZ=0 EndX=9 EndY=3.9 EndZ=0
    g2: LineSegment StartX=7 StartY=5.1 StartZ=0 EndX=7 EndY=5.1 EndZ=0
    g3: LineSegment StartX=7 StartY=5.1 StartZ=0 EndX=7 EndY=7.5 EndZ=0
    g4: LineSegment StartX=9 StartY=5.1 StartZ=0 EndX=9 EndY=3.9 EndZ=0
    g5: LineSegment StartX=7 StartY=7.5 StartZ=0 EndX=9 EndY=7.5 EndZ=0
    g6: LineSegment StartX=9 StartY=7.5 StartZ=0 EndX=9 EndY=5.1 EndZ=0
  constraints (20):
    c: Vertical(g0)
    c: Coincident(g1,g0)
    c: Horizontal(g1)
    c: Coincident(g2,g0)
    c: Horizontal(g2)
    c: Coincident(g3,g2)
    c: Vertical(g3)
    c: Coincident(g5,g3)
    c: Coincident(g4,g6)
    c: Coincident(g4,g1)
    c: Vertical(g4)
    c: Coincident(g0,g-3)
    c: DistanceY(g-4,g3) = 2.4
    c: DistanceX(g1,g1) = 2
    c: DistanceY(g2,g6) = 0
    c: DistanceX(g2,g2) = 0
    c: DistanceY(g0,g0) = 1.2
    c: Coincident(g5,g6)
    c: Horizontal(g5)
    c: Vertical(g6)
FEATURE [Sketcher::SketchObject] Sketch067  label="perno per blocco switch"
  ArcFitTolerance = 1e-06
  AttachmentSupport = -> [XZ_Plane]
  ExternalGeometry = -> [Sketch,Sketch010]
  FullyConstrained = true
  MakeInternals = false
  MapMode = 5
  Placement = pos=(0,0,0) rot=(1,0,0;1.5708rad)
  sketch-geometry (14):
    g0: LineSegment StartX=-191.073 StartY=24.9429 StartZ=0 EndX=-185.81 EndY=23.0276 EndZ=0
    g1: LineSegment StartX=-183.76 StartY=23.9839 StartZ=0 EndX=-182.392 EndY=27.7427 EndZ=0
    g2: LineSegment StartX=-183.348 StartY=29.7934 StartZ=0 EndX=-188.61 EndY=31.7087 EndZ=0
    g3: LineSegment StartX=-188.61 StartY=31.7087 StartZ=0 EndX=-191.073 EndY=24.9429 EndZ=0
    g4: GeomPoint [constr] X=-186.459 Y=27.0946 Z=0
    g5: LineSegment StartX=-189.022 StartY=25.8992 StartZ=0 EndX=-185.263 EndY=24.5311 EndZ=0
    g6: LineSegment StartX=-185.263 StartY=24.5311 StartZ=0 EndX=-183.895 EndY=28.2899 EndZ=0
    g7: LineSegment StartX=-183.895 StartY=28.2899 StartZ=0 EndX=-187.654 EndY=29.658 EndZ=0
    g8: LineSegment StartX=-187.654 StartY=29.658 StartZ=0 EndX=-189.022 EndY=25.8992 EndZ=0
    g9: GeomPoint [constr] X=-186.459 Y=27.0946 Z=0
    g10: ArcOfCircle CenterX=-185.263 CenterY=24.5311 CenterZ=0 NormalX=0 NormalY=0 NormalZ=1 AngleXU=0 Radius=1.6 StartAngle=4.36332 EndAngle=5.93412
    g11: GeomPoint [constr] X=-184.307 Y=22.4804 Z=0
    g12: ArcOfCircle CenterX=-183.895 CenterY=28.2899 CenterZ=0 NormalX=0 NormalY=0 NormalZ=1 AngleXU=0 Radius=1.6 StartAngle=5.93412 EndAngle=7.50492
    g13: GeomPoint [constr] X=-181.844 Y=29.2462 Z=0
  constraints (30):
    c: Coincident(g2,g3)
    c: Coincident(g3,g0)
    c: Symmetric(g13,g0,g4)
    c: Distance(g11,g3) = 7.2
    c: Distance(g0,g2) = 7.2
    c: Parallel(g3,g1)
    c: Parallel(g2,g0)
    c: Perpendicular(g2,g3)
    c: Coincident(g5,g6)
    c: Coincident(g6,g7)
    c: Coincident(g7,g8)
    c: Coincident(g8,g5)
    c: Symmetric(g7,g5,g9)
    c: Distance(g6,g8) = 4
    c: Distance(g5,g7) = 4
    c: Coincident(g9,g4)
    c: Parallel(g8,g6)
    c: Parallel(g7,g5)
    c: Perpendicular(g7,g8)
    c: Tangent(g8,g-3)
    c: Tangent(g2,g-4)
    c: PointOnObject(g11,g1)
    c: PointOnObject(g11,g0)
    c: Tangent(g1,g10) = -1.5708
    c: Tangent(g0,g10) = -1.5708
    c: PointOnObject(g13,g1)
    c: Tangent(g1,g12) = -1.5708
    c: Tangent(g2,g12) = -1.5708
    c: Equal(g10,g12)
    c: Coincident(g10,g5)
FEATURE [Part::Extrusion] Extrude072  label="Extrude perno per blocco switch"
  Base = -> Sketch067
  Dir = (0,-1,2e-16)
  DirMode = 2
  FaceMakerClass = Part::FaceMakerBullseye
  FaceMakerMode = 3
  LengthFwd = 25.2
  LengthRev = 0
  Solid = true
  Symmetric = true
FEATURE [Part::MultiFuse] Fusion
  Refine = true
  Shapes = -> [Extrude,Sweep,Extrude007,Extrude011,Extrude005,Extrude012,Extrude013,Extrude016,Extrude031,Extrude039,Extrude045,Extrude072]
FEATURE [Part::Cut] Cut
  Base = -> Fusion
  Refine = true
  Tool = -> Extrude001
FEATURE [Part::Cut] Cut001
  Base = -> Cut
  Refine = true
  Tool = -> Extrude004
FEATURE [Part::Cut] Cut002
  Base = -> Cut001
  Refine = true
  Tool = -> Extrude006
FEATURE [Part::Cut] Cut003
  Base = -> Cut002
  Refine = true
  Tool = -> Extrude008
FEATURE [Part::Cut] Cut004
  Base = -> Cut003
  Refine = true
  Tool = -> Extrude009
FEATURE [Part::Cut] Cut005
  Base = -> Cut004
  Refine = true
  Tool = -> Extrude010
FEATURE [Part::Cut] Cut006
  Base = -> Cut005
  Refine = true
  Tool = -> Extrude014
FEATURE [Part::Cut] Cut007
  Base = -> Cut006
  Refine = true
  Tool = -> Extrude015
FEATURE [Part::Cut] Cut008
  Base = -> Cut007
  Refine = true
  Tool = -> Extrude018
FEATURE [Part::Cut] Cut009
  Base = -> Cut008
  Refine = true
  Tool = -> Extrude019
FEATURE [Part::Cut] Cut010
  Base = -> Cut009
  Refine = true
  Tool = -> Extrude020
FEATURE [Part::Cut] Cut011
  Base = -> Cut010
  Refine = true
  Tool = -> Extrude021
FEATURE [Part::Cut] Cut012
  Base = -> Cut011
  Refine = true
  Tool = -> Extrude022
FEATURE [Part::Cut] Cut013
  Base = -> Cut012
  Refine = true
  Tool = -> Extrude023
FEATURE [Part::Cut] Cut014
  Base = -> Cut013
  Refine = true
  Tool = -> Extrude032
FEATURE [Part::Cut] Cut015
  Base = -> Cut014
  Refine = true
  Tool = -> Extrude033
FEATURE [Part::Cut] Cut016
  Base = -> Cut015
  Refine = true
  Tool = -> Extrude034
FEATURE [Part::Cut] Cut017
  Base = -> Cut016
  Refine = true
  Tool = -> Extrude035
FEATURE [Part::Cut] Cut018
  Base = -> Cut017
  Refine = true
  Tool = -> Extrude036
FEATURE [Part::Cut] Cut019
  Base = -> Cut018
  Refine = true
  Tool = -> Extrude037
FEATURE [Part::Cut] Cut020
  Base = -> Cut019
  Refine = true
  Tool = -> Extrude030
FEATURE [Part::Cut] Cut022
  Base = -> Cut020
  Refine = true
  Tool = -> Extrude038
FEATURE [Part::Cut] Cut023
  Base = -> Cut022
  Refine = true
  Tool = -> Extrude041
FEATURE [Part::Cut] Cut024
  Base = -> Cut023
  Refine = true
  Tool = -> Extrude040
FEATURE [Part::Cut] Cut025
  Base = -> Cut024
  Refine = true
  Tool = -> Extrude042
FEATURE [Part::Cut] Cut026
  Base = -> Cut025
  Refine = true
  Tool = -> Extrude043
FEATURE [Part::Cut] Cut027
  Base = -> Cut026
  Refine = true
  Tool = -> Extrude044
FEATURE [Part::Cut] Cut028
  Base = -> Cut027
  Refine = true
  Tool = -> Extrude046
FEATURE [Part::Cut] Cut029
  Base = -> Cut028
  Refine = true
  Tool = -> Extrude047
FEATURE [Part::Cut] Cut033
  Base = -> Cut029
  Refine = true
  Tool = -> Extrude055
FEATURE [Part::Cut] Cut034
  Base = -> Cut033
  Refine = true
  Tool = -> Extrude056
FEATURE [Part::Cut] Cut035
  Base = -> Cut034
  Refine = true
  Tool = -> Extrude057
FEATURE [Part::Cut] Cut037
  Base = -> Cut035
  Refine = true
  Tool = -> Extrude060
FEATURE [Part::Cut] Cut038
  Base = -> Cut037
  Refine = true
  Tool = -> Extrude061
FEATURE [Part::Cut] Cut039
  Base = -> Cut038
  Refine = true
  Tool = -> Extrude063
FEATURE [Part::Cut] Cut040
  Base = -> Cut039
  Refine = true
  Tool = -> Extrude064
FEATURE [Part::Cut] Cut041
  Base = -> Cut040
  Refine = true
  Tool = -> Extrude062
FEATURE [Sketcher::SketchObject] Sketch068  label="base con smusso sopra neopixel"
  ArcFitTolerance = 1e-06
  AttachmentSupport = -> [YZ_Plane002]
  FullyConstrained = true
  MakeInternals = false
  MapMode = 5
  Placement = pos=(0,0,0) rot=(0.57735,0.57735,0.57735;2.0944rad)
  sketch-geometry (5):
    g0: LineSegment StartX=-9.5 StartY=-6.1 StartZ=0 EndX=9.5 EndY=-6.1 EndZ=0
    g1: LineSegment StartX=9.5 StartY=-6.1 StartZ=0 EndX=9.5 EndY=6.1 EndZ=0
    g2: LineSegment StartX=9.5 StartY=6.1 StartZ=0 EndX=-9.5 EndY=6.1 EndZ=0
    g3: LineSegment StartX=-9.5 StartY=6.1 StartZ=0 EndX=-9.5 EndY=-6.1 EndZ=0
    g4: GeomPoint [constr] X=0 Y=0 Z=0
  constraints (12):
    c: Coincident(g0,g1)
    c: Coincident(g1,g2)
    c: Coincident(g2,g3)
    c: Coincident(g3,g0)
    c: Horizontal(g0)
    c: Horizontal(g2)
    c: Vertical(g1)
    c: Vertical(g3)
    c: Symmetric(g2,g0,g4)
    c: Distance(g1,g3) = 19
    c: Distance(g0,g2) = 12.2
    c: Coincident(g4,g-1)
FEATURE [Sketcher::SketchObject] Sketch069  label="cilindro minore"
  ArcFitTolerance = 1e-06
  AttachmentSupport = -> [XZ_Plane004]
  FullyConstrained = true
  MakeInternals = false
  MapMode = 5
  Placement = pos=(0,0,0) rot=(1,0,0;1.5708rad)
  sketch-geometry (1):
    g0: Circle CenterX=0 CenterY=0 CenterZ=0 NormalX=0 NormalY=0 NormalZ=1 AngleXU=0 Radius=5.8
  constraints (2):
    c: Diameter(g0) = 11.6
    c: Coincident(g0,g-1)
FEATURE [Sketcher::SketchObject] Sketch070  label="cilindro maggiore"
  ArcFitTolerance = 1e-06
  AttachmentSupport = -> [XZ_Plane004]
  ExternalGeometry = -> [Sketch069]
  FullyConstrained = true
  MakeInternals = false
  MapMode = 5
  Placement = pos=(0,0,0) rot=(1,0,0;1.5708rad)
  sketch-geometry (1):
    g0: Circle CenterX=0 CenterY=0 CenterZ=0 NormalX=0 NormalY=0 NormalZ=1 AngleXU=0 Radius=6.5
  constraints (2):
    c: Coincident(g0,g-1)
    c: Diameter(g0) = 13
FEATURE [Sketcher::SketchObject] Sketch071  label="buco interno"
  ArcFitTolerance = 1e-06
  AttachmentSupport = -> [XZ_Plane004]
  ExternalGeometry = -> [Sketch069]
  FullyConstrained = true
  MakeInternals = false
  MapMode = 5
  Placement = pos=(0,0,0) rot=(1,0,0;1.5708rad)
  sketch-geometry (1):
    g0: Circle CenterX=0 CenterY=0 CenterZ=0 NormalX=0 NormalY=0 NormalZ=1 AngleXU=0 Radius=5
  constraints (2):
    c: Coincident(g0,g-1)
    c: Diameter(g0) = 10
FEATURE [PartDesign::Pad] Pad
  Direction = (0,-1,2e-16)
  Length = 1.2
  Length2 = 10
  Placement = pos=(0,0,0) rot=(1,0,0;1.5708rad)
  Profile = -> Sketch070
  ReferenceAxis = -> Sketch070 [N_Axis]
  Refine = true
  Suppressed = false
  Type = 0
FEATURE [PartDesign::Pad] Pad001
  BaseFeature = -> Pad
  Direction = (0,-1,2e-16)
  Length = 5.6
  Length2 = 10
  Placement = pos=(0,0,0) rot=(1,0,0;1.5708rad)
  Profile = -> Sketch069
  ReferenceAxis = -> Sketch069 [N_Axis]
  Refine = true
  Suppressed = false
  Type = 0
FEATURE [PartDesign::Pocket] Pocket
  BaseFeature = -> Pad001
  Direction = (0,1,-2e-16)
  Length = 7
  Length2 = 5
  Midplane = true
  Placement = pos=(0,0,0) rot=(1,0,0;1.5708rad)
  Profile = -> Sketch071
  ReferenceAxis = -> Sketch071 [N_Axis]
  Refine = true
  Suppressed = false
  Type = 0
FEATURE [PartDesign::Fillet] Fillet
  Base = -> Pocket [Face7]
  BaseFeature = -> Pocket
  Placement = pos=(0,0,0) rot=(1,0,0;1.5708rad)
  Radius = 1
  Refine = true
  SupportTransform = false
  Suppressed = false
  UseAllEdges = false
FEATURE [PartDesign::Body] Body004  label="pulsanti lato sinistro"
  AllowCompound = false
  Group = -> [Sketch069,Sketch070,Sketch071,Pad,Pad001,Pocket,Fillet]
  Origin = -> Origin004
  Tip = -> Fillet
FEATURE [Sketcher::SketchObject] Sketch072  label="buco per saldature e diodo driver solenoide"
  ArcFitTolerance = 1e-06
  AttachmentSupport = -> [XZ_Plane]
  ExternalGeometry = -> [Sketch038]
  FullyConstrained = true
  MakeInternals = false
  MapMode = 5
  Placement = pos=(0,0,0) rot=(1,0,0;1.5708rad)
  sketch-geometry (4):
    g0: LineSegment StartX=-212.269 StartY=-43.9083 StartZ=0 EndX=-207.197 EndY=-33.0326 EndZ=0
    g1: LineSegment StartX=-207.197 StartY=-33.0326 StartZ=0 EndX=-207.56 EndY=-32.8635 EndZ=0
    g2: LineSegment StartX=-207.56 StartY=-32.8635 StartZ=0 EndX=-212.631 EndY=-43.7392 EndZ=0
    g3: LineSegment StartX=-212.631 StartY=-43.7392 StartZ=0 EndX=-212.269 EndY=-43.9083 EndZ=0
  constraints (11):
    c: Coincident(g1,g0)
    c: Coincident(g2,g1)
    c: Coincident(g3,g2)
    c: Coincident(g3,g0)
    c: Parallel(g-3,g0)
    c: Parallel(g0,g2)
    c: Perpendicular(g0,g3)
    c: Perpendicular(g1,g0)
    c: Distance(g3) = 0.4
    c: Distance(g2) = 12
    c: Coincident(g0,g-3)
FEATURE [Part::Extrusion] Extrude074  label="Extrude buco per saldature e diodo driver solenoide"
  Base = -> Sketch072
  Dir = (0,-1,2e-16)
  DirMode = 2
  FaceMakerClass = Part::FaceMakerBullseye
  FaceMakerMode = 3
  LengthFwd = 14.6
  LengthRev = 0
  Solid = true
  Symmetric = true
FEATURE [Part::Cut] Cut042
  Base = -> Cut041
  Refine = true
  Tool = -> Extrude074
FEATURE [Sketcher::SketchObject] Sketch073  label="fori slargati blocco solenoide"
  ArcFitTolerance = 1e-06
  AttachmentSupport = -> [XY_Plane]
  ExternalGeometry = -> [Sketch030]
  FullyConstrained = true
  MakeInternals = false
  MapMode = 5
  sketch-geometry (2):
    g0: Circle CenterX=-152.209 CenterY=6.95 CenterZ=0 NormalX=0 NormalY=0 NormalZ=1 AngleXU=0 Radius=3.7
    g1: Circle CenterX=-130.41 CenterY=-6.95 CenterZ=0 NormalX=0 NormalY=0 NormalZ=1 AngleXU=0 Radius=3.7
  constraints (4):
    c: Diameter(g0) = 7.4
    c: Coincident(g0,g-3)
    c: Diameter(g1) = 7.4
    c: Coincident(g1,g-4)
FEATURE [Part::Extrusion] Extrude075  label="Extrude fori slargati blocco solenoide"
  Base = -> Sketch073
  Dir = (0,0,1)
  DirMode = 2
  FaceMakerClass = Part::FaceMakerBullseye
  FaceMakerMode = 3
  LengthFwd = 1.5
  LengthRev = 0
  Placement = pos=(0,0,36.4) rot=(0,0,1;0rad)
  Solid = true
  Symmetric = false
FEATURE [Part::Cut] Cut043
  Base = -> Cut042
  Refine = true
  Tool = -> Extrude075
FEATURE [Sketcher::SketchObject] Sketch074  label="lato sx pistola"
  ArcFitTolerance = 1e-06
  AttachmentSupport = -> [XZ_Plane]
  ExternalGeometry = -> [Sketch016,Sketch,Sketch058]
  FullyConstrained = true
  MakeInternals = false
  MapMode = 5
  Placement = pos=(0,0,0) rot=(1,0,0;1.5708rad)
  sketch-geometry (37):
    g0: LineSegment StartX=-82.8 StartY=3.2 StartZ=0 EndX=0 EndY=3.2 EndZ=0
    g1: LineSegment StartX=-82.8 StartY=3.2 StartZ=0 EndX=-82.8 EndY=6.2 EndZ=0
    g2: LineSegment [constr] StartX=-107.6 StartY=18 StartZ=0 EndX=-107.6 EndY=20 EndZ=0
    g3: LineSegment [constr] StartX=-132.428 StartY=18 StartZ=0 EndX=-132.428 EndY=20 EndZ=0
    g4: LineSegment StartX=-132.428 StartY=20 StartZ=0 EndX=-107.6 EndY=20 EndZ=0
    g5: ArcOfCircle CenterX=-107.6 CenterY=4 CenterZ=0 NormalX=0 NormalY=0 NormalZ=1 AngleXU=0 Radius=16 StartAngle=0.137937 EndAngle=1.5708
    g6: LineSegment StartX=-82.8 StartY=6.2 StartZ=0 EndX=-91.752 EndY=6.2 EndZ=0
    g7: LineSegment [constr] StartX=-145.743 StartY=8.32624 StartZ=0 EndX=-147.645 EndY=8.94427 EndZ=0
    g8: ArcOfCircle CenterX=-132.428 CenterY=4 CenterZ=0 NormalX=0 NormalY=0 NormalZ=1 AngleXU=0 Radius=16 StartAngle=1.5708 EndAngle=2.82743
    g9: LineSegment StartX=-215.932 StartY=-80.4316 StartZ=0 EndX=-176.685 EndY=-80.4316 EndZ=0
    g10: LineSegment StartX=-147.645 StartY=8.94427 StartZ=0 EndX=-176.685 EndY=-80.4316 EndZ=0
    g11: LineSegment [constr] StartX=-193.988 StartY=-2.33927 StartZ=0 EndX=-192.176 EndY=-3.18451 EndZ=0
    g12: LineSegment [constr] StartX=-217.232 StartY=-52.1862 StartZ=0 EndX=-215.42 EndY=-53.0314 EndZ=0
    g13: LineSegment StartX=-192.176 StartY=-3.18451 StartZ=0 EndX=-215.42 EndY=-53.0314 EndZ=0
    g14: ArcOfCircle CenterX=-184.801 CenterY=-67.3089 CenterZ=0 NormalX=0 NormalY=0 NormalZ=1 AngleXU=0 Radius=33.7833 StartAngle=2.70526 EndAngle=3.54053
    g15: ArcOfCircle CenterX=-207.583 CenterY=4 CenterZ=0 NormalX=0 NormalY=0 NormalZ=1 AngleXU=0 Radius=17 StartAngle=5.84685 EndAngle=7.56663
    g16: LineSegment StartX=-202.765 StartY=20.303 StartZ=0 EndX=-195.887 EndY=39.2 EndZ=0
    g17: LineSegment [constr] StartX=-193.885 StartY=33.0037 StartZ=0 EndX=-197.644 EndY=34.3718 EndZ=0
    g18: LineSegment StartX=-195.887 StartY=39.2 StartZ=0 EndX=0 EndY=39.2 EndZ=0
    g19: LineSegment StartX=0 StartY=3.2 StartZ=0 EndX=0 EndY=39.2 EndZ=0
    g20: LineSegment StartX=-189.939 StartY=31.5672 StartZ=0 EndX=-192.333 EndY=24.9893 EndZ=0
    g21: LineSegment StartX=-196.467 StartY=26.4942 StartZ=0 EndX=-194.073 EndY=33.0721 EndZ=0
    g22: Circle CenterX=-213.443 CenterY=-76.8316 CenterZ=0 NormalX=0 NormalY=0 NormalZ=1 AngleXU=0 Radius=1.8
    g23: Circle CenterX=-179.305 CenterY=-76.8316 CenterZ=0 NormalX=0 NormalY=0 NormalZ=1 AngleXU=0 Radius=1.8
    g24: Circle CenterX=-184.08 CenterY=34.8 CenterZ=0 NormalX=0 NormalY=0 NormalZ=1 AngleXU=0 Radius=1.8
    g25: Circle CenterX=-78.51 CenterY=34.8 CenterZ=0 NormalX=0 NormalY=0 NormalZ=1 AngleXU=0 Radius=1.8
    g26: Circle CenterX=-78.51 CenterY=7.6 CenterZ=0 NormalX=0 NormalY=0 NormalZ=1 AngleXU=0 Radius=1.8
    g27: Circle CenterX=-5.6 CenterY=34.8 CenterZ=0 NormalX=0 NormalY=0 NormalZ=1 AngleXU=0 Radius=1.8
    g28: Circle CenterX=-5.6 CenterY=7.6 CenterZ=0 NormalX=0 NormalY=0 NormalZ=1 AngleXU=0 Radius=1.8
    g29: LineSegment StartX=-190.127 StartY=31.6356 StartZ=0 EndX=-189.939 EndY=31.5672 EndZ=0
    g30: LineSegment StartX=-194.073 StartY=33.0721 StartZ=0 EndX=-193.885 EndY=33.0037 EndZ=0
    g31: LineSegment StartX=-193.885 StartY=33.0037 StartZ=0 EndX=-190.127 EndY=31.6356 EndZ=0
    g32: LineSegment StartX=-196.467 StartY=26.4942 StartZ=0 EndX=-192.333 EndY=24.9893 EndZ=0
    g33: Circle CenterX=-19 CenterY=21.2 CenterZ=0 NormalX=0 NormalY=0 NormalZ=1 AngleXU=0 Radius=6.3
    g34: Circle CenterX=-42 CenterY=21.2 CenterZ=0 NormalX=0 NormalY=0 NormalZ=1 AngleXU=0 Radius=6.3
    g35: Circle CenterX=-65 CenterY=21.2 CenterZ=0 NormalX=0 NormalY=0 NormalZ=1 AngleXU=0 Radius=6.3
    g36: LineSegment [constr] StartX=-4 StartY=21.2 StartZ=0 EndX=-65 EndY=21.2 EndZ=0
  constraints (96):
    c: Coincident(g0,g-41)
    c: Horizontal(g0)
    c: PointOnObject(g0,g-39)
    c: Coincident(g1,g0)
    c: Vertical(g1)
    c: DistanceY(g1,g1) = 3
    c: Coincident(g2,g-17)
    c: Vertical(g2)
    c: Coincident(g3,g-16)
    c: Vertical(g3)
    c: DistanceY(g2,g2) = 2
    c: DistanceY(g3,g3) = 2
    c: Coincident(g4,g3)
    c: Coincident(g4,g2)
    c: Coincident(g5,g-17)
    c: Coincident(g5,g2)
    c: Coincident(g6,g1)
    c: Horizontal(g6)
    c: Coincident(g6,g5)
    c: Coincident(g7,g-15)
    c: Coincident(g8,g7)
    c: Coincident(g8,g3)
    c: Coincident(g8,g-15)
    c: Horizontal(g9)
    c: DistanceY(g-13,g9) = 2
    c: Coincident(g10,g7)
    c: Parallel(g10,g-14)
    c: Coincident(g9,g10)
    c: Distance(g11) = 2
    c: Coincident(g11,g-11)
    c: Perpendicular(g-11,g11)
    c: Distance(g12) = 2
    c: Coincident(g12,g-12)
    c: Perpendicular(g-11,g12)
    c: Coincident(g13,g11)
    c: Coincident(g13,g12)
    c: Coincident(g14,g-32)
    c: Coincident(g14,g12)
    c: Coincident(g14,g9)
    c: Coincident(g15,g-10)
    c: Coincident(g15,g11)
    c: Parallel(g16,g-22)
    c: Distance(g17) = 4
    c: PointOnObject(g17,g16)
    c: Coincident(g15,g16)
    c: Horizontal(g18)
    c: Coincident(g18,g16)
    c: Coincident(g19,g0)
    c: PointOnObject(g19,g-39)
    c: DistanceY(g19,g-36) = 2
    c: Coincident(g18,g19)
    c: Diameter(g22) = 3.6
    c: Coincident(g22,g-9)
    c: Diameter(g23) = 3.6
    c: Coincident(g23,g-8)
    c: Diameter(g24) = 3.6
    c: Diameter(g25) = 3.6
    c: Diameter(g26) = 3.6
    c: Diameter(g27) = 3.6
    c: Diameter(g28) = 3.6
    c: Coincident(g27,g-4)
    c: Coincident(g28,g-3)
    c: Coincident(g25,g-6)
    c: Coincident(g26,g-5)
    c: Coincident(g24,g-7)
    c: Parallel(g20,g-21)
    c: Equal(g20,g-21)
    c: Parallel(g21,g-19)
    c: Equal(g21,g-19)
    c: Distance(g29) = 0.2
    c: Distance(g30) = 0.2
    c: Parallel(g29,g-20)
    c: Parallel(g31,g-20)
    c: Equal(g31,g-20)
    c: Coincident(g30,g31)
    c: Coincident(g31,g29)
    c: Coincident(g29,g-21)
    c: Parallel(g30,g31)
    c: Coincident(g17,g30)
    c: Coincident(g20,g29)
    c: Coincident(g21,g30)
    c: Perpendicular(g16,g17)
    c: Coincident(g32,g21)
    c: Coincident(g32,g20)
    c: Perpendicular(g10,g7)
    c: Diameter(g33) = 12.6
    c: Diameter(g34) = 12.6
    c: Diameter(g35) = 12.6
    c: Horizontal(g36)
    c: PointOnObject(g33,g36)
    c: PointOnObject(g34,g36)
    c: DistanceX(g34,g33) = 23
    c: DistanceX(g35,g34) = 23
    c: DistanceX(g33,g36) = 15
    c: Symmetric(g-24,g-24,g36)
    c: Coincident(g36,g35)
FEATURE [Sketcher::SketchObject] Sketch075  label="lato dx pistola"
  ArcFitTolerance = 1e-06
  AttachmentSupport = -> [XZ_Plane]
  ExternalGeometry = -> [Sketch016,Sketch,Sketch058,Sketch074]
  FullyConstrained = true
  MakeInternals = false
  MapMode = 5
  Placement = pos=(0,0,0) rot=(1,0,0;1.5708rad)
  sketch-geometry (61):
    g0: LineSegment StartX=-82.8 StartY=3.2 StartZ=0 EndX=0 EndY=3.2 EndZ=0
    g1: LineSegment StartX=-82.8 StartY=3.2 StartZ=0 EndX=-82.8 EndY=6.2 EndZ=0
    g2: LineSegment [constr] StartX=-107.6 StartY=18 StartZ=0 EndX=-107.6 EndY=20 EndZ=0
    g3: LineSegment [constr] StartX=-132.428 StartY=18 StartZ=0 EndX=-132.428 EndY=20 EndZ=0
    g4: LineSegment StartX=-132.428 StartY=20 StartZ=0 EndX=-107.6 EndY=20 EndZ=0
    g5: ArcOfCircle CenterX=-107.6 CenterY=4 CenterZ=0 NormalX=0 NormalY=0 NormalZ=1 AngleXU=0 Radius=16 StartAngle=0.137937 EndAngle=1.5708
    g6: LineSegment StartX=-82.8 StartY=6.2 StartZ=0 EndX=-91.752 EndY=6.2 EndZ=0
    g7: LineSegment [constr] StartX=-145.743 StartY=8.32624 StartZ=0 EndX=-147.645 EndY=8.94427 EndZ=0
    g8: ArcOfCircle CenterX=-132.428 CenterY=4 CenterZ=0 NormalX=0 NormalY=0 NormalZ=1 AngleXU=0 Radius=16 StartAngle=1.5708 EndAngle=2.82743
    g9: LineSegment StartX=-215.932 StartY=-80.4316 StartZ=0 EndX=-176.685 EndY=-80.4316 EndZ=0
    g10: LineSegment StartX=-147.645 StartY=8.94427 StartZ=0 EndX=-176.685 EndY=-80.4316 EndZ=0
    g11: LineSegment [constr] StartX=-193.988 StartY=-2.33927 StartZ=0 EndX=-192.176 EndY=-3.18451 EndZ=0
    g12: LineSegment [constr] StartX=-217.232 StartY=-52.1862 StartZ=0 EndX=-215.42 EndY=-53.0314 EndZ=0
    g13: LineSegment StartX=-192.176 StartY=-3.18451 StartZ=0 EndX=-215.42 EndY=-53.0314 EndZ=0
    g14: ArcOfCircle CenterX=-184.801 CenterY=-67.3089 CenterZ=0 NormalX=0 NormalY=0 NormalZ=1 AngleXU=0 Radius=33.7833 StartAngle=2.70526 EndAngle=3.54053
    g15: ArcOfCircle CenterX=-207.583 CenterY=4 CenterZ=0 NormalX=0 NormalY=0 NormalZ=1 AngleXU=0 Radius=17 StartAngle=5.84685 EndAngle=7.56663
    g16: LineSegment StartX=-202.765 StartY=20.303 StartZ=0 EndX=-195.887 EndY=39.2 EndZ=0
    g17: LineSegment [constr] StartX=-193.885 StartY=33.0037 StartZ=0 EndX=-197.644 EndY=34.3718 EndZ=0
    g18: LineSegment StartX=-195.887 StartY=39.2 StartZ=0 EndX=0 EndY=39.2 EndZ=0
    g19: LineSegment StartX=0 StartY=3.2 StartZ=0 EndX=0 EndY=39.2 EndZ=0
    g20: LineSegment StartX=-189.939 StartY=31.5672 StartZ=0 EndX=-192.333 EndY=24.9893 EndZ=0
    g21: LineSegment StartX=-196.467 StartY=26.4942 StartZ=0 EndX=-194.073 EndY=33.0721 EndZ=0
    g22: Circle CenterX=-213.443 CenterY=-76.8316 CenterZ=0 NormalX=0 NormalY=0 NormalZ=1 AngleXU=0 Radius=1.8
    g23: Circle CenterX=-179.305 CenterY=-76.8316 CenterZ=0 NormalX=0 NormalY=0 NormalZ=1 AngleXU=0 Radius=1.8
    g24: Circle CenterX=-184.08 CenterY=34.8 CenterZ=0 NormalX=0 NormalY=0 NormalZ=1 AngleXU=0 Radius=1.8
    g25: Circle CenterX=-78.51 CenterY=34.8 CenterZ=0 NormalX=0 NormalY=0 NormalZ=1 AngleXU=0 Radius=1.8
    g26: Circle CenterX=-78.51 CenterY=7.6 CenterZ=0 NormalX=0 NormalY=0 NormalZ=1 AngleXU=0 Radius=1.8
    g27: Circle CenterX=-5.6 CenterY=34.8 CenterZ=0 NormalX=0 NormalY=0 NormalZ=1 AngleXU=0 Radius=1.8
    g28: Circle CenterX=-5.6 CenterY=7.6 CenterZ=0 NormalX=0 NormalY=0 NormalZ=1 AngleXU=0 Radius=1.8
    g29: LineSegment StartX=-190.127 StartY=31.6356 StartZ=0 EndX=-189.939 EndY=31.5672 EndZ=0
    g30: LineSegment StartX=-194.073 StartY=33.0721 StartZ=0 EndX=-193.885 EndY=33.0037 EndZ=0
    g31: LineSegment StartX=-193.885 StartY=33.0037 StartZ=0 EndX=-190.127 EndY=31.6356 EndZ=0
    g32: LineSegment StartX=-196.467 StartY=26.4942 StartZ=0 EndX=-192.333 EndY=24.9893 EndZ=0
    g33: LineSegment [constr] StartX=-4 StartY=21.2 StartZ=0 EndX=-87.91 EndY=21.2 EndZ=0
    g34: GeomPoint [constr] X=-4 Y=21.2 Z=0
    g35: LineSegment [constr] StartX=-15.2 StartY=33.7 StartZ=0 EndX=-15.2 EndY=8.7 EndZ=0
    g36: LineSegment [constr] StartX=-15.2 StartY=33.7 StartZ=0 EndX=-56.2 EndY=33.7 EndZ=0
    g37: LineSegment [constr] StartX=-15.2 StartY=8.7 StartZ=0 EndX=-56.2 EndY=8.7 EndZ=0
    g38: LineSegment [constr] StartX=-56.2 StartY=33.7 StartZ=0 EndX=-56.2 EndY=8.7 EndZ=0
    g39: Circle CenterX=-18.6 CenterY=30.3 CenterZ=0 NormalX=0 NormalY=0 NormalZ=1 AngleXU=0 Radius=3.4
    g40: Circle CenterX=-18.6 CenterY=12.1 CenterZ=0 NormalX=0 NormalY=0 NormalZ=1 AngleXU=0 Radius=3.4
    g41: Circle CenterX=-43.2 CenterY=30.3 CenterZ=0 NormalX=0 NormalY=0 NormalZ=1 AngleXU=0 Radius=3.4
    g42: Circle CenterX=-43.2 CenterY=12.1 CenterZ=0 NormalX=0 NormalY=0 NormalZ=1 AngleXU=0 Radius=3.4
    g43: LineSegment [constr] StartX=-4 StartY=21.2 StartZ=0 EndX=-15.2 EndY=21.2 EndZ=0
    g44: LineSegment [constr] StartX=-15.2 StartY=21.2 StartZ=0 EndX=-36.2 EndY=21.2 EndZ=0
    g45: LineSegment [constr] StartX=-41.5 StartY=16.2 StartZ=0 EndX=-30.9 EndY=16.2 EndZ=0
    g46: LineSegment [constr] StartX=-30.9 StartY=16.2 StartZ=0 EndX=-30.9 EndY=26.2 EndZ=0
    g47: LineSegment [constr] StartX=-30.9 StartY=26.2 StartZ=0 EndX=-41.5 EndY=26.2 EndZ=0
    g48: LineSegment [constr] StartX=-41.5 StartY=26.2 StartZ=0 EndX=-41.5 EndY=16.2 EndZ=0
    g49: GeomPoint [constr] X=-36.2 Y=21.2 Z=0
    g50: Circle CenterX=-36.2 CenterY=21.2 CenterZ=0 NormalX=0 NormalY=0 NormalZ=1 AngleXU=0 Radius=2.8
    g51: LineSegment [constr] StartX=-24.2 StartY=26.7 StartZ=0 EndX=-24.2 EndY=15.7 EndZ=0
    g52: Circle CenterX=-24.2 CenterY=26.7 CenterZ=0 NormalX=0 NormalY=0 NormalZ=1 AngleXU=0 Radius=3
    g53: Circle CenterX=-24.2 CenterY=15.7 CenterZ=0 NormalX=0 NormalY=0 NormalZ=1 AngleXU=0 Radius=3
    g54: GeomPoint X=-18.6 Y=30.3 Z=0
    g55: GeomPoint X=-18.6 Y=12.1 Z=0
    g56: GeomPoint X=-43.2 Y=12.1 Z=0
    g57: GeomPoint X=-43.2 Y=30.3 Z=0
    g58: Circle CenterX=-65 CenterY=21.2 CenterZ=0 NormalX=0 NormalY=0 NormalZ=1 AngleXU=0 Radius=1.5
    g59: Circle CenterX=-42 CenterY=21.2 CenterZ=0 NormalX=0 NormalY=0 NormalZ=1 AngleXU=0 Radius=1.5
    g60: Circle CenterX=-19 CenterY=21.2 CenterZ=0 NormalX=0 NormalY=0 NormalZ=1 AngleXU=0 Radius=1.5
  constraints (149):
    c: Coincident(g0,g-41)
    c: Horizontal(g0)
    c: PointOnObject(g0,g-39)
    c: Coincident(g1,g0)
    c: Vertical(g1)
    c: DistanceY(g1,g1) = 3
    c: Coincident(g2,g-17)
    c: Vertical(g2)
    c: Coincident(g3,g-16)
    c: Vertical(g3)
    c: DistanceY(g2,g2) = 2
    c: DistanceY(g3,g3) = 2
    c: Coincident(g4,g3)
    c: Coincident(g4,g2)
    c: Coincident(g5,g-17)
    c: Coincident(g5,g2)
    c: Coincident(g6,g1)
    c: Horizontal(g6)
    c: Coincident(g6,g5)
    c: Coincident(g7,g-15)
    c: Coincident(g8,g7)
    c: Coincident(g8,g3)
    c: Coincident(g8,g-15)
    c: Horizontal(g9)
    c: DistanceY(g-13,g9) = 2
    c: Coincident(g10,g7)
    c: Parallel(g10,g-14)
    c: Coincident(g9,g10)
    c: Distance(g11) = 2
    c: Coincident(g11,g-11)
    c: Perpendicular(g-11,g11)
    c: Distance(g12) = 2
    c: Coincident(g12,g-12)
    c: Perpendicular(g-11,g12)
    c: Coincident(g13,g11)
    c: Coincident(g13,g12)
    c: Coincident(g14,g-32)
    c: Coincident(g14,g12)
    c: Coincident(g14,g9)
    c: Coincident(g15,g-10)
    c: Coincident(g15,g11)
    c: Parallel(g16,g-22)
    c: Distance(g17) = 4
    c: PointOnObject(g17,g16)
    c: Coincident(g15,g16)
    c: Horizontal(g18)
    c: Coincident(g18,g16)
    c: Coincident(g19,g0)
    c: PointOnObject(g19,g-39)
    c: DistanceY(g19,g-36) = 2
    c: Coincident(g18,g19)
    c: Diameter(g22) = 3.6
    c: Coincident(g22,g-9)
    c: Diameter(g23) = 3.6
    c: Coincident(g23,g-8)
    c: Diameter(g24) = 3.6
    c: Diameter(g25) = 3.6
    c: Diameter(g26) = 3.6
    c: Diameter(g27) = 3.6
    c: Diameter(g28) = 3.6
    c: Coincident(g27,g-4)
    c: Coincident(g28,g-3)
    c: Coincident(g25,g-6)
    c: Coincident(g26,g-5)
    c: Coincident(g24,g-7)
    c: Parallel(g20,g-21)
    c: Equal(g20,g-21)
    c: Parallel(g21,g-19)
    c: Equal(g21,g-19)
    c: Distance(g29) = 0.2
    c: Distance(g30) = 0.2
    c: Parallel(g29,g-20)
    c: Parallel(g31,g-20)
    c: Equal(g31,g-20)
    c: Coincident(g30,g31)
    c: Coincident(g31,g29)
    c: Coincident(g29,g-21)
    c: Parallel(g30,g31)
    c: Coincident(g17,g30)
    c: Coincident(g20,g29)
    c: Coincident(g21,g30)
    c: Perpendicular(g16,g17)
    c: Coincident(g32,g21)
    c: Coincident(g32,g20)
    c: Perpendicular(g10,g7)
    c: Horizontal(g33)
    c: Symmetric(g-24,g-24,g33)
    c: PointOnObject(g33,g-28)
    c: Symmetric(g-24,g-24,g34)
    c: DistanceY(g35,g35) = 25
    c: Symmetric(g35,g35,g33)
    c: Distance(g36) = 41
    c: Coincident(g36,g35)
    c: Horizontal(g36)
    c: Coincident(g37,g35)
    c: Horizontal(g37)
    c: Coincident(g38,g36)
    c: Vertical(g38)
    c: Coincident(g37,g38)
    c: Diameter(g39) = 6.8
    c: Diameter(g40) = 6.8
    c: Tangent(g39,g36)
    c: Tangent(g40,g37)
    c: Tangent(g39,g35)
    c: Tangent(g40,g35)
    c: Diameter(g41) = 6.8
    c: Diameter(g42) = 6.8
    c: Tangent(g41,g36)
    c: Tangent(g42,g37)
    c: DistanceX(g41,g39) = 24.6
    c: DistanceX(g42,g40) = 24.6
    c: Distance(g43) = 11.2
    c: Coincident(g43,g33)
    c: PointOnObject(g43,g33)
    c: PointOnObject(g43,g35)
    c: Distance(g44) = 21
    c: Coincident(g44,g43)
    c: PointOnObject(g44,g33)
    c: Coincident(g45,g46)
    c: Coincident(g46,g47)
    c: Coincident(g47,g48)
    c: Coincident(g48,g45)
    c: Horizontal(g45)
    c: Horizontal(g47)
    c: Vertical(g46)
    c: Vertical(g48)
    c: Symmetric(g47,g45,g49)
    c: Distance(g46,g48) = 10.6
    c: Distance(g45,g47) = 10
    c: Coincident(g49,g44)
    c: Diameter(g50) = 5.6
    c: Coincident(g50,g44)
    c: Distance(g51) = 11
    c: Symmetric(g51,g51,g33)
    c: DistanceX(g51,g43) = 9
    c: Diameter(g52) = 6
    c: Coincident(g52,g51)
    c: Diameter(g53) = 6
    c: Coincident(g53,g51)
    c: Coincident(g40,g55)
    c: Coincident(g39,g54)
    c: Coincident(g41,g57)
    c: Coincident(g42,g56)
    c: Diameter(g58) = 3
    c: Diameter(g59) = 3
    c: Diameter(g60) = 3
    c: Coincident(g58,g-44)
    c: Coincident(g59,g-46)
    c: Coincident(g60,g-45)
FEATURE [Sketcher::SketchObject] Sketch078
  ArcFitTolerance = 1e-06
  AttachmentSupport = -> [XZ_Plane005]
  FullyConstrained = true
  MakeInternals = false
  MapMode = 5
  Placement = pos=(0,0,0) rot=(1,0,0;1.5708rad)
  sketch-geometry (5):
    g0: LineSegment [constr] StartX=0 StartY=5.5 StartZ=0 EndX=0 EndY=-5.5 EndZ=0
    g1: ArcOfCircle CenterX=0 CenterY=5.5 CenterZ=0 NormalX=0 NormalY=0 NormalZ=1 AngleXU=0 Radius=2.7 StartAngle=0 EndAngle=3.14159
    g2: ArcOfCircle CenterX=0 CenterY=-5.5 CenterZ=0 NormalX=0 NormalY=0 NormalZ=1 AngleXU=0 Radius=2.7 StartAngle=3.1416 EndAngle=6.28318
    g3: LineSegment StartX=-2.7 StartY=5.5 StartZ=0 EndX=-2.7 EndY=-5.50001 EndZ=0
    g4: LineSegment StartX=2.7 StartY=5.5 StartZ=0 EndX=2.7 EndY=-5.50001 EndZ=0
  constraints (13):
    c: Distance(g0) = 11
    c: Vertical(g0)
    c: Symmetric(g0,g0,g-1)
    c: Radius(g1) = 2.7
    c: Coincident(g1,g0)
    c: Radius(g2) = 2.7
    c: Coincident(g2,g0)
    c: Vertical(g3)
    c: Vertical(g4)
    c: Coincident(g2,g4)
    c: Coincident(g2,g3)
    c: Tangent(g3,g1) = -1.5708
    c: Tangent(g4,g1) = 1.5708
FEATURE [PartDesign::Pad] Pad002
  Direction = (0,-1,2e-16)
  Length = 0.8
  Length2 = 10
  Placement = pos=(0,0,0) rot=(1,0,0;1.5708rad)
  Profile = -> Sketch078
  ReferenceAxis = -> Sketch078 [N_Axis]
  Refine = true
  Suppressed = false
  Type = 0
FEATURE [Sketcher::SketchObject] Sketch079
  ArcFitTolerance = 1e-06
  AttachmentSupport = -> [XZ_Plane005]
  ExternalGeometry = -> [Sketch078]
  FullyConstrained = true
  MakeInternals = false
  MapMode = 5
  Placement = pos=(0,0,0) rot=(1,0,0;1.5708rad)
  sketch-geometry (2):
    g0: Circle CenterX=-1e-16 CenterY=5.5 CenterZ=0 NormalX=0 NormalY=0 NormalZ=1 AngleXU=0 Radius=2.7
    g1: Circle CenterX=0 CenterY=-5.5 CenterZ=0 NormalX=0 NormalY=0 NormalZ=1 AngleXU=0 Radius=2.7
  constraints (4):
    c: Coincident(g0,g-3)
    c: PointOnObject(g-3,g0)
    c: Coincident(g1,g-4)
    c: Equal(g1,g-4)
FEATURE [PartDesign::Pad] Pad003
  BaseFeature = -> Pad002
  Direction = (0,-1,2e-16)
  Length = 5
  Length2 = 10
  Placement = pos=(0,0,0) rot=(1,0,0;1.5708rad)
  Profile = -> Sketch079
  ReferenceAxis = -> Sketch079 [N_Axis]
  Refine = true
  Suppressed = false
  Type = 0
FEATURE [PartDesign::Fillet] Fillet001
  Base = -> Pad003 [Edge16,Edge14]
  BaseFeature = -> Pad003
  Placement = pos=(0,0,0) rot=(1,0,0;1.5708rad)
  Radius = 0.4
  Refine = true
  SupportTransform = false
  Suppressed = false
  UseAllEdges = false
FEATURE [PartDesign::Body] Body005  label="pulsanti lato destro"
  AllowCompound = false
  Group = -> [Sketch078,Pad002,Sketch079,Pad003,Fillet001]
  Origin = -> Origin005
  Tip = -> Fillet001
FEATURE [PartDesign::SubShapeBinder] Binder
  BindCopyOnChange = 0
  BindMode = 0
  ClaimChildren = false
  Context = -> Body006 [Binder.]
  Fuse = false
  MakeFace = true
  OffsetFill = false
  OffsetIntersection = false
  OffsetJoinType = 0
  OffsetOpenResult = false
  PartialLoad = false
  Refine = true
  Relative = true
  Support = -> [Body[Sketch074.]]
  _Version = 2
FEATURE [PartDesign::SubShapeBinder] Binder001
  BindCopyOnChange = 0
  BindMode = 0
  ClaimChildren = false
  Context = -> Body007 [Binder001.]
  Fuse = false
  MakeFace = true
  OffsetFill = false
  OffsetIntersection = false
  OffsetJoinType = 0
  OffsetOpenResult = false
  PartialLoad = false
  Refine = true
  Relative = true
  Support = -> [Body[Sketch075.]]
  _Version = 2
FEATURE [Mesh::Feature] logo_per_PCB_definitivo_positivo
  Placement = pos=(-191,17,-66) rot=(0,1,1;0rad)
FEATURE [Sketcher::SketchObject] Sketch114  label="Sketch114 - base lato DX"
  ArcFitTolerance = 1e-06
  AttachmentSupport = -> [Binder001]
  ExternalGeometry = -> [Binder001]
  FullyConstrained = true
  MakeInternals = false
  MapMode = 5
  Placement = pos=(0,1e-15,0) rot=(0,0.707107,0.707107;3.14159rad)
  sketch-geometry (30):
    g0: Circle CenterX=5.6 CenterY=34.8 CenterZ=0 NormalX=0 NormalY=0 NormalZ=1 AngleXU=0 Radius=1.8
    g1: Circle CenterX=5.6 CenterY=7.6 CenterZ=0 NormalX=0 NormalY=0 NormalZ=1 AngleXU=0 Radius=1.8
    g2: Circle CenterX=24.2 CenterY=26.7 CenterZ=0 NormalX=0 NormalY=0 NormalZ=1 AngleXU=0 Radius=3
    g3: Circle CenterX=24.2 CenterY=15.7 CenterZ=0 NormalX=0 NormalY=0 NormalZ=1 AngleXU=0 Radius=3
    g4: Circle CenterX=36.2 CenterY=21.2 CenterZ=0 NormalX=0 NormalY=0 NormalZ=1 AngleXU=0 Radius=2.8
    g5: Circle CenterX=78.51 CenterY=34.8 CenterZ=0 NormalX=0 NormalY=0 NormalZ=1 AngleXU=0 Radius=1.8
    g6: Circle CenterX=78.51 CenterY=7.6 CenterZ=0 NormalX=0 NormalY=0 NormalZ=1 AngleXU=0 Radius=1.8
    g7: Circle CenterX=184.08 CenterY=34.8 CenterZ=0 NormalX=0 NormalY=0 NormalZ=1 AngleXU=0 Radius=1.8
    g8: Circle CenterX=213.443 CenterY=-76.8316 CenterZ=0 NormalX=0 NormalY=0 NormalZ=1 AngleXU=0 Radius=1.8
    g9: Circle CenterX=179.305 CenterY=-76.8316 CenterZ=0 NormalX=0 NormalY=0 NormalZ=1 AngleXU=0 Radius=1.8
    g10: ArcOfCircle [constr] CenterX=132.428 CenterY=4 CenterZ=0 NormalX=0 NormalY=0 NormalZ=1 AngleXU=0 Radius=16 StartAngle=0.314159 EndAngle=1.5708
    g11: ArcOfCircle CenterX=107.6 CenterY=4 CenterZ=0 NormalX=0 NormalY=0 NormalZ=1 AngleXU=0 Radius=16 StartAngle=1.5708 EndAngle=3.00366
    g12: ArcOfCircle CenterX=207.583 CenterY=4 CenterZ=0 NormalX=0 NormalY=0 NormalZ=1 AngleXU=0 Radius=17 StartAngle=1.85815 EndAngle=3.57792
    g13: ArcOfCircle CenterX=184.801 CenterY=-67.3089 CenterZ=0 NormalX=0 NormalY=0 NormalZ=1 AngleXU=0 Radius=33.7833 StartAngle=5.88425 EndAngle=6.71952
    g14: LineSegment StartX=0 StartY=39.2 StartZ=0 EndX=0 EndY=3.2 EndZ=0
    g15: LineSegment StartX=0 StartY=3.2 StartZ=0 EndX=82.8 EndY=3.2 EndZ=0
    g16: LineSegment StartX=82.8 StartY=3.2 StartZ=0 EndX=82.8 EndY=6.2 EndZ=0
    g17: LineSegment StartX=82.8 StartY=6.2 StartZ=0 EndX=91.752 EndY=6.2 EndZ=0
    g18: LineSegment StartX=107.6 StartY=20 StartZ=0 EndX=132.428 EndY=20 EndZ=0
    g19: LineSegment StartX=147.645 StartY=8.94427 StartZ=0 EndX=176.685 EndY=-80.4316 EndZ=0
    g20: LineSegment StartX=176.685 StartY=-80.4316 StartZ=0 EndX=215.932 EndY=-80.4316 EndZ=0
    g21: LineSegment StartX=215.42 StartY=-53.0314 StartZ=0 EndX=192.176 EndY=-3.18451 EndZ=0
    g22: LineSegment StartX=202.765 StartY=20.303 StartZ=0 EndX=195.887 EndY=39.2 EndZ=0
    g23: LineSegment StartX=195.887 StartY=39.2 StartZ=0 EndX=0 EndY=39.2 EndZ=0
    g24: LineSegment StartX=196.467 StartY=26.4942 StartZ=0 EndX=194.073 EndY=33.0721 EndZ=0
    g25: LineSegment StartX=194.073 StartY=33.0721 StartZ=0 EndX=189.939 EndY=31.5672 EndZ=0
    g26: LineSegment StartX=189.939 StartY=31.5672 StartZ=0 EndX=192.333 EndY=24.9893 EndZ=0
    g27: LineSegment StartX=192.333 StartY=24.9893 StartZ=0 EndX=196.467 EndY=26.4942 EndZ=0
    g28: LineSegment StartX=132.428 StartY=20 StartZ=0 EndX=144.053 EndY=20 EndZ=0
    g29: LineSegment StartX=144.053 StartY=20 StartZ=0 EndX=147.645 EndY=8.94427 EndZ=0
  constraints (65):
    c: Equal(g0,g-25)
    c: Equal(g2,g-29)
    c: Equal(g3,g-30)
    c: Equal(g4,g-28)
    c: Equal(g1,g-26)
    c: Coincident(g0,g-25)
    c: Coincident(g1,g-26)
    c: Coincident(g2,g-29)
    c: Coincident(g3,g-30)
    c: Coincident(g4,g-28)
    c: Equal(g5,g-23)
    c: Equal(g6,g-24)
    c: Coincident(g5,g-23)
    c: Coincident(g6,g-24)
    c: Equal(g7,g-20)
    c: Coincident(g7,g-20)
    c: Equal(g9,g-22)
    c: Coincident(g9,g-22)
    c: Equal(g8,g-21)
    c: Coincident(g8,g-21)
    c: Equal(g13,g-12)
    c: Equal(g12,g-14)
    c: Equal(g10,g-9)
    c: Equal(g11,g-7)
    c: Coincident(g14,g-27)
    c: Coincident(g14,g-27)
    c: Coincident(g15,g14)
    c: Coincident(g15,g-5)
    c: Coincident(g16,g15)
    c: Coincident(g16,g-6)
    c: Coincident(g17,g16)
    c: Coincident(g17,g-7)
    c: Coincident(g11,g17)
    c: Coincident(g11,g-8)
    c: Coincident(g18,g11)
    c: Coincident(g18,g-9)
    c: Coincident(g10,g18)
    c: Coincident(g10,g-10)
    c: Coincident(g19,g10)
    c: Coincident(g19,g-11)
    c: Coincident(g20,g19)
    c: Coincident(g20,g-12)
    c: Coincident(g13,g20)
    c: Coincident(g13,g-13)
    c: Coincident(g21,g13)
    c: Coincident(g21,g-14)
    c: Coincident(g12,g21)
    c: Coincident(g12,g-15)
    c: Coincident(g22,g12)
    c: Coincident(g22,g-15)
    c: Coincident(g23,g22)
    c: Coincident(g23,g14)
    c: Coincident(g24,g-18)
    c: Coincident(g24,g-16)
    c: Coincident(g25,g24)
    c: Coincident(g25,g-19)
    c: Coincident(g26,g25)
    c: Coincident(g26,g-19)
    c: Coincident(g27,g26)
    c: Coincident(g27,g24)
    c: Coincident(g29,g10)
    c: Coincident(g28,g10)
    c: Coincident(g29,g28)
    c: Parallel(g28,g18)
    c: Parallel(g29,g19)
FEATURE [PartDesign::Pad] Pad011
  Direction = (0,1,-2e-16)
  Length = 2
  Length2 = 10
  Profile = -> Sketch114
  ReferenceAxis = -> Sketch114 [N_Axis]
  Refine = true
  Reversed = true
  Suppressed = false
  Type = 0
FEATURE [Sketcher::SketchObject] Sketch115
  ArcFitTolerance = 1e-06
  AttachmentSupport = -> [Pad011]
  ExternalGeometry = -> [Binder001]
  FullyConstrained = true
  MakeInternals = false
  MapMode = 5
  Placement = pos=(0,1.7e-15,0) rot=(0,0.707107,0.707107;3.14159rad)
  sketch-geometry (4):
    g0: ArcOfCircle CenterX=24.2 CenterY=26.7 CenterZ=0 NormalX=0 NormalY=0 NormalZ=1 AngleXU=0 Radius=3 StartAngle=4.48384e-08 EndAngle=3.14159
    g1: ArcOfCircle CenterX=24.2 CenterY=15.7 CenterZ=0 NormalX=0 NormalY=0 NormalZ=1 AngleXU=0 Radius=3 StartAngle=3.14159 EndAngle=6.28318
    g2: LineSegment StartX=21.2 StartY=26.7 StartZ=0 EndX=21.2 EndY=15.7 EndZ=0
    g3: LineSegment StartX=27.2 StartY=26.7 StartZ=0 EndX=27.2 EndY=15.7 EndZ=0
  constraints (12):
    c: Equal(g1,g-4)
    c: Equal(g0,g-3)
    c: Coincident(g0,g-3)
    c: Coincident(g1,g-4)
    c: Vertical(g2)
    c: Vertical(g3)
    c: Tangent(g3,g-3)
    c: Tangent(g2,g-3)
    c: Coincident(g0,g2)
    c: Coincident(g0,g3)
    c: Coincident(g1,g2)
    c: Coincident(g3,g1)
FEATURE [Sketcher::SketchObject] Sketch117  label="Sketch117 - fori per inserto M3 x 3 x 4.5"
  ArcFitTolerance = 1e-06
  AttachmentSupport = -> [Pad011]
  ExternalGeometry = -> [Binder001]
  FullyConstrained = true
  MakeInternals = false
  MapMode = 5
  Placement = pos=(0,1.7e-15,0) rot=(0,0.707107,0.707107;3.14159rad)
  sketch-geometry (4):
    g0: Circle CenterX=43.2 CenterY=30.3 CenterZ=0 NormalX=0 NormalY=0 NormalZ=1 AngleXU=0 Radius=2.25
    g1: Circle CenterX=43.2 CenterY=12.1 CenterZ=0 NormalX=0 NormalY=0 NormalZ=1 AngleXU=0 Radius=2.25
    g2: Circle CenterX=18.6 CenterY=30.3 CenterZ=0 NormalX=0 NormalY=0 NormalZ=1 AngleXU=0 Radius=2.25
    g3: Circle CenterX=18.6 CenterY=12.1 CenterZ=0 NormalX=0 NormalY=0 NormalZ=1 AngleXU=0 Radius=2.25
  constraints (8):
    c: Diameter(g0) = 4.5
    c: Diameter(g1) = 4.5
    c: Diameter(g2) = 4.5
    c: Diameter(g3) = 4.5
    c: Coincident(g2,g-3)
    c: Coincident(g3,g-6)
    c: Coincident(g0,g-4)
    c: Coincident(g1,g-5)
FEATURE [Sketcher::SketchObject] Sketch118
  ArcFitTolerance = 1e-06
  AttachmentSupport = -> [Pad011]
  ExternalGeometry = -> [Binder001]
  FullyConstrained = true
  MakeInternals = false
  MapMode = 5
  Placement = pos=(0,-2,0) rot=(1,0,0;1.5708rad)
  sketch-geometry (12):
    g0: Circle CenterX=-78.51 CenterY=34.8 CenterZ=0 NormalX=0 NormalY=0 NormalZ=1 AngleXU=0 Radius=1.8
    g1: Circle CenterX=-78.51 CenterY=7.6 CenterZ=0 NormalX=0 NormalY=0 NormalZ=1 AngleXU=0 Radius=1.8
    g2: Circle CenterX=-5.6 CenterY=34.8 CenterZ=0 NormalX=0 NormalY=0 NormalZ=1 AngleXU=0 Radius=1.8
    g3: Circle CenterX=-5.6 CenterY=7.6 CenterZ=0 NormalX=0 NormalY=0 NormalZ=1 AngleXU=0 Radius=1.8
    g4: LineSegment StartX=0 StartY=39.2 StartZ=0 EndX=0 EndY=3.2 EndZ=0
    g5: LineSegment StartX=0 StartY=3.2 StartZ=0 EndX=-82.8 EndY=3.2 EndZ=0
    g6: LineSegment StartX=-82.8 StartY=3.2 StartZ=0 EndX=-82.8 EndY=39.2 EndZ=0
    g7: LineSegment StartX=-82.8 StartY=39.2 StartZ=0 EndX=0 EndY=39.2 EndZ=0
    g8: ArcOfCircle CenterX=-65 CenterY=21.2 CenterZ=0 NormalX=0 NormalY=0 NormalZ=1 AngleXU=0 Radius=10 StartAngle=1.5708 EndAngle=4.71239
    g9: ArcOfCircle CenterX=-19 CenterY=21.2 CenterZ=0 NormalX=0 NormalY=0 NormalZ=1 AngleXU=0 Radius=10 StartAngle=4.71239 EndAngle=7.85398
    g10: LineSegment StartX=-65 StartY=31.2 StartZ=0 EndX=-19 EndY=31.2 EndZ=0
    g11: LineSegment StartX=-65 StartY=11.2 StartZ=0 EndX=-19 EndY=11.2 EndZ=0
  constraints (25):
    c: Equal(g2,g-5)
    c: Equal(g3,g-7)
    c: Equal(g1,g-6)
    c: Equal(g0,g-4)
    c: Coincident(g0,g-4)
    c: Coincident(g1,g-6)
    c: Coincident(g3,g-7)
    c: Coincident(g2,g-5)
    c: Coincident(g4,g-8)
    c: Coincident(g4,g-9)
    c: Coincident(g5,g4)
    c: Coincident(g5,g-10)
    c: Coincident(g6,g5)
    c: PointOnObject(g6,g-3)
    c: Vertical(g6)
    c: Coincident(g7,g6)
    c: Coincident(g7,g4)
    c: Tangent(g8,g10) = 1.5708
    c: Tangent(g8,g11) = -1.5708
    c: Tangent(g9,g10) = 1.5708
    c: Tangent(g9,g11) = -1.5708
    c: Equal(g8,g9)
    c: Radius(g8) = 10
    c: Coincident(g8,g-11)
    c: Coincident(g9,g-12)
FEATURE [Sketcher::SketchObject] Sketch120
  ArcFitTolerance = 1e-06
  AttachmentSupport = -> [Pad011]
  ExternalGeometry = -> [Binder001]
  FullyConstrained = true
  MakeInternals = false
  MapMode = 5
  Placement = pos=(0,-2,0) rot=(1,0,0;1.5708rad)
  sketch-geometry (4):
    g0: LineSegment StartX=-137.815 StartY=39.2 StartZ=0 EndX=-142.655 EndY=24.303 EndZ=0
    g1: LineSegment StartX=-137.815 StartY=39.2 StartZ=0 EndX=-110.815 EndY=39.2 EndZ=0
    g2: LineSegment StartX=-142.655 StartY=24.303 StartZ=0 EndX=-110.815 EndY=24.303 EndZ=0
    g3: ArcOfCircle CenterX=-92.2534 CenterY=31.7515 CenterZ=0 NormalX=0 NormalY=0 NormalZ=1 AngleXU=0 Radius=20 StartAngle=2.75997 EndAngle=3.52321
  constraints (12):
    c: PointOnObject(g0,g-3)
    c: Coincident(g1,g0)
    c: PointOnObject(g1,g-3)
    c: Coincident(g2,g0)
    c: Horizontal(g2)
    c: Tangent(g0,g-4)
    c: Vertical(g2,g1)
    c: DistanceX(g1,g1) = 27
    c: DistanceY(g-6,g0) = 4
    c: Radius(g3) = 20
    c: Coincident(g3,g1)
    c: Coincident(g3,g2)
FEATURE [Sketcher::SketchObject] Sketch121
  ArcFitTolerance = 1e-06
  AttachmentSupport = -> [Pad011]
  ExternalGeometry = -> [Binder001]
  FullyConstrained = true
  MakeInternals = false
  MapMode = 5
  Placement = pos=(0,-2,0) rot=(1,0,0;1.5708rad)
  sketch-geometry (15):
    g0: LineSegment StartX=-137.815 StartY=39.2 StartZ=0 EndX=-143.955 EndY=20.303 EndZ=0
    g1: LineSegment StartX=-143.955 StartY=20.303 StartZ=0 EndX=-190.141 EndY=20.303 EndZ=0
    g2: LineSegment StartX=-190.141 StartY=20.303 StartZ=0 EndX=-186.139 EndY=31.3 EndZ=0
    g3: LineSegment StartX=-178.754 StartY=39.2 StartZ=0 EndX=-180.791 EndY=33.6029 EndZ=0
    g4: ArcOfCircle CenterX=-184.08 CenterY=34.8 CenterZ=0 NormalX=0 NormalY=0 NormalZ=1 AngleXU=0 Radius=3.5 StartAngle=4.71239 EndAngle=5.93412
    g5: LineSegment StartX=-184.08 StartY=31.3 StartZ=0 EndX=-186.139 EndY=31.3 EndZ=0
    g6: LineSegment StartX=-137.815 StartY=39.2 StartZ=0 EndX=-156.815 EndY=39.2 EndZ=0
    g7: LineSegment StartX=-168.815 StartY=39.2 StartZ=0 EndX=-178.754 EndY=39.2 EndZ=0
    g8: LineSegment StartX=-157.815 StartY=39.2 StartZ=0 EndX=-167.815 EndY=39.2 EndZ=0
    g9: LineSegment StartX=-168.815 StartY=31.2 StartZ=0 EndX=-156.815 EndY=31.2 EndZ=0
    g10: LineSegment StartX=-167.436 StartY=36.2 StartZ=0 EndX=-157.436 EndY=36.2 EndZ=0
    g11: ArcOfCircle CenterX=-176.411 CenterY=35.2 CenterZ=0 NormalX=0 NormalY=0 NormalZ=1 AngleXU=0 Radius=20 StartAngle=6.08183 EndAngle=6.48454
    g12: ArcOfCircle CenterX=-188.411 CenterY=35.2 CenterZ=0 NormalX=0 NormalY=0 NormalZ=1 AngleXU=0 Radius=20 StartAngle=6.08183 EndAngle=6.48454
    g13: ArcOfCircle CenterX=-177.411 CenterY=35.2 CenterZ=0 NormalX=0 NormalY=0 NormalZ=1 AngleXU=0 Radius=20 StartAngle=0.0500209 EndAngle=0.201358
    g14: ArcOfCircle CenterX=-187.411 CenterY=35.2 CenterZ=0 NormalX=0 NormalY=0 NormalZ=1 AngleXU=0 Radius=20 StartAngle=0.0500209 EndAngle=0.201358
  constraints (46):
    c: PointOnObject(g0,g-3)
    c: Tangent(g0,g-5)
    c: Coincident(g1,g0)
    c: Horizontal(g1)
    c: Coincident(g2,g1)
    c: PointOnObject(g3,g-3)
    c: Parallel(g3,g-6)
    c: Parallel(g2,g-6)
    c: Radius(g4) = 3.5
    c: Coincident(g4,g-7)
    c: Tangent(g3,g4) = 1.5708
    c: Horizontal(g5)
    c: Tangent(g5,g4) = 1.5708
    c: DistanceX(g-8,g5) = 3.8
    c: Coincident(g2,g5)
    c: Coincident(g6,g0)
    c: PointOnObject(g6,g-3)
    c: DistanceX(g6,g6) = 19
    c: PointOnObject(g7,g-3)
    c: DistanceX(g7,g6) = 12
    c: Coincident(g7,g3)
    c: PointOnObject(g8,g-3)
    c: PointOnObject(g8,g-3)
    c: DistanceX(g8,g8) = 10
    c: DistanceX(g8,g6) = 1
    c: Horizontal(g9)
    c: Vertical(g7,g9)
    c: Vertical(g6,g9)
    c: DistanceY(g9,g7) = 8
    c: Horizontal(g10)
    c: Equal(g8,g10)
    c: DistanceY(g10,g8) = 3
    c: Radius(g11) = 20
    c: Coincident(g11,g6)
    c: Coincident(g11,g9)
    c: Radius(g12) = 20
    c: Coincident(g12,g7)
    c: Coincident(g12,g9)
    c: Equal(g13,g11)
    c: Coincident(g13,g8)
    c: Coincident(g13,g10)
    c: Horizontal(g13,g11)
    c: Equal(g14,g12)
    c: Coincident(g14,g8)
    c: Coincident(g14,g10)
    c: Horizontal(g1,g-6)
FEATURE [Sketcher::SketchObject] Sketch122
  ArcFitTolerance = 1e-06
  AttachmentSupport = -> [Pad011]
  ExternalGeometry = -> [Binder001]
  FullyConstrained = true
  MakeInternals = false
  MapMode = 5
  Placement = pos=(0,-2,0) rot=(1,0,0;1.5708rad)
  sketch-geometry (8):
    g0: LineSegment StartX=-202.765 StartY=20.303 StartZ=0 EndX=-143.955 EndY=20.303 EndZ=0
    g1: ArcOfCircle CenterX=-184.801 CenterY=-67.3089 CenterZ=0 NormalX=0 NormalY=0 NormalZ=1 AngleXU=0 Radius=33.7833 StartAngle=2.70526 EndAngle=3.54053
    g2: LineSegment StartX=-176.685 StartY=-80.4316 StartZ=0 EndX=-215.932 EndY=-80.4316 EndZ=0
    g3: LineSegment StartX=-215.42 StartY=-53.0315 StartZ=0 EndX=-192.176 EndY=-3.18454 EndZ=0
    g4: ArcOfCircle CenterX=-207.583 CenterY=4 CenterZ=0 NormalX=0 NormalY=0 NormalZ=1 AngleXU=0 Radius=17 StartAngle=5.84685 EndAngle=7.56663
    g5: Circle CenterX=-213.443 CenterY=-76.8316 CenterZ=0 NormalX=0 NormalY=0 NormalZ=1 AngleXU=0 Radius=3
    g6: Circle CenterX=-179.305 CenterY=-76.8316 CenterZ=0 NormalX=0 NormalY=0 NormalZ=1 AngleXU=0 Radius=3
    g7: LineSegment StartX=-143.955 StartY=20.303 StartZ=0 EndX=-176.685 EndY=-80.4316 EndZ=0
  constraints (18):
    c: Coincident(g0,g-6)
    c: Coincident(g1,g-7)
    c: Coincident(g1,g-8)
    c: Coincident(g2,g1)
    c: Tangent(g3,g-5)
    c: Coincident(g4,g-6)
    c: Coincident(g4,g0)
    c: Coincident(g3,g4)
    c: Coincident(g1,g3)
    c: Diameter(g5) = 6
    c: Diameter(g6) = 6
    c: Coincident(g5,g-9)
    c: Coincident(g6,g-10)
    c: Horizontal(g0)
    c: Horizontal(g2)
    c: Coincident(g7,g0)
    c: Coincident(g7,g2)
    c: Tangent(g7,g-4)
FEATURE [Sketcher::SketchObject] Sketch123
  ArcFitTolerance = 1e-06
  AttachmentSupport = -> [Pad011]
  ExternalGeometry = -> [Binder001]
  FullyConstrained = true
  MakeInternals = false
  MapMode = 5
  Placement = pos=(0,-2,0) rot=(1,0,0;1.5708rad)
  sketch-geometry (4):
    g0: LineSegment StartX=-108 StartY=36.8 StartZ=0 EndX=-90 EndY=36.8 EndZ=0
    g1: LineSegment StartX=-108 StartY=36.8 StartZ=0 EndX=-108 EndY=26.8 EndZ=0
    g2: LineSegment StartX=-108 StartY=26.8 StartZ=0 EndX=-90 EndY=26.8 EndZ=0
    g3: ArcOfCircle CenterX=-94 CenterY=31.8 CenterZ=0 NormalX=0 NormalY=0 NormalZ=1 AngleXU=0 Radius=6.40312 StartAngle=5.38713 EndAngle=7.17924
  constraints (13):
    c: Horizontal(g0)
    c: Coincident(g1,g0)
    c: Vertical(g1)
    c: Coincident(g2,g1)
    c: Horizontal(g2)
    c: DistanceX(g0,g0) = 18
    c: DistanceY(g1,g1) = 10
    c: Equal(g0,g2)
    c: DistanceX(g0,g-3) = 90
    c: DistanceY(g0,g-3) = 2.4
    c: Coincident(g3,g0)
    c: Coincident(g3,g2)
    c: DistanceX(g3,g0) = 4
FEATURE [PartDesign::Chamfer] Chamfer014
  Angle = 45
  Base = -> Pad011 [Edge80,Edge4,Edge7]
  BaseFeature = -> Pad011
  ChamferType = 0
  FlipDirection = false
  Refine = true
  Size = 1.9
  Size2 = 1
  SupportTransform = false
  Suppressed = false
  UseAllEdges = false
FEATURE [PartDesign::Pocket] Pocket006
  BaseFeature = -> Chamfer014
  Direction = (0,-1,2e-16)
  Length = 1.2
  Length2 = 5
  Profile = -> Sketch115
  ReferenceAxis = -> Sketch115 [N_Axis]
  Refine = true
  Suppressed = false
  Type = 0
FEATURE [Sketcher::SketchObject] Sketch116  label="Sketch116 - pieno per inserto M3 x 3 x 4,5"
  ArcFitTolerance = 1e-06
  AttachmentSupport = -> [Pocket006]
  ExternalGeometry = -> [Binder001]
  FullyConstrained = true
  MakeInternals = false
  MapMode = 5
  Placement = pos=(0,1.7e-15,0) rot=(0,0.707107,0.707107;3.14159rad)
  sketch-geometry (4):
    g0: Circle CenterX=43.2 CenterY=30.3 CenterZ=0 NormalX=0 NormalY=0 NormalZ=1 AngleXU=0 Radius=3.4
    g1: Circle CenterX=43.2 CenterY=12.1 CenterZ=0 NormalX=0 NormalY=0 NormalZ=1 AngleXU=0 Radius=3.4
    g2: Circle CenterX=18.6 CenterY=30.3 CenterZ=0 NormalX=0 NormalY=0 NormalZ=1 AngleXU=0 Radius=3.4
    g3: Circle CenterX=18.6 CenterY=12.1 CenterZ=0 NormalX=0 NormalY=0 NormalZ=1 AngleXU=0 Radius=3.4
  constraints (8):
    c: Diameter(g0) = 6.8
    c: Diameter(g1) = 6.8
    c: Diameter(g2) = 6.8
    c: Diameter(g3) = 6.8
    c: Coincident(g2,g-3)
    c: Coincident(g0,g-4)
    c: Coincident(g3,g-6)
    c: Coincident(g1,g-5)
FEATURE [PartDesign::Pad] Pad012
  BaseFeature = -> Pocket006
  Direction = (0,1,-2e-16)
  Length = 2.4
  Length2 = 10
  Profile = -> Sketch116
  ReferenceAxis = -> Sketch116 [N_Axis]
  Refine = true
  Suppressed = false
  Type = 0
FEATURE [PartDesign::Pocket] Pocket007
  BaseFeature = -> Pad012
  Direction = (0,-1,2e-16)
  Length = 0.6
  Length2 = 2.4
  Profile = -> Sketch117
  ReferenceAxis = -> Sketch117 [N_Axis]
  Refine = true
  Suppressed = false
  Type = 4
FEATURE [PartDesign::Pad] Pad013
  BaseFeature = -> Pocket007
  Direction = (0,-1,2e-16)
  Length = 1.6
  Length2 = 10
  Profile = -> Sketch118
  ReferenceAxis = -> Sketch118 [N_Axis]
  Refine = true
  Suppressed = false
  Type = 0
FEATURE [Sketcher::SketchObject] Sketch119
  ArcFitTolerance = 1e-06
  AttachmentSupport = -> [Pad013]
  ExternalGeometry = -> [Binder001]
  FullyConstrained = true
  MakeInternals = false
  MapMode = 5
  Placement = pos=(0,-3.6,0) rot=(1,0,0;1.5708rad)
  sketch-geometry (21):
    g0: LineSegment [constr] StartX=-82.8 StartY=3.2 StartZ=0 EndX=-82.8 EndY=39.2 EndZ=0
    g1: ArcOfCircle CenterX=-78.51 CenterY=34.8 CenterZ=0 NormalX=0 NormalY=0 NormalZ=1 AngleXU=0 Radius=3.5 StartAngle=4.71239 EndAngle=6.28319
    g2: ArcOfCircle CenterX=-78.51 CenterY=7.6 CenterZ=0 NormalX=0 NormalY=0 NormalZ=1 AngleXU=0 Radius=3.5 StartAngle=0 EndAngle=1.5708
    g3: ArcOfCircle CenterX=-5.6 CenterY=34.8 CenterZ=0 NormalX=0 NormalY=0 NormalZ=1 AngleXU=0 Radius=3.5 StartAngle=3.14159 EndAngle=4.71239
    g4: ArcOfCircle CenterX=-5.6 CenterY=7.6 CenterZ=0 NormalX=0 NormalY=0 NormalZ=1 AngleXU=0 Radius=3.5 StartAngle=1.5708 EndAngle=3.14159
    g5: LineSegment StartX=0 StartY=39.2 StartZ=0 EndX=0 EndY=31.3 EndZ=0
    g6: LineSegment StartX=0 StartY=39.2 StartZ=0 EndX=-9.1 EndY=39.2 EndZ=0
    g7: LineSegment StartX=0 StartY=3.2 StartZ=0 EndX=0 EndY=11.1 EndZ=0
    g8: LineSegment StartX=0 StartY=3.2 StartZ=0 EndX=-9.1 EndY=3.2 EndZ=0
    g9: LineSegment StartX=-82.8 StartY=3.2 StartZ=0 EndX=-75.01 EndY=3.2 EndZ=0
    g10: LineSegment StartX=-82.8 StartY=3.2 StartZ=0 EndX=-82.8 EndY=11.1 EndZ=0
    g11: LineSegment StartX=-82.8 StartY=39.2 StartZ=0 EndX=-82.8 EndY=31.3 EndZ=0
    g12: LineSegment StartX=-82.8 StartY=39.2 StartZ=0 EndX=-75.01 EndY=39.2 EndZ=0
    g13: LineSegment StartX=-82.8 StartY=31.3 StartZ=0 EndX=-78.51 EndY=31.3 EndZ=0
    g14: LineSegment StartX=-75.01 StartY=39.2 StartZ=0 EndX=-75.01 EndY=34.8 EndZ=0
    g15: LineSegment StartX=-82.8 StartY=11.1 StartZ=0 EndX=-78.51 EndY=11.1 EndZ=0
    g16: LineSegment StartX=-75.01 StartY=3.2 StartZ=0 EndX=-75.01 EndY=7.6 EndZ=0
    g17: LineSegment StartX=-9.1 StartY=39.2 StartZ=0 EndX=-9.1 EndY=34.8 EndZ=0
    g18: LineSegment StartX=0 StartY=31.3 StartZ=0 EndX=-5.6 EndY=31.3 EndZ=0
    g19: LineSegment StartX=0 StartY=11.1 StartZ=0 EndX=-5.6 EndY=11.1 EndZ=0
    g20: LineSegment StartX=-9.1 StartY=3.2 StartZ=0 EndX=-9.1 EndY=7.6 EndZ=0
  constraints (51):
    c: Coincident(g0,g-10)
    c: PointOnObject(g0,g-8)
    c: Vertical(g0)
    c: Coincident(g1,g-3)
    c: Coincident(g2,g-4)
    c: Coincident(g3,g-5)
    c: Coincident(g4,g-6)
    c: Radius(g4) = 3.5
    c: Radius(g3) = 3.5
    c: Radius(g1) = 3.5
    c: Radius(g2) = 3.5
    c: Coincident(g5,g-9)
    c: PointOnObject(g5,g-9)
    c: Coincident(g6,g5)
    c: PointOnObject(g6,g-8)
    c: Coincident(g7,g-9)
    c: PointOnObject(g7,g-9)
    c: Coincident(g8,g7)
    c: PointOnObject(g8,g-7)
    c: Coincident(g9,g0)
    c: PointOnObject(g9,g-7)
    c: Coincident(g10,g0)
    c: PointOnObject(g10,g0)
    c: Coincident(g11,g0)
    c: PointOnObject(g11,g0)
    c: Coincident(g12,g0)
    c: PointOnObject(g12,g-8)
    c: Coincident(g13,g11)
    c: Horizontal(g13)
    c: Coincident(g14,g12)
    c: Vertical(g14)
    c: Coincident(g15,g10)
    c: Horizontal(g15)
    c: Coincident(g16,g9)
    c: Vertical(g16)
    c: Coincident(g17,g6)
    c: Vertical(g17)
    c: Coincident(g18,g5)
    c: Horizontal(g18)
    c: Coincident(g19,g7)
    c: Horizontal(g19)
    c: Coincident(g20,g8)
    c: Vertical(g20)
    c: Tangent(g20,g4) = 1.5708
    c: Tangent(g4,g19) = -1.5708
    c: Tangent(g18,g3) = 1.5708
    c: Tangent(g3,g17) = -1.5708
    c: Tangent(g13,g1) = -1.5708
    c: Tangent(g1,g14) = 1.5708
    c: Tangent(g16,g2) = -1.5708
    c: Tangent(g2,g15) = 1.5708
FEATURE [PartDesign::Pocket] Pocket008
  BaseFeature = -> Pad013
  Direction = (0,1,-2e-16)
  Length = 1.6
  Length2 = 5
  Profile = -> Sketch119
  ReferenceAxis = -> Sketch119 [N_Axis]
  Refine = true
  Suppressed = false
  Type = 0
FEATURE [PartDesign::Pad] Pad017
  BaseFeature = -> Pocket008
  Direction = (0,-1,2e-16)
  Length = 1.6
  Length2 = 10
  Profile = -> Sketch123
  ReferenceAxis = -> Sketch123 [N_Axis]
  Refine = true
  Suppressed = false
  Type = 0
FEATURE [Sketcher::SketchObject] Sketch125
  ArcFitTolerance = 1e-06
  AttachmentSupport = -> [Pad017]
  ExternalGeometry = -> [Pad017]
  FullyConstrained = true
  MakeInternals = false
  MapMode = 5
  Placement = pos=(0,-3.6,8e-16) rot=(1,0,0;1.5708rad)
  sketch-geometry (20):
    g0: LineSegment StartX=-108 StartY=35.8 StartZ=0 EndX=-108 EndY=35 EndZ=0
    g1: LineSegment StartX=-108 StartY=35 StartZ=0 EndX=-97 EndY=35 EndZ=0
    g2: LineSegment StartX=-97 StartY=35 StartZ=0 EndX=-97 EndY=35.8 EndZ=0
    g3: LineSegment StartX=-97 StartY=35.8 StartZ=0 EndX=-108 EndY=35.8 EndZ=0
    g4: LineSegment StartX=-108 StartY=28.6 StartZ=0 EndX=-108 EndY=27.8 EndZ=0
    g5: LineSegment StartX=-108 StartY=27.8 StartZ=0 EndX=-97 EndY=27.8 EndZ=0
    g6: LineSegment StartX=-97 StartY=27.8 StartZ=0 EndX=-97 EndY=28.6 EndZ=0
    g7: LineSegment StartX=-97 StartY=28.6 StartZ=0 EndX=-108 EndY=28.6 EndZ=0
    g8: LineSegment StartX=-108 StartY=30.4 StartZ=0 EndX=-108 EndY=29.6 EndZ=0
    g9: LineSegment StartX=-108 StartY=29.6 StartZ=0 EndX=-97 EndY=29.6 EndZ=0
    g10: LineSegment StartX=-97 StartY=29.6 StartZ=0 EndX=-97 EndY=30.4 EndZ=0
    g11: LineSegment StartX=-97 StartY=30.4 StartZ=0 EndX=-108 EndY=30.4 EndZ=0
    g12: LineSegment StartX=-108 StartY=32.2 StartZ=0 EndX=-108 EndY=31.4 EndZ=0
    g13: LineSegment StartX=-108 StartY=31.4 StartZ=0 EndX=-97 EndY=31.4 EndZ=0
    g14: LineSegment StartX=-97 StartY=31.4 StartZ=0 EndX=-97 EndY=32.2 EndZ=0
    g15: LineSegment StartX=-97 StartY=32.2 StartZ=0 EndX=-108 EndY=32.2 EndZ=0
    g16: LineSegment StartX=-108 StartY=34 StartZ=0 EndX=-108 EndY=33.2 EndZ=0
    g17: LineSegment StartX=-108 StartY=33.2 StartZ=0 EndX=-97 EndY=33.2 EndZ=0
    g18: LineSegment StartX=-97 StartY=33.2 StartZ=0 EndX=-97 EndY=34 EndZ=0
    g19: LineSegment StartX=-97 StartY=34 StartZ=0 EndX=-108 EndY=34 EndZ=0
  constraints (55):
    c: Coincident(g1,g0)
    c: Horizontal(g1)
    c: Coincident(g2,g1)
    c: Vertical(g2)
    c: Coincident(g3,g2)
    c: Horizontal(g3)
    c: Coincident(g3,g0)
    c: DistanceX(g1,g1) = 11
    c: DistanceY(g2,g2) = 0.8
    c: Coincident(g5,g4)
    c: Horizontal(g5)
    c: Coincident(g6,g5)
    c: Vertical(g6)
    c: Coincident(g7,g6)
    c: Horizontal(g7)
    c: Coincident(g7,g4)
    c: Coincident(g9,g8)
    c: Horizontal(g9)
    c: Coincident(g10,g9)
    c: Vertical(g10)
    c: Coincident(g11,g10)
    c: Horizontal(g11)
    c: Coincident(g11,g8)
    c: Coincident(g13,g12)
    c: Horizontal(g13)
    c: Coincident(g14,g13)
    c: Vertical(g14)
    c: Coincident(g15,g14)
    c: Horizontal(g15)
    c: Coincident(g15,g12)
    c: Coincident(g17,g16)
    c: Horizontal(g17)
    c: Coincident(g18,g17)
    c: Vertical(g18)
    c: Coincident(g19,g18)
    c: Horizontal(g19)
    c: Coincident(g19,g16)
    c: Equal(g3,g19)
    c: Equal(g3,g15)
    c: Equal(g3,g11)
    c: Equal(g3,g7)
    c: Equal(g2,g18)
    c: Equal(g2,g14)
    c: Equal(g2,g10)
    c: Equal(g2,g6)
    c: DistanceY(g-4,g4) = 1
    c: DistanceY(g4,g8) = 1
    c: DistanceY(g8,g12) = 1
    c: DistanceY(g12,g16) = 1
    c: DistanceY(g16,g0) = 1
    c: Tangent(g0,g-5)
    c: Tangent(g16,g-5)
    c: Tangent(g12,g-5)
    c: Tangent(g8,g-5)
    c: Tangent(g4,g-5)
FEATURE [PartDesign::Chamfer] Chamfer009
  Angle = 45
  Base = -> Pad017 [Edge151,Edge154]
  BaseFeature = -> Pad017
  ChamferType = 1
  FlipDirection = false
  Refine = true
  Size = 1.5
  Size2 = 2.8
  SupportTransform = false
  Suppressed = false
  UseAllEdges = false
FEATURE [PartDesign::Pocket] Pocket009
  BaseFeature = -> Chamfer009
  Direction = (0,1,-2e-16)
  Length = 1
  Length2 = 5
  Profile = -> Sketch125
  ReferenceAxis = -> Sketch125 [N_Axis]
  Refine = true
  Suppressed = false
  Type = 0
FEATURE [PartDesign::Pad] Pad014
  BaseFeature = -> Pocket009
  Direction = (0,-1,2e-16)
  Length = 0.8
  Length2 = 10
  Profile = -> Sketch120
  ReferenceAxis = -> Sketch120 [N_Axis]
  Refine = true
  Suppressed = false
  Type = 0
FEATURE [Sketcher::SketchObject] Sketch124
  ArcFitTolerance = 1e-06
  AttachmentSupport = -> [Pad014]
  ExternalGeometry = -> [Binder001]
  FullyConstrained = true
  MakeInternals = false
  MapMode = 5
  Placement = pos=(0,-2.8,6e-16) rot=(1,0,0;1.5708rad)
  sketch-geometry (4):
    g0: LineSegment StartX=-129 StartY=39.2 StartZ=0 EndX=-131.599 EndY=31.2 EndZ=0
    g1: LineSegment StartX=-118 StartY=39.2 StartZ=0 EndX=-120.599 EndY=31.2 EndZ=0
    g2: LineSegment StartX=-129 StartY=39.2 StartZ=0 EndX=-118 EndY=39.2 EndZ=0
    g3: LineSegment StartX=-120.599 StartY=31.2 StartZ=0 EndX=-131.599 EndY=31.2 EndZ=0
  constraints (12):
    c: PointOnObject(g0,g-3)
    c: PointOnObject(g1,g-3)
    c: Parallel(g-4,g0)
    c: Parallel(g-4,g1)
    c: Coincident(g2,g0)
    c: Coincident(g2,g1)
    c: DistanceX(g2,g2) = 11
    c: DistanceY(g1,g1) = 8
    c: Coincident(g3,g1)
    c: Horizontal(g3)
    c: Coincident(g3,g0)
    c: DistanceX(g1,g-3) = 118
FEATURE [PartDesign::Pad] Pad018
  BaseFeature = -> Pad014
  Direction = (0,-1,2e-16)
  Length = 1.2
  Length2 = 10
  Profile = -> Sketch124
  ReferenceAxis = -> Sketch124 [N_Axis]
  Refine = true
  Suppressed = false
  Type = 0
FEATURE [Sketcher::SketchObject] Sketch126
  ArcFitTolerance = 1e-06
  AttachmentSupport = -> [Pad018]
  ExternalGeometry = -> [Pad018]
  FullyConstrained = true
  MakeInternals = false
  MapMode = 5
  Placement = pos=(0,-4,0) rot=(1,0,0;1.5708rad)
  sketch-geometry (8):
    g0: LineSegment StartX=-129.877 StartY=36.5 StartZ=0 EndX=-130.137 EndY=35.7 EndZ=0
    g1: LineSegment StartX=-130.69 StartY=34 StartZ=0 EndX=-130.95 EndY=33.2 EndZ=0
    g2: LineSegment StartX=-129.877 StartY=36.5 StartZ=0 EndX=-118.877 EndY=36.5 EndZ=0
    g3: LineSegment StartX=-130.137 StartY=35.7 StartZ=0 EndX=-119.137 EndY=35.7 EndZ=0
    g4: LineSegment StartX=-130.69 StartY=34 StartZ=0 EndX=-119.69 EndY=34 EndZ=0
    g5: LineSegment StartX=-130.95 StartY=33.2 StartZ=0 EndX=-119.95 EndY=33.2 EndZ=0
    g6: LineSegment StartX=-118.877 StartY=36.5 StartZ=0 EndX=-119.137 EndY=35.7 EndZ=0
    g7: LineSegment StartX=-119.69 StartY=34 StartZ=0 EndX=-119.95 EndY=33.2 EndZ=0
  constraints (20):
    c: Coincident(g2,g0)
    c: Horizontal(g2)
    c: Coincident(g3,g0)
    c: Horizontal(g3)
    c: Coincident(g4,g1)
    c: Horizontal(g4)
    c: Coincident(g5,g1)
    c: Horizontal(g5)
    c: Coincident(g6,g2)
    c: Coincident(g6,g3)
    c: Coincident(g7,g4)
    c: Coincident(g7,g5)
    c: Tangent(g0,g-4)
    c: Tangent(g6,g-5)
    c: Tangent(g1,g-4)
    c: Tangent(g7,g-5)
    c: DistanceY(g3,g2) = 0.8
    c: DistanceY(g5,g4) = 0.8
    c: DistanceY(g-6,g1) = 2
    c: DistanceY(g-6,g0) = 4.5
FEATURE [PartDesign::Chamfer] Chamfer008
  Angle = 45
  Base = -> Pad018 [Edge257]
  BaseFeature = -> Pad018
  ChamferType = 1
  FlipDirection = false
  Refine = true
  Size = 1
  Size2 = 6
  SupportTransform = false
  Suppressed = false
  UseAllEdges = false
FEATURE [PartDesign::Pocket] Pocket010
  BaseFeature = -> Chamfer008
  Direction = (0,1,-2e-16)
  Length = 1
  Length2 = 5
  Profile = -> Sketch126
  ReferenceAxis = -> Sketch126 [N_Axis]
  Refine = true
  Suppressed = false
  Type = 0
FEATURE [PartDesign::Pad] Pad015
  BaseFeature = -> Pocket010
  Direction = (0,-1,2e-16)
  Length = 2
  Length2 = 10
  Profile = -> Sketch121
  ReferenceAxis = -> Sketch121 [N_Axis]
  Refine = true
  Suppressed = false
  Type = 0
FEATURE [PartDesign::Pad] Pad016
  BaseFeature = -> Pad015
  Direction = (0,-1,2e-16)
  Length = 1.6
  Length2 = 10
  Profile = -> Sketch122
  ReferenceAxis = -> Sketch122 [N_Axis]
  Refine = true
  Suppressed = false
  Type = 0
FEATURE [Sketcher::SketchObject] Sketch127
  ArcFitTolerance = 1e-06
  AttachmentSupport = -> [Pad016]
  ExternalGeometry = -> [Pad016]
  FullyConstrained = true
  MakeInternals = false
  MapMode = 5
  Placement = pos=(0,0,-80.4316) rot=(1,0,0;3.14159rad)
  sketch-geometry (8):
    g0: LineSegment StartX=-176.685 StartY=3.6 StartZ=0 EndX=-186.685 EndY=3.6 EndZ=0
    g1: LineSegment [constr] StartX=-186.685 StartY=3.6 StartZ=0 EndX=-186.685 EndY=-9e-16 EndZ=0
    g2: LineSegment StartX=-176.685 StartY=3.6 StartZ=0 EndX=-176.685 EndY=0 EndZ=0
    g3: ArcOfEllipse CenterX=-186.685 CenterY=-9e-16 CenterZ=0 NormalX=0 NormalY=0 NormalZ=1 MajorRadius=10 MinorRadius=3.6 AngleXU=1e-16 StartAngle=0 EndAngle=1.5708
    g4: LineSegment [constr] StartX=-176.685 StartY=-2e-15 StartZ=0 EndX=-196.685 EndY=-2e-15 EndZ=0
    g5: LineSegment [constr] StartX=-186.685 StartY=3.6 StartZ=0 EndX=-186.685 EndY=-3.6 EndZ=0
    g6: GeomPoint [constr] X=-177.356 Y=0 Z=0
    g7: GeomPoint [constr] X=-196.015 Y=-1.9e-15 Z=0
  constraints (13):
    c: Coincident(g0,g-4)
    c: PointOnObject(g0,g-4)
    c: DistanceX(g0,g0) = 10
    c: Coincident(g1,g0)
    c: PointOnObject(g1,g-5)
    c: Vertical(g1)
    c: Coincident(g2,g0)
    c: Coincident(g2,g-5)
    c: InternalAlignment(g4-g7 -> g3) x4
    c: Coincident(g3,g1)
    c: Coincident(g3,g0)
    c: Coincident(g3,g2)
    c: Horizontal(g4)
FEATURE [Sketcher::SketchObject] Sketch128
  ArcFitTolerance = 1e-06
  AttachmentSupport = -> [Pad016]
  ExternalGeometry = -> [Pad016]
  FullyConstrained = true
  MakeInternals = false
  MapMode = 5
  Placement = pos=(0,0,-80.4316) rot=(1,0,0;3.14159rad)
  sketch-geometry (8):
    g0: LineSegment StartX=-215.932 StartY=3.6 StartZ=0 EndX=-215.932 EndY=-1.3e-15 EndZ=0
    g1: LineSegment StartX=-215.932 StartY=3.6 StartZ=0 EndX=-205.932 EndY=3.6 EndZ=0
    g2: LineSegment [constr] StartX=-205.932 StartY=3.6 StartZ=0 EndX=-205.932 EndY=-9e-16 EndZ=0
    g3: ArcOfEllipse CenterX=-205.932 CenterY=-9e-16 CenterZ=0 NormalX=0 NormalY=0 NormalZ=1 MajorRadius=10 MinorRadius=3.6 AngleXU=-3.14159 StartAngle=4.71239 EndAngle=6.28319
    g4: LineSegment [constr] StartX=-215.932 StartY=-1e-15 StartZ=0 EndX=-195.932 EndY=-1e-15 EndZ=0
    g5: LineSegment [constr] StartX=-205.932 StartY=-3.6 StartZ=0 EndX=-205.932 EndY=3.6 EndZ=0
    g6: GeomPoint [constr] X=-215.262 Y=-2e-15 Z=0
    g7: GeomPoint [constr] X=-196.602 Y=-1e-15 Z=0
  constraints (13):
    c: Coincident(g0,g-4)
    c: Coincident(g0,g-5)
    c: Coincident(g1,g0)
    c: PointOnObject(g1,g-3)
    c: DistanceX(g1,g1) = 10
    c: Coincident(g2,g1)
    c: Vertical(g2)
    c: PointOnObject(g2,g-5)
    c: InternalAlignment(g4-g7 -> g3) x4
    c: Coincident(g3,g2)
    c: Coincident(g3,g1)
    c: Coincident(g3,g0)
    c: Horizontal(g4)
FEATURE [PartDesign::SubtractivePipe] SubtractivePipe002
  AuxilleryCurvelinear = true
  AuxillerySpineTangent = false
  BaseFeature = -> Pad016
  Binormal = (0,0,0)
  Mode = 0
  Profile = -> Sketch127
  Refine = true
  Spine = -> Pad016 [Edge254]
  SpineTangent = false
  Suppressed = false
  Transformation = 0
  Transition = 0
FEATURE [PartDesign::SubtractivePipe] SubtractivePipe003
  AuxilleryCurvelinear = true
  AuxillerySpineTangent = false
  BaseFeature = -> SubtractivePipe002
  Binormal = (0,0,0)
  Mode = 0
  Profile = -> Sketch128
  Refine = true
  Spine = -> Pad016 [Edge256,Edge251,Edge252]
  SpineTangent = false
  Suppressed = false
  Transformation = 0
  Transition = 0
FEATURE [Sketcher::SketchObject] Sketch129
  ArcFitTolerance = 1e-06
  AttachmentSupport = -> [Pad016]
  ExternalGeometry = -> [Binder001]
  FullyConstrained = true
  MakeInternals = false
  MapMode = 5
  Placement = pos=(0,-3.6,0) rot=(1,0,0;1.5708rad)
  sketch-geometry (12):
    g0: LineSegment [constr] StartX=-192.176 StartY=-3.18451 StartZ=0 EndX=-181.223 EndY=20.303 EndZ=0
    g1: LineSegment [constr] StartX=-202.765 StartY=20.303 StartZ=0 EndX=-181.223 EndY=20.303 EndZ=0
    g2: LineSegment StartX=-202.765 StartY=20.303 StartZ=0 EndX=-181.223 EndY=20.303 EndZ=0
    g3: LineSegment StartX=-192.176 StartY=-3.18451 StartZ=0 EndX=-196.804 EndY=-13.1107 EndZ=0
    g4: ArcOfCircle CenterX=-207.583 CenterY=4 CenterZ=0 NormalX=0 NormalY=0 NormalZ=1 AngleXU=0 Radius=17 StartAngle=5.84685 EndAngle=7.56663
    g5: ArcOfEllipse CenterX=-181.223 CenterY=8.55923 CenterZ=0 NormalX=0 NormalY=0 NormalZ=1 MajorRadius=23.4779 MinorRadius=11.7437 AngleXU=2e-16 StartAngle=4.71239 EndAngle=7.85398
    g6: LineSegment [constr] StartX=-157.745 StartY=8.55923 StartZ=0 EndX=-204.701 EndY=8.55923 EndZ=0
    g7: LineSegment [constr] StartX=-181.223 StartY=20.303 StartZ=0 EndX=-181.223 EndY=-3.18451 EndZ=0
    g8: GeomPoint [constr] X=-160.894 Y=8.55923 Z=0
    g9: GeomPoint [constr] X=-201.553 Y=8.55923 Z=0
    g10: ArcOfCircle CenterX=-181.223 CenterY=-20.3763 CenterZ=0 NormalX=0 NormalY=0 NormalZ=1 AngleXU=0 Radius=17.1918 StartAngle=1.57079 EndAngle=2.70526
    g11: GeomPoint [constr] X=-181.223 Y=-3.18451 Z=0
  constraints (23):
    c: Coincident(g0,g-5)
    c: Coincident(g1,g-6)
    c: Horizontal(g1)
    c: Coincident(g1,g0)
    c: Parallel(g0,g-4)
    c: Coincident(g2,g1)
    c: Coincident(g2,g0)
    c: Coincident(g3,g0)
    c: Equal(g4,g-5)
    c: Coincident(g4,g1)
    c: Coincident(g4,g0)
    c: InternalAlignment(g6-g9 -> g5) x4
    c: Vertical(g5,g0)
    c: Horizontal(g6)
    c: Coincident(g5,g0)
    c: DistanceX(g6,g-3) = 10.1
    c: Tangent(g10,g3) = -1.5708
    c: PointOnObject(g11,g10)
    c: Tangent(g5,g10,g11) = 1.5708
    c: Coincident(g10,g5)
    c: Coincident(g11,g7)
    c: Parallel(g3,g-4)
    c: Horizontal(g5,g0)
FEATURE [Sketcher::SketchObject] Sketch130
  ArcFitTolerance = 1e-06
  AttachmentOffset = pos=(0,0,-1.6) rot=(0,0,1;0rad)
  AttachmentSupport = -> [Pad016]
  ExternalGeometry = -> [Binder001]
  FullyConstrained = true
  MakeInternals = false
  MapMode = 5
  Placement = pos=(0,-2,-4e-16) rot=(1,0,0;1.5708rad)
  sketch-geometry (12):
    g0: LineSegment [constr] StartX=-192.176 StartY=-3.18451 StartZ=0 EndX=-181.223 EndY=20.303 EndZ=0
    g1: LineSegment [constr] StartX=-202.765 StartY=20.303 StartZ=0 EndX=-181.223 EndY=20.303 EndZ=0
    g2: LineSegment StartX=-202.765 StartY=20.303 StartZ=0 EndX=-181.223 EndY=20.303 EndZ=0
    g3: LineSegment StartX=-192.176 StartY=-3.18451 StartZ=0 EndX=-193.827 EndY=-6.72678 EndZ=0
    g4: ArcOfCircle CenterX=-207.583 CenterY=4 CenterZ=0 NormalX=0 NormalY=0 NormalZ=1 AngleXU=0 Radius=17 StartAngle=5.84685 EndAngle=7.56663
    g5: ArcOfEllipse CenterX=-181.223 CenterY=10.803 CenterZ=0 NormalX=0 NormalY=0 NormalZ=1 MajorRadius=14.4779 MinorRadius=9.5 AngleXU=0 StartAngle=4.71239 EndAngle=7.85398
    g6: LineSegment [constr] StartX=-166.745 StartY=10.803 StartZ=0 EndX=-195.701 EndY=10.803 EndZ=0
    g7: LineSegment [constr] StartX=-181.223 StartY=20.303 StartZ=0 EndX=-181.223 EndY=1.30297 EndZ=0
    g8: GeomPoint [constr] X=-170.298 Y=10.803 Z=0
    g9: GeomPoint [constr] X=-192.148 Y=10.803 Z=0
    g10: ArcOfCircle CenterX=-181.223 CenterY=-12.6042 CenterZ=0 NormalX=0 NormalY=0 NormalZ=1 AngleXU=0 Radius=13.9072 StartAngle=1.5708 EndAngle=2.70526
    g11: GeomPoint [constr] X=-181.223 Y=1.30297 Z=0
  constraints (23):
    c: Coincident(g0,g-5)
    c: Coincident(g1,g-6)
    c: Horizontal(g1)
    c: Coincident(g1,g0)
    c: Parallel(g0,g-4)
    c: Coincident(g2,g1)
    c: Coincident(g2,g0)
    c: Coincident(g3,g0)
    c: Equal(g4,g-5)
    c: Coincident(g4,g1)
    c: Coincident(g4,g0)
    c: InternalAlignment(g6-g9 -> g5) x4
    c: Vertical(g5,g0)
    c: Horizontal(g6)
    c: Coincident(g5,g0)
    c: DistanceX(g6,g-3) = 19.1
    c: Tangent(g10,g3) = -1.5708
    c: PointOnObject(g11,g10)
    c: Tangent(g5,g10,g11) = 1.5708
    c: Coincident(g10,g5)
    c: Coincident(g11,g7)
    c: Parallel(g3,g-4)
    c: DistanceY(g5,g0) = 19
FEATURE [Part::Part2DObjectPython] Clone2D001  label="Sketch130 (2D)"  # Draft 2D object (typed FeaturePython)
  Fuse = false
  Objects = -> [Sketch130]
  Placement = pos=(0,-2,-4e-16) rot=(1,0,0;1.5708rad)
  Scale = (1,1,1)
FEATURE [Sketcher::SketchObject] Sketch131
  ArcFitTolerance = 1e-06
  AttachmentOffset = pos=(0,0,-3.5) rot=(0,0,1;0rad)
  AttachmentSupport = -> [Pad016]
  ExternalGeometry = -> [Binder001]
  FullyConstrained = true
  MakeInternals = false
  MapMode = 5
  Placement = pos=(0,-0.1,-8e-16) rot=(1,0,0;1.5708rad)
  sketch-geometry (1):
    g0: GeomPoint X=-197.47 Y=8.55923 Z=0
  constraints (1):
    c: Symmetric(g-6,g-4,g0)
FEATURE [PartDesign::SubtractiveLoft] SubtractiveLoft002
  BaseFeature = -> SubtractivePipe003
  Closed = false
  Profile = -> Sketch129
  Refine = true
  Ruled = false
  Sections = -> [Sketch130]
  Suppressed = false
FEATURE [PartDesign::SubtractiveLoft] SubtractiveLoft003
  BaseFeature = -> SubtractiveLoft002
  Closed = false
  Profile = -> Clone2D001
  Refine = true
  Ruled = false
  Sections = -> [Sketch131]
  Suppressed = false
FEATURE [PartDesign::Chamfer] Chamfer010
  Angle = 45
  Base = -> SubtractiveLoft003 [Edge200,Edge201,Edge203,Edge202,Edge194]
  BaseFeature = -> SubtractiveLoft003
  ChamferType = 0
  FlipDirection = false
  Refine = true
  Size = 1.5
  Size2 = 1
  SupportTransform = false
  Suppressed = false
  UseAllEdges = false
FEATURE [PartDesign::Chamfer] Chamfer011
  Angle = 45
  Base = -> Chamfer010 [Edge15]
  BaseFeature = -> Chamfer010
  ChamferType = 0
  FlipDirection = false
  Refine = true
  Size = 1.6
  Size2 = 1
  SupportTransform = false
  Suppressed = false
  UseAllEdges = false
FEATURE [PartDesign::Chamfer] Chamfer012
  Angle = 45
  Base = -> Chamfer011 [Edge10]
  BaseFeature = -> Chamfer011
  ChamferType = 0
  FlipDirection = false
  Refine = true
  Size = 3.5
  Size2 = 1
  SupportTransform = false
  Suppressed = false
  UseAllEdges = false
FEATURE [PartDesign::Chamfer] Chamfer013
  Angle = 45
  Base = -> Chamfer012 [Edge145,Edge94]
  BaseFeature = -> Chamfer012
  ChamferType = 0
  FlipDirection = false
  Refine = true
  Size = 1.9
  Size2 = 1
  SupportTransform = false
  Suppressed = false
  UseAllEdges = false
FEATURE [Sketcher::SketchObject] Sketch132
  ArcFitTolerance = 1e-06
  AttachmentSupport = -> [Pad016]
  ExternalGeometry = -> [Binder001]
  FullyConstrained = true
  MakeInternals = false
  MapMode = 5
  Placement = pos=(0,-3.6,0) rot=(1,0,0;1.5708rad)
  sketch-geometry (3):
    g0: LineSegment [constr] StartX=-215.42 StartY=-53.0314 StartZ=0 EndX=-167.782 EndY=-53.0314 EndZ=0
    g1: Circle CenterX=-191.282 CenterY=-53.0314 CenterZ=0 NormalX=0 NormalY=0 NormalZ=1 AngleXU=0 Radius=11.5
    g2: Circle CenterX=-191.282 CenterY=-53.0314 CenterZ=0 NormalX=0 NormalY=0 NormalZ=1 AngleXU=0 Radius=10.7
  constraints (8):
    c: Coincident(g0,g-3)
    c: PointOnObject(g0,g-4)
    c: Horizontal(g0)
    c: Diameter(g1) = 23
    c: PointOnObject(g1,g0)
    c: DistanceX(g1,g0) = 23.5
    c: Diameter(g2) = 21.4
    c: Coincident(g2,g1)
FEATURE [PartDesign::Fillet] Fillet007
  Base = -> Chamfer013 [Edge83]
  BaseFeature = -> Chamfer013
  Radius = 1.1
  Refine = true
  SupportTransform = false
  Suppressed = false
  UseAllEdges = false
FEATURE [PartDesign::Fillet] Fillet008
  Base = -> Fillet007 [Edge76]
  BaseFeature = -> Fillet007
  Radius = 1.9
  Refine = true
  SupportTransform = false
  Suppressed = false
  UseAllEdges = false
FEATURE [PartDesign::Pocket] Pocket011
  BaseFeature = -> Fillet008
  Direction = (0,1,-2e-16)
  Length = 0.8
  Length2 = 5
  Profile = -> Sketch132
  ReferenceAxis = -> Sketch132 [N_Axis]
  Refine = true
  Suppressed = false
  Type = 0
FEATURE [Part::Part2DObjectPython] ShapeString  # Draft 2D object (typed FeaturePython)
  FontFile = <path>
  Fuse = false
  Justification = 6
  JustificationReference = 0
  KeepLeftMargin = false
  MakeFace = true
  ObliqueAngle = 0
  Placement = pos=(-199,-3.6,-57.5) rot=(1,0,0;1.5708rad)
  ScaleToSize = true
  Size = 10
  String = AS
  Tracking = 0
FEATURE [PartDesign::Pocket] Pocket012
  BaseFeature = -> Pocket011
  Direction = (0,1,0)
  Length = 1
  Length2 = 5
  Profile = -> ShapeString
  ReferenceAxis = -> ShapeString [N_Axis]
  Refine = true
  Suppressed = false
  Type = 0
FEATURE [PartDesign::Body] Body007  label="lato DX"
  AllowCompound = false
  Group = -> [Binder001,Sketch114,Pad011,Chamfer014,Sketch115,Pocket006,Sketch116,Pad012,Sketch117,Pocket007,Sketch118,Pad013,Sketch119,Pocket008,Pad017,Chamfer009,Pocket009,Sketch123,Sketch120,Pad014,Pad018,Chamfer008,Pocket010,Sketch121,Pad015,Sketch122,Pad016,Sketch124,Sketch125,Sketch126,Sketch127,Sketch128,SubtractivePipe002,SubtractivePipe003,Sketch129,Sketch130,Clone2D001,Sketch131,SubtractiveLoft002,+11 more]
  Origin = -> Origin007
  Tip = -> Pocket012
FEATURE [Sketcher::SketchObject] Sketch133
  ArcFitTolerance = 1e-06
  AttachmentSupport = -> [Binder]
  ExternalGeometry = -> [Binder]
  FullyConstrained = true
  MakeInternals = false
  MapMode = 5
  Placement = pos=(0,9e-16,0) rot=(0,0.707107,0.707107;3.14159rad)
  sketch-geometry (30):
    g0: LineSegment StartX=0 StartY=39.2 StartZ=0 EndX=0 EndY=3.2 EndZ=0
    g1: LineSegment StartX=0 StartY=3.2 StartZ=0 EndX=82.8 EndY=3.2 EndZ=0
    g2: LineSegment StartX=82.8 StartY=3.2 StartZ=0 EndX=82.8 EndY=6.2 EndZ=0
    g3: LineSegment StartX=82.8 StartY=6.2 StartZ=0 EndX=91.752 EndY=6.2 EndZ=0
    g4: LineSegment StartX=0 StartY=39.2 StartZ=0 EndX=195.887 EndY=39.2 EndZ=0
    g5: LineSegment StartX=195.887 StartY=39.2 StartZ=0 EndX=202.765 EndY=20.303 EndZ=0
    g6: LineSegment StartX=192.333 StartY=24.9893 StartZ=0 EndX=196.467 EndY=26.4942 EndZ=0
    g7: LineSegment StartX=196.467 StartY=26.4942 StartZ=0 EndX=194.073 EndY=33.0721 EndZ=0
    g8: LineSegment StartX=194.073 StartY=33.0721 StartZ=0 EndX=189.939 EndY=31.5672 EndZ=0
    g9: LineSegment StartX=189.939 StartY=31.5672 StartZ=0 EndX=192.333 EndY=24.9893 EndZ=0
    g10: ArcOfCircle CenterX=107.6 CenterY=4 CenterZ=0 NormalX=0 NormalY=0 NormalZ=1 AngleXU=0 Radius=16 StartAngle=1.5708 EndAngle=3.00366
    g11: LineSegment StartX=107.6 StartY=20 StartZ=0 EndX=132.428 EndY=20 EndZ=0
    g12: ArcOfCircle [constr] CenterX=132.428 CenterY=4 CenterZ=0 NormalX=0 NormalY=0 NormalZ=1 AngleXU=0 Radius=16 StartAngle=0.314159 EndAngle=1.5708
    g13: LineSegment StartX=147.645 StartY=8.94427 StartZ=0 EndX=176.685 EndY=-80.4316 EndZ=0
    g14: LineSegment StartX=176.685 StartY=-80.4316 StartZ=0 EndX=215.932 EndY=-80.4316 EndZ=0
    g15: ArcOfCircle CenterX=207.583 CenterY=4 CenterZ=0 NormalX=0 NormalY=0 NormalZ=1 AngleXU=0 Radius=17 StartAngle=1.85815 EndAngle=3.57792
    g16: ArcOfCircle CenterX=184.801 CenterY=-67.3089 CenterZ=0 NormalX=0 NormalY=0 NormalZ=1 AngleXU=0 Radius=33.7833 StartAngle=5.88425 EndAngle=6.71952
    g17: LineSegment StartX=192.176 StartY=-3.18451 StartZ=0 EndX=215.42 EndY=-53.0314 EndZ=0
    g18: Circle CenterX=5.6 CenterY=34.8 CenterZ=0 NormalX=0 NormalY=0 NormalZ=1 AngleXU=0 Radius=1.8
    g19: Circle CenterX=5.6 CenterY=7.6 CenterZ=0 NormalX=0 NormalY=0 NormalZ=1 AngleXU=0 Radius=1.8
    g20: Circle CenterX=78.51 CenterY=34.8 CenterZ=0 NormalX=0 NormalY=0 NormalZ=1 AngleXU=0 Radius=1.8
    g21: Circle CenterX=78.51 CenterY=7.6 CenterZ=0 NormalX=0 NormalY=0 NormalZ=1 AngleXU=0 Radius=1.8
    g22: Circle CenterX=184.08 CenterY=34.8 CenterZ=0 NormalX=0 NormalY=0 NormalZ=1 AngleXU=0 Radius=1.8
    g23: Circle CenterX=179.305 CenterY=-76.8316 CenterZ=0 NormalX=0 NormalY=0 NormalZ=1 AngleXU=0 Radius=1.8
    g24: Circle CenterX=213.443 CenterY=-76.8316 CenterZ=0 NormalX=0 NormalY=0 NormalZ=1 AngleXU=0 Radius=1.8
    g25: Circle CenterX=19 CenterY=21.2 CenterZ=0 NormalX=0 NormalY=0 NormalZ=1 AngleXU=0 Radius=6.3
    g26: Circle CenterX=42 CenterY=21.2 CenterZ=0 NormalX=0 NormalY=0 NormalZ=1 AngleXU=0 Radius=6.3
    g27: Circle CenterX=65 CenterY=21.2 CenterZ=0 NormalX=0 NormalY=0 NormalZ=1 AngleXU=0 Radius=6.3
    g28: LineSegment StartX=132.428 StartY=20 StartZ=0 EndX=144.053 EndY=20 EndZ=0
    g29: LineSegment StartX=147.645 StartY=8.94427 StartZ=0 EndX=144.053 EndY=20 EndZ=0
  constraints (65):
    c: Coincident(g0,g-4)
    c: Coincident(g0,g-5)
    c: Coincident(g1,g0)
    c: Coincident(g1,g-6)
    c: Coincident(g2,g1)
    c: Coincident(g2,g-7)
    c: Coincident(g3,g2)
    c: Coincident(g3,g-8)
    c: Coincident(g4,g0)
    c: Coincident(g4,g-16)
    c: Coincident(g5,g4)
    c: Coincident(g5,g-16)
    c: Coincident(g6,g-20)
    c: Coincident(g6,g-21)
    c: Coincident(g7,g6)
    c: Coincident(g7,g-23)
    c: Coincident(g8,g7)
    c: Coincident(g8,g-22)
    c: Coincident(g9,g8)
    c: Coincident(g9,g6)
    c: Equal(g10,g-8)
    c: Coincident(g10,g3)
    c: Coincident(g10,g-9)
    c: Coincident(g11,g10)
    c: Coincident(g11,g-10)
    c: Equal(g12,g-10)
    c: Coincident(g12,g11)
    c: Coincident(g12,g-11)
    c: Coincident(g13,g12)
    c: Coincident(g13,g-12)
    c: Coincident(g14,g13)
    c: Coincident(g14,g-13)
    c: Equal(g15,g-15)
    c: Coincident(g15,g5)
    c: Coincident(g15,g-15)
    c: Equal(g16,g-13)
    c: Coincident(g16,g14)
    c: Coincident(g16,g-14)
    c: Coincident(g17,g15)
    c: Coincident(g17,g16)
    c: Equal(g18,g-28)
    c: Equal(g19,g-29)
    c: Equal(g20,g-26)
    c: Equal(g21,g-27)
    c: Equal(g22,g-17)
    c: Equal(g24,g-25)
    c: Equal(g23,g-24)
    c: Coincident(g23,g-24)
    c: Coincident(g24,g-25)
    c: Coincident(g22,g-17)
    c: Coincident(g20,g-26)
    c: Coincident(g21,g-27)
    c: Coincident(g18,g-28)
    c: Coincident(g19,g-29)
    c: Equal(g25,g-30)
    c: Equal(g26,g-31)
    c: Equal(g27,g-32)
    c: Coincident(g25,g-30)
    c: Coincident(g26,g-31)
    c: Coincident(g27,g-32)
    c: Parallel(g28,g11)
    c: Parallel(g29,g13)
    c: Coincident(g28,g11)
    c: Coincident(g29,g12)
    c: Coincident(g29,g28)
FEATURE [PartDesign::Pad] Pad019
  Direction = (0,1,-2e-16)
  Length = 2
  Length2 = 10
  Profile = -> Sketch133
  ReferenceAxis = -> Sketch133 [N_Axis]
  Refine = true
  Suppressed = false
  Type = 0
FEATURE [Sketcher::SketchObject] Sketch091  label="Sketch091 - forma anteriore"
  ArcFitTolerance = 1e-06
  AttachmentSupport = -> [Pad019]
  ExternalGeometry = -> [Binder]
  FullyConstrained = true
  MakeInternals = false
  MapMode = 5
  Placement = pos=(0,2,0) rot=(0,0.707107,0.707107;3.14159rad)
  sketch-geometry (12):
    g0: Circle CenterX=5.6 CenterY=34.8 CenterZ=0 NormalX=0 NormalY=0 NormalZ=1 AngleXU=0 Radius=1.8
    g1: Circle CenterX=5.6 CenterY=7.6 CenterZ=0 NormalX=0 NormalY=0 NormalZ=1 AngleXU=0 Radius=1.8
    g2: Circle CenterX=78.51 CenterY=34.8 CenterZ=0 NormalX=0 NormalY=0 NormalZ=1 AngleXU=0 Radius=1.8
    g3: Circle CenterX=78.51 CenterY=7.6 CenterZ=0 NormalX=0 NormalY=0 NormalZ=1 AngleXU=0 Radius=1.8
    g4: LineSegment StartX=0 StartY=39.2 StartZ=0 EndX=0 EndY=3.2 EndZ=0
    g5: LineSegment StartX=0 StartY=3.2 StartZ=0 EndX=82.8 EndY=3.2 EndZ=0
    g6: LineSegment StartX=82.8 StartY=3.2 StartZ=0 EndX=82.8 EndY=39.2 EndZ=0
    g7: LineSegment StartX=82.8 StartY=39.2 StartZ=0 EndX=0 EndY=39.2 EndZ=0
    g8: ArcOfCircle CenterX=19 CenterY=21.2 CenterZ=0 NormalX=0 NormalY=0 NormalZ=1 AngleXU=0 Radius=10 StartAngle=1.5708 EndAngle=4.71239
    g9: ArcOfCircle CenterX=65 CenterY=21.2 CenterZ=0 NormalX=0 NormalY=0 NormalZ=1 AngleXU=0 Radius=10 StartAngle=4.71239 EndAngle=7.85398
    g10: LineSegment StartX=19 StartY=31.2 StartZ=0 EndX=65 EndY=31.2 EndZ=0
    g11: LineSegment StartX=19 StartY=11.2 StartZ=0 EndX=65 EndY=11.2 EndZ=0
  constraints (25):
    c: Equal(g2,g-7)
    c: Equal(g3,g-8)
    c: Equal(g1,g-13)
    c: Equal(g0,g-12)
    c: Coincident(g0,g-12)
    c: Coincident(g1,g-13)
    c: Coincident(g3,g-8)
    c: Coincident(g2,g-7)
    c: Coincident(g4,g-4)
    c: Coincident(g4,g-5)
    c: Coincident(g5,g4)
    c: Coincident(g5,g-6)
    c: Coincident(g6,g5)
    c: PointOnObject(g6,g-3)
    c: Vertical(g6)
    c: Coincident(g7,g6)
    c: Coincident(g7,g4)
    c: Tangent(g8,g10) = 1.5708
    c: Tangent(g8,g11) = -1.5708
    c: Tangent(g9,g10) = 1.5708
    c: Tangent(g9,g11) = -1.5708
    c: Equal(g8,g9)
    c: Radius(g8) = 10
    c: Coincident(g8,g-11)
    c: Coincident(g9,g-9)
FEATURE [Sketcher::SketchObject] Sketch093  label="Sketch093 - scavi interni pulsanti"
  ArcFitTolerance = 1e-06
  AttachmentSupport = -> [Pad019]
  ExternalGeometry = -> [Binder]
  FullyConstrained = true
  MakeInternals = false
  MapMode = 5
  Placement = pos=(0,1.8e-15,0) rot=(1,0,0;1.5708rad)
  sketch-geometry (3):
    g0: Circle CenterX=-65 CenterY=21.2 CenterZ=0 NormalX=0 NormalY=0 NormalZ=1 AngleXU=0 Radius=7.3
    g1: Circle CenterX=-42 CenterY=21.2 CenterZ=0 NormalX=0 NormalY=0 NormalZ=1 AngleXU=0 Radius=7.3
    g2: Circle CenterX=-19 CenterY=21.2 CenterZ=0 NormalX=0 NormalY=0 NormalZ=1 AngleXU=0 Radius=7.3
  constraints (6):
    c: Coincident(g0,g-3)
    c: Coincident(g1,g-4)
    c: Coincident(g2,g-5)
    c: Diameter(g0) = 14.6
    c: Diameter(g1) = 14.6
    c: Diameter(g2) = 14.6
FEATURE [Sketcher::SketchObject] Sketch094  label="Sketch094 - forma centrale"
  ArcFitTolerance = 1e-06
  AttachmentSupport = -> [Pad019]
  ExternalGeometry = -> [Binder]
  FullyConstrained = true
  MakeInternals = false
  MapMode = 5
  Placement = pos=(0,2,0) rot=(0,0.707107,0.707107;3.14159rad)
  sketch-geometry (4):
    g0: LineSegment StartX=137.815 StartY=39.2 StartZ=0 EndX=142.655 EndY=24.303 EndZ=0
    g1: LineSegment StartX=110.815 StartY=24.303 StartZ=0 EndX=142.655 EndY=24.303 EndZ=0
    g2: LineSegment StartX=137.815 StartY=39.2 StartZ=0 EndX=110.815 EndY=39.2 EndZ=0
    g3: ArcOfCircle CenterX=92.2534 CenterY=31.7515 CenterZ=0 NormalX=0 NormalY=0 NormalZ=1 AngleXU=0 Radius=20 StartAngle=5.90156 EndAngle=6.66481
  constraints (12):
    c: PointOnObject(g0,g-3)
    c: Tangent(g0,g-5)
    c: Horizontal(g1)
    c: Coincident(g1,g0)
    c: Coincident(g2,g0)
    c: PointOnObject(g2,g-3)
    c: DistanceX(g2,g2) = 27
    c: Vertical(g1,g2)
    c: Coincident(g3,g2)
    c: Radius(g3) = 20
    c: Coincident(g3,g1)
    c: DistanceY(g-6,g0) = 4
FEATURE [Sketcher::SketchObject] Sketch095  label="Sketch095 - forma posteriore"
  ArcFitTolerance = 1e-06
  AttachmentSupport = -> [Pad019]
  ExternalGeometry = -> [Binder]
  FullyConstrained = true
  MakeInternals = false
  MapMode = 5
  Placement = pos=(0,2,0) rot=(0,0.707107,0.707107;3.14159rad)
  sketch-geometry (15):
    g0: LineSegment StartX=137.815 StartY=39.2 StartZ=0 EndX=143.955 EndY=20.303 EndZ=0
    g1: LineSegment StartX=143.955 StartY=20.303 StartZ=0 EndX=190.141 EndY=20.303 EndZ=0
    g2: ArcOfCircle CenterX=184.08 CenterY=34.8 CenterZ=0 NormalX=0 NormalY=0 NormalZ=1 AngleXU=0 Radius=3.5 StartAngle=3.49066 EndAngle=4.71239
    g3: LineSegment StartX=180.791 StartY=33.6029 StartZ=0 EndX=178.754 EndY=39.2 EndZ=0
    g4: LineSegment StartX=184.08 StartY=31.3 StartZ=0 EndX=186.139 EndY=31.3 EndZ=0
    g5: LineSegment StartX=190.141 StartY=20.303 StartZ=0 EndX=186.139 EndY=31.3 EndZ=0
    g6: LineSegment StartX=137.815 StartY=39.2 StartZ=0 EndX=156.815 EndY=39.2 EndZ=0
    g7: LineSegment StartX=178.754 StartY=39.2 StartZ=0 EndX=168.815 EndY=39.2 EndZ=0
    g8: LineSegment StartX=156.815 StartY=31.2 StartZ=0 EndX=168.815 EndY=31.2 EndZ=0
    g9: ArcOfCircle CenterX=176.411 CenterY=35.2 CenterZ=0 NormalX=0 NormalY=0 NormalZ=1 AngleXU=0 Radius=20 StartAngle=2.94023 EndAngle=3.34295
    g10: ArcOfCircle CenterX=188.411 CenterY=35.2 CenterZ=0 NormalX=0 NormalY=0 NormalZ=1 AngleXU=0 Radius=20 StartAngle=2.94023 EndAngle=3.34295
    g11: LineSegment StartX=157.815 StartY=39.2 StartZ=0 EndX=167.815 EndY=39.2 EndZ=0
    g12: LineSegment StartX=157.436 StartY=36.2 StartZ=0 EndX=167.436 EndY=36.2 EndZ=0
    g13: ArcOfCircle CenterX=177.411 CenterY=35.2 CenterZ=0 NormalX=0 NormalY=0 NormalZ=1 AngleXU=0 Radius=20 StartAngle=2.94023 EndAngle=3.09157
    g14: ArcOfCircle CenterX=187.411 CenterY=35.2 CenterZ=0 NormalX=0 NormalY=0 NormalZ=1 AngleXU=0 Radius=20 StartAngle=2.94023 EndAngle=3.09157
  constraints (46):
    c: PointOnObject(g0,g-3)
    c: Tangent(g0,g-6)
    c: Coincident(g1,g0)
    c: Horizontal(g1)
    c: Radius(g2) = 3.5
    c: Coincident(g2,g-5)
    c: PointOnObject(g3,g-3)
    c: Parallel(g3,g-4)
    c: Tangent(g3,g2) = 1.5708
    c: Horizontal(g4)
    c: Tangent(g4,g2) = -1.5708
    c: Coincident(g5,g1)
    c: Parallel(g5,g-4)
    c: Coincident(g5,g4)
    c: DistanceX(g4,g-8) = 3.8
    c: Coincident(g6,g0)
    c: PointOnObject(g6,g-3)
    c: Coincident(g7,g3)
    c: PointOnObject(g7,g-3)
    c: Horizontal(g8)
    c: DistanceX(g6,g7) = 12
    c: Vertical(g8,g6)
    c: Vertical(g7,g8)
    c: DistanceY(g8,g6) = 8
    c: Coincident(g9,g8)
    c: Coincident(g9,g6)
    c: Coincident(g10,g7)
    c: Coincident(g10,g8)
    c: Radius(g9) = 20
    c: Radius(g10) = 20
    c: PointOnObject(g11,g-3)
    c: PointOnObject(g11,g-3)
    c: DistanceX(g11,g11) = 10
    c: DistanceX(g6,g11) = 1
    c: Horizontal(g12)
    c: Equal(g12,g11)
    c: DistanceY(g12,g11) = 3
    c: Coincident(g13,g11)
    c: Coincident(g13,g12)
    c: Radius(g13) = 20
    c: Coincident(g14,g11)
    c: Coincident(g14,g12)
    c: Radius(g14) = 20
    c: DistanceX(g0,g6) = 19
    c: Horizontal(g9,g13)
    c: Horizontal(g0,g-4)
FEATURE [Sketcher::SketchObject] Sketch096  label="Sketch096 - forma impugnatura"
  ArcFitTolerance = 1e-06
  AttachmentSupport = -> [Pad019]
  ExternalGeometry = -> [Binder]
  FullyConstrained = true
  MakeInternals = false
  MapMode = 5
  Placement = pos=(0,2,0) rot=(0,0.707107,0.707107;3.14159rad)
  sketch-geometry (8):
    g0: LineSegment StartX=176.685 StartY=-80.4316 StartZ=0 EndX=143.955 EndY=20.303 EndZ=0
    g1: LineSegment StartX=176.685 StartY=-80.4316 StartZ=0 EndX=215.932 EndY=-80.4316 EndZ=0
    g2: Circle CenterX=179.305 CenterY=-76.8316 CenterZ=0 NormalX=0 NormalY=0 NormalZ=1 AngleXU=0 Radius=3
    g3: Circle CenterX=213.443 CenterY=-76.8316 CenterZ=0 NormalX=0 NormalY=0 NormalZ=1 AngleXU=0 Radius=3
    g4: LineSegment StartX=143.955 StartY=20.303 StartZ=0 EndX=202.765 EndY=20.303 EndZ=0
    g5: LineSegment StartX=215.42 StartY=-53.0314 StartZ=0 EndX=192.176 EndY=-3.18451 EndZ=0
    g6: ArcOfCircle CenterX=184.801 CenterY=-67.3089 CenterZ=0 NormalX=0 NormalY=0 NormalZ=1 AngleXU=0 Radius=33.7833 StartAngle=5.88425 EndAngle=6.71952
    g7: ArcOfCircle CenterX=207.583 CenterY=4 CenterZ=0 NormalX=0 NormalY=0 NormalZ=1 AngleXU=0 Radius=17 StartAngle=1.85815 EndAngle=3.57792
  constraints (19):
    c: Coincident(g0,g-4)
    c: PointOnObject(g0,g-3)
    c: Horizontal(g0,g-7)
    c: Coincident(g1,g0)
    c: Coincident(g1,g-5)
    c: Diameter(g2) = 6
    c: Diameter(g3) = 6
    c: Coincident(g2,g-9)
    c: Coincident(g3,g-10)
    c: Coincident(g4,g0)
    c: Coincident(g5,g-6)
    c: Coincident(g6,g1)
    c: Coincident(g6,g5)
    c: Equal(g-5,g6)
    c: Coincident(g5,g-7)
    c: Coincident(g4,g-7)
    c: Tangent(g7,g-7)
    c: Coincident(g7,g4)
    c: Coincident(g7,g5)
FEATURE [Sketcher::SketchObject] Sketch097
  ArcFitTolerance = 1e-06
  AttachmentSupport = -> [Pad019]
  ExternalGeometry = -> [Binder]
  FullyConstrained = true
  MakeInternals = false
  MapMode = 5
  Placement = pos=(0,2,0) rot=(0,0.707107,0.707107;3.14159rad)
  sketch-geometry (4):
    g0: LineSegment StartX=90 StartY=36.8 StartZ=0 EndX=108 EndY=36.8 EndZ=0
    g1: LineSegment StartX=108 StartY=36.8 StartZ=0 EndX=108 EndY=26.8 EndZ=0
    g2: LineSegment StartX=108 StartY=26.8 StartZ=0 EndX=90 EndY=26.8 EndZ=0
    g3: ArcOfCircle CenterX=94 CenterY=31.8 CenterZ=0 NormalX=0 NormalY=0 NormalZ=1 AngleXU=0 Radius=6.40312 StartAngle=2.24554 EndAngle=4.03765
  constraints (13):
    c: Horizontal(g0)
    c: Coincident(g1,g0)
    c: Vertical(g1)
    c: DistanceX(g0,g0) = 18
    c: DistanceY(g1,g1) = 10
    c: Coincident(g2,g1)
    c: Horizontal(g2)
    c: Equal(g2,g0)
    c: DistanceY(g0,g-3) = 2.4
    c: Coincident(g3,g0)
    c: Coincident(g3,g2)
    c: DistanceX(g2,g3) = 4
    c: DistanceX(g-3,g0) = 90
FEATURE [PartDesign::Chamfer] Chamfer015
  Angle = 45
  Base = -> Pad019 [Edge19,Edge22,Edge79]
  BaseFeature = -> Pad019
  ChamferType = 0
  FlipDirection = false
  Refine = true
  Size = 1.9
  Size2 = 1
  SupportTransform = false
  Suppressed = false
  UseAllEdges = false
FEATURE [PartDesign::Pocket] Pocket002
  BaseFeature = -> Chamfer015
  Direction = (0,1,-2e-16)
  Length = 1.2
  Length2 = 5
  Profile = -> Sketch093
  ReferenceAxis = -> Sketch093 [N_Axis]
  Refine = true
  Suppressed = false
  Type = 0
FEATURE [PartDesign::Pad] Pad005
  BaseFeature = -> Pocket002
  Direction = (0,1,-2e-16)
  Length = 1.6
  Length2 = 10
  Profile = -> Sketch091
  ReferenceAxis = -> Sketch091 [N_Axis]
  Refine = true
  Suppressed = false
  Type = 0
FEATURE [Sketcher::SketchObject] Sketch092  label="Sketch092 - scavi per viti anteriori"
  ArcFitTolerance = 1e-06
  AttachmentSupport = -> [Pad005]
  ExternalGeometry = -> [Binder]
  FullyConstrained = true
  MakeInternals = false
  MapMode = 5
  Placement = pos=(0,3.6,0) rot=(0,0.707107,0.707107;3.14159rad)
  sketch-geometry (20):
    g0: ArcOfCircle CenterX=5.6 CenterY=7.6 CenterZ=0 NormalX=0 NormalY=0 NormalZ=1 AngleXU=0 Radius=3.5 StartAngle=0 EndAngle=1.5708
    g1: ArcOfCircle CenterX=5.6 CenterY=34.8 CenterZ=0 NormalX=0 NormalY=0 NormalZ=1 AngleXU=0 Radius=3.5 StartAngle=4.71239 EndAngle=6.28319
    g2: ArcOfCircle CenterX=78.51 CenterY=34.8 CenterZ=0 NormalX=0 NormalY=0 NormalZ=1 AngleXU=0 Radius=3.5 StartAngle=3.14159 EndAngle=4.71239
    g3: ArcOfCircle CenterX=78.51 CenterY=7.6 CenterZ=0 NormalX=0 NormalY=0 NormalZ=1 AngleXU=0 Radius=3.5 StartAngle=1.5708 EndAngle=3.14159
    g4: LineSegment StartX=0 StartY=3.2 StartZ=0 EndX=0 EndY=11.1 EndZ=0
    g5: LineSegment StartX=0 StartY=11.1 StartZ=0 EndX=5.6 EndY=11.1 EndZ=0
    g6: LineSegment StartX=0 StartY=3.2 StartZ=0 EndX=9.1 EndY=3.2 EndZ=0
    g7: LineSegment StartX=9.1 StartY=3.2 StartZ=0 EndX=9.1 EndY=7.6 EndZ=0
    g8: LineSegment StartX=0 StartY=39.2 StartZ=0 EndX=0 EndY=31.3 EndZ=0
    g9: LineSegment StartX=0 StartY=31.3 StartZ=0 EndX=5.6 EndY=31.3 EndZ=0
    g10: LineSegment StartX=0 StartY=39.2 StartZ=0 EndX=9.1 EndY=39.2 EndZ=0
    g11: LineSegment StartX=9.1 StartY=39.2 StartZ=0 EndX=9.1 EndY=34.8 EndZ=0
    g12: LineSegment StartX=82.8 StartY=39.2 StartZ=0 EndX=75.01 EndY=39.2 EndZ=0
    g13: LineSegment StartX=82.8 StartY=39.2 StartZ=0 EndX=82.8 EndY=31.3 EndZ=0
    g14: LineSegment StartX=82.8 StartY=31.3 StartZ=0 EndX=78.51 EndY=31.3 EndZ=0
    g15: LineSegment StartX=82.8 StartY=3.2 StartZ=0 EndX=75.01 EndY=3.2 EndZ=0
    g16: LineSegment StartX=75.01 StartY=3.2 StartZ=0 EndX=75.01 EndY=7.6 EndZ=0
    g17: LineSegment StartX=82.8 StartY=3.2 StartZ=0 EndX=82.8 EndY=11.1 EndZ=0
    g18: LineSegment StartX=82.8 StartY=11.1 StartZ=0 EndX=78.51 EndY=11.1 EndZ=0
    g19: LineSegment StartX=75.01 StartY=39.2 StartZ=0 EndX=75.01 EndY=34.8 EndZ=0
  constraints (48):
    c: Radius(g0) = 3.5
    c: Coincident(g0,g-10)
    c: Radius(g1) = 3.5
    c: Coincident(g1,g-9)
    c: Radius(g2) = 3.5
    c: Coincident(g2,g-8)
    c: Radius(g3) = 3.5
    c: Coincident(g3,g-7)
    c: Coincident(g4,g-5)
    c: PointOnObject(g4,g-4)
    c: Coincident(g5,g4)
    c: Horizontal(g5)
    c: Coincident(g6,g4)
    c: PointOnObject(g6,g-5)
    c: Coincident(g7,g6)
    c: Vertical(g7)
    c: Coincident(g8,g-4)
    c: PointOnObject(g8,g-4)
    c: Coincident(g9,g8)
    c: Horizontal(g9)
    c: Coincident(g10,g8)
    c: PointOnObject(g10,g-3)
    c: Coincident(g11,g10)
    c: Vertical(g11)
    c: PointOnObject(g12,g-3)
    c: PointOnObject(g12,g-3)
    c: Coincident(g13,g12)
    c: Vertical(g13)
    c: Coincident(g14,g13)
    c: Horizontal(g14)
    c: Coincident(g15,g-6)
    c: PointOnObject(g15,g-5)
    c: Coincident(g16,g15)
    c: Vertical(g16)
    c: Coincident(g17,g15)
    c: Coincident(g18,g17)
    c: Horizontal(g18)
    c: Tangent(g3,g18) = -1.5708
    c: Tangent(g16,g3) = 1.5708
    c: Coincident(g19,g12)
    c: Vertical(g19)
    c: Tangent(g2,g19) = -1.5708
    c: Tangent(g2,g14) = 1.5708
    c: Tangent(g0,g7) = -1.5708
    c: Tangent(g0,g5) = 1.5708
    c: Tangent(g9,g1) = -1.5708
    c: Tangent(g1,g11) = 1.5708
    c: Tangent(g17,g13)
FEATURE [PartDesign::Pocket] Pocket001
  BaseFeature = -> Pad005
  Direction = (0,-1,2e-16)
  Length = 1.6
  Length2 = 5
  Profile = -> Sketch092
  ReferenceAxis = -> Sketch092 [N_Axis]
  Refine = true
  Suppressed = false
  Type = 0
FEATURE [PartDesign::Pad] Pad006
  BaseFeature = -> Pocket001
  Direction = (0,1,-2e-16)
  Length = 0.8
  Length2 = 10
  Profile = -> Sketch094
  ReferenceAxis = -> Sketch094 [N_Axis]
  Refine = true
  Suppressed = false
  Type = 0
FEATURE [PartDesign::Pad] Pad007
  BaseFeature = -> Pad006
  Direction = (0,1,-2e-16)
  Length = 2
  Length2 = 10
  Profile = -> Sketch095
  ReferenceAxis = -> Sketch095 [N_Axis]
  Refine = true
  Suppressed = false
  Type = 0
FEATURE [PartDesign::Pad] Pad008  label="Pad008 - forma impugnatura"
  BaseFeature = -> Pad007
  Direction = (0,1,-2e-16)
  Length = 1.6
  Length2 = 10
  Profile = -> Sketch096
  ReferenceAxis = -> Sketch096 [N_Axis]
  Refine = true
  Suppressed = false
  Type = 0
FEATURE [PartDesign::Pad] Pad009
  BaseFeature = -> Pad008
  Direction = (0,1,-2e-16)
  Length = 1.6
  Length2 = 10
  Profile = -> Sketch097
  ReferenceAxis = -> Sketch097 [N_Axis]
  Refine = true
  Suppressed = false
  Type = 0
FEATURE [Sketcher::SketchObject] Sketch098
  ArcFitTolerance = 1e-06
  AttachmentSupport = -> [Pad006]
  ExternalGeometry = -> [Binder]
  FullyConstrained = true
  MakeInternals = false
  MapMode = 5
  Placement = pos=(0,2.8,-7e-16) rot=(0,0.707107,0.707107;3.14159rad)
  sketch-geometry (4):
    g0: LineSegment StartX=118 StartY=39.2 StartZ=0 EndX=129 EndY=39.2 EndZ=0
    g1: LineSegment StartX=120.599 StartY=31.2 StartZ=0 EndX=131.599 EndY=31.2 EndZ=0
    g2: LineSegment StartX=129 StartY=39.2 StartZ=0 EndX=131.599 EndY=31.2 EndZ=0
    g3: LineSegment StartX=118 StartY=39.2 StartZ=0 EndX=120.599 EndY=31.2 EndZ=0
  constraints (12):
    c: PointOnObject(g0,g-3)
    c: PointOnObject(g0,g-3)
    c: DistanceX(g0,g0) = 11
    c: Horizontal(g1)
    c: Equal(g1,g0)
    c: Coincident(g2,g0)
    c: Coincident(g3,g0)
    c: Parallel(g-4,g2)
    c: Coincident(g1,g2)
    c: Coincident(g1,g3)
    c: DistanceY(g1,g0) = 8
    c: DistanceX(g-3,g0) = 118
FEATURE [Sketcher::SketchObject] Sketch099
  ArcFitTolerance = 1e-06
  AttachmentSupport = -> [Pad008]
  ExternalGeometry = -> [Binder]
  FullyConstrained = true
  MakeInternals = false
  MapMode = 5
  Placement = pos=(0,3.6,0) rot=(0,0.707107,0.707107;3.14159rad)
  sketch-geometry (13):
    g0: LineSegment StartX=192.176 StartY=-3.18451 StartZ=0 EndX=196.804 EndY=-13.1108 EndZ=0
    g1: LineSegment [constr] StartX=202.765 StartY=20.303 StartZ=0 EndX=181.223 EndY=20.303 EndZ=0
    g2: LineSegment [constr] StartX=181.223 StartY=20.303 StartZ=0 EndX=181.223 EndY=-3.18451 EndZ=0
    g3: ArcOfCircle CenterX=181.223 CenterY=-20.3764 CenterZ=0 NormalX=0 NormalY=0 NormalZ=1 AngleXU=0 Radius=17.1918 StartAngle=0.436332 EndAngle=1.57079
    g4: ArcOfEllipse CenterX=181.223 CenterY=8.55923 CenterZ=0 NormalX=0 NormalY=0 NormalZ=1 MajorRadius=23.4779 MinorRadius=11.7437 AngleXU=0 StartAngle=1.5708 EndAngle=4.71239
    g5: LineSegment [constr] StartX=204.701 StartY=8.55923 StartZ=0 EndX=157.745 EndY=8.55923 EndZ=0
    g6: LineSegment [constr] StartX=181.223 StartY=20.303 StartZ=0 EndX=181.223 EndY=-3.18451 EndZ=0
    g7: GeomPoint [constr] X=201.553 Y=8.55923 Z=0
    g8: GeomPoint [constr] X=160.894 Y=8.55923 Z=0
    g9: GeomPoint [constr] X=181.223 Y=-3.18451 Z=0
    g10: LineSegment StartX=181.223 StartY=20.303 StartZ=0 EndX=202.765 EndY=20.303 EndZ=0
    g11: ArcOfCircle CenterX=207.583 CenterY=4 CenterZ=0 NormalX=0 NormalY=0 NormalZ=1 AngleXU=0 Radius=17 StartAngle=1.85815 EndAngle=3.57792
    g12: LineSegment [constr] StartX=172.411 StartY=39.2 StartZ=0 EndX=192.176 EndY=-3.18451 EndZ=0
  constraints (27):
    c: Coincident(g1,g-7)
    c: Horizontal(g1)
    c: Coincident(g2,g1)
    c: Vertical(g2)
    c: Horizontal(g2,g0)
    c: Coincident(g3,g0)
    c: Coincident(g3,g2)
    c: InternalAlignment(g5-g8 -> g4) x4
    c: Horizontal(g5)
    c: PointOnObject(g4,g2)
    c: Coincident(g4,g1)
    c: DistanceX(g-3,g5) = 10.1
    c: Coincident(g4,g2)
    c: Tangent(g3,g-5)
    c: PointOnObject(g9,g4)
    c: PointOnObject(g9,g3)
    c: Tangent(g4,g3,g9) = 1.5708
    c: Coincident(g10,g1)
    c: Coincident(g10,g1)
    c: Equal(g11,g-4)
    c: Coincident(g11,g1)
    c: Coincident(g11,g0)
    c: PointOnObject(g12,g-6)
    c: PointOnObject(g1,g12)
    c: Tangent(g12,g-5) = -1.5708
    c: Tangent(g0,g-5) = -1.5708
    c: Horizontal(g9,g12)
FEATURE [Sketcher::SketchObject] Sketch106  label="Sketch106 - smusso impuniatura interno"
  ArcFitTolerance = 1e-06
  AttachmentSupport = -> [Pad008]
  ExternalGeometry = -> [Pad008]
  FullyConstrained = true
  MakeInternals = false
  MapMode = 5
  Placement = pos=(0,-1.586e-13,-80.4316) rot=(1,0,0;3.14159rad)
  sketch-geometry (9):
    g0: LineSegment StartX=-176.685 StartY=-3.6 StartZ=0 EndX=-176.685 EndY=-1.452e-13 EndZ=0
    g1: LineSegment [constr] StartX=-176.685 StartY=-1.416e-13 StartZ=0 EndX=-176.685 EndY=-1.452e-13 EndZ=0
    g2: LineSegment [constr] StartX=-186.685 StartY=-3.6 StartZ=0 EndX=-186.685 EndY=-1.452e-13 EndZ=0
    g3: ArcOfEllipse CenterX=-186.685 CenterY=-1.452e-13 CenterZ=0 NormalX=0 NormalY=0 NormalZ=1 MajorRadius=10 MinorRadius=3.6 AngleXU=3.14159 StartAngle=1.5708 EndAngle=3.14159
    g4: LineSegment [constr] StartX=-196.685 StartY=-1.416e-13 StartZ=0 EndX=-176.685 EndY=-1.416e-13 EndZ=0
    g5: LineSegment [constr] StartX=-186.685 StartY=-3.6 StartZ=0 EndX=-186.685 EndY=3.6 EndZ=0
    g6: GeomPoint [constr] X=-196.015 Y=-1.416e-13 Z=0
    g7: GeomPoint [constr] X=-177.356 Y=-1.416e-13 Z=0
    g8: LineSegment StartX=-176.685 StartY=-3.6 StartZ=0 EndX=-186.685 EndY=-3.6 EndZ=0
  constraints (15):
    c: PointOnObject(g2,g-3)
    c: Coincident(g1,g-5)
    c: DistanceY(g1,g1) = 0
    c: Coincident(g0,g1)
    c: DistanceX(g2,g-5) = 10
    c: Vertical(g2)
    c: Horizontal(g2,g0)
    c: InternalAlignment(g4-g7 -> g3) x4
    c: Coincident(g3,g2)
    c: Horizontal(g4)
    c: Coincident(g3,g0)
    c: Tangent(g0,g-5) = 1.5708
    c: Coincident(g3,g2)
    c: Coincident(g8,g0)
    c: Coincident(g8,g2)
FEATURE [Sketcher::SketchObject] Sketch107  label="Sketch107 - smusso impugnatura esterno"
  ArcFitTolerance = 1e-06
  AttachmentSupport = -> [Pad008]
  ExternalGeometry = -> [Pad008]
  FullyConstrained = true
  MakeInternals = false
  MapMode = 5
  Placement = pos=(0,-1.586e-13,-80.4316) rot=(1,0,0;3.14159rad)
  sketch-geometry (9):
    g0: LineSegment [constr] StartX=-215.932 StartY=1.79e-14 StartZ=0 EndX=-215.932 EndY=2.71e-14 EndZ=0
    g1: LineSegment StartX=-215.932 StartY=-3.6 StartZ=0 EndX=-215.932 EndY=2.71e-14 EndZ=0
    g2: LineSegment StartX=-215.932 StartY=-3.6 StartZ=0 EndX=-205.932 EndY=-3.6 EndZ=0
    g3: LineSegment [constr] StartX=-205.932 StartY=-3.6 StartZ=0 EndX=-205.932 EndY=2.71e-14 EndZ=0
    g4: ArcOfEllipse CenterX=-205.932 CenterY=2.71e-14 CenterZ=0 NormalX=0 NormalY=0 NormalZ=1 MajorRadius=10 MinorRadius=3.6 AngleXU=3.14159 StartAngle=1e-16 EndAngle=1.5708
    g5: LineSegment [constr] StartX=-215.932 StartY=1.79e-14 StartZ=0 EndX=-195.932 EndY=1.79e-14 EndZ=0
    g6: LineSegment [constr] StartX=-205.932 StartY=-3.6 StartZ=0 EndX=-205.932 EndY=3.6 EndZ=0
    g7: GeomPoint [constr] X=-215.262 Y=2.76e-14 Z=0
    g8: GeomPoint [constr] X=-196.602 Y=1.78e-14 Z=0
  constraints (16):
    c: Coincident(g0,g-6)
    c: PointOnObject(g0,g-6)
    c: DistanceY(g0,g0) = 0
    c: Coincident(g1,g-6)
    c: Coincident(g1,g0)
    c: Tangent(g2,g-3)
    c: DistanceX(g2,g2) = 10
    c: Coincident(g3,g2)
    c: Vertical(g3)
    c: Horizontal(g3,g0)
    c: InternalAlignment(g5-g8 -> g4) x4
    c: Coincident(g4,g3)
    c: Horizontal(g5)
    c: Coincident(g4,g0)
    c: Coincident(g4,g2)
    c: PointOnObject(g2,g1)
FEATURE [Sketcher::SketchObject] Sketch108
  ArcFitTolerance = 1e-06
  AttachmentOffset = pos=(0,0,-1.6) rot=(0,0,1;0rad)
  AttachmentSupport = -> [Pad008]
  ExternalGeometry = -> [Binder]
  FullyConstrained = true
  MakeInternals = false
  MapMode = 5
  Placement = pos=(0,2,4e-16) rot=(0,0.707107,0.707107;3.14159rad)
  sketch-geometry (14):
    g0: LineSegment StartX=192.176 StartY=-3.18451 StartZ=0 EndX=193.827 EndY=-6.72678 EndZ=0
    g1: LineSegment [constr] StartX=202.765 StartY=20.303 StartZ=0 EndX=181.223 EndY=20.303 EndZ=0
    g2: LineSegment [constr] StartX=181.223 StartY=20.303 StartZ=0 EndX=181.223 EndY=1.30297 EndZ=0
    g3: ArcOfCircle CenterX=181.223 CenterY=-12.6042 CenterZ=0 NormalX=0 NormalY=0 NormalZ=1 AngleXU=0 Radius=13.9072 StartAngle=0.436332 EndAngle=1.5708
    g4: ArcOfEllipse CenterX=181.223 CenterY=10.803 CenterZ=0 NormalX=0 NormalY=0 NormalZ=1 MajorRadius=14.4779 MinorRadius=9.5 AngleXU=0 StartAngle=1.5708 EndAngle=4.71239
    g5: LineSegment [constr] StartX=195.701 StartY=10.803 StartZ=0 EndX=166.745 EndY=10.803 EndZ=0
    g6: LineSegment [constr] StartX=181.223 StartY=20.303 StartZ=0 EndX=181.223 EndY=1.30297 EndZ=0
    g7: GeomPoint [constr] X=192.148 Y=10.803 Z=0
    g8: GeomPoint [constr] X=170.298 Y=10.803 Z=0
    g9: LineSegment StartX=181.223 StartY=20.303 StartZ=0 EndX=202.765 EndY=20.303 EndZ=0
    g10: ArcOfCircle CenterX=207.583 CenterY=4 CenterZ=0 NormalX=0 NormalY=0 NormalZ=1 AngleXU=0 Radius=17 StartAngle=1.85815 EndAngle=3.57792
    g11: LineSegment [constr] StartX=172.411 StartY=39.2 StartZ=0 EndX=192.176 EndY=-3.18451 EndZ=0
    g12: GeomPoint [constr] X=181.223 Y=1.30297 Z=0
    g13: GeomPoint [constr] X=181.223 Y=1.30297 Z=0
  constraints (28):
    c: Coincident(g1,g-7)
    c: Horizontal(g1)
    c: Coincident(g2,g1)
    c: Vertical(g2)
    c: Coincident(g3,g2)
    c: InternalAlignment(g5-g8 -> g4) x4
    c: Horizontal(g5)
    c: PointOnObject(g4,g2)
    c: Coincident(g4,g1)
    c: DistanceX(g-3,g5) = 19.1
    c: Coincident(g4,g2)
    c: Coincident(g9,g1)
    c: Coincident(g9,g1)
    c: Coincident(g10,g1)
    c: Coincident(g10,g0)
    c: PointOnObject(g11,g-6)
    c: PointOnObject(g1,g11)
    c: DistanceY(g2,g1) = 19
    c: Coincident(g10,g-4)
    c: PointOnObject(g12,g4)
    c: PointOnObject(g12,g3)
    c: Tangent(g11,g-5) = -1.5708
    c: Tangent(g0,g-5) = -1.5708
    c: Tangent(g3,g0) = 1.5708
    c: PointOnObject(g13,g4)
    c: PointOnObject(g13,g3)
    c: Tangent(g4,g3,g13) = 1.5708
    c: Horizontal(g11,g0)
FEATURE [Part::Part2DObjectPython] Clone2D  label="Sketch108 (2D)"  # Draft 2D object (typed FeaturePython)
  Fuse = false
  Objects = -> [Sketch108]
  Placement = pos=(0,2,4e-16) rot=(0,0.707107,0.707107;3.14159rad)
  Scale = (1,1,1)
FEATURE [Sketcher::SketchObject] Sketch109
  ArcFitTolerance = 1e-06
  AttachmentOffset = pos=(0,0,-3.5) rot=(0,0,1;0rad)
  AttachmentSupport = -> [Pad008]
  ExternalGeometry = -> [Binder]
  FullyConstrained = true
  MakeInternals = false
  MapMode = 5
  Placement = pos=(0,0.1,8e-16) rot=(0,0.707107,0.707107;3.14159rad)
  sketch-geometry (1):
    g0: GeomPoint X=197.47 Y=8.55923 Z=0
  constraints (1):
    c: Symmetric(g-7,g-5,g0)
FEATURE [PartDesign::Chamfer] Chamfer005
  Angle = 45
  Base = -> Pad009 [Edge215,Edge212]
  BaseFeature = -> Pad009
  ChamferType = 1
  FlipDirection = false
  Refine = true
  Size = 1.5
  Size2 = 2.8
  SupportTransform = false
  Suppressed = false
  UseAllEdges = false
FEATURE [Sketcher::SketchObject] Sketch111
  ArcFitTolerance = 1e-06
  AttachmentSupport = -> [Pad009]
  ExternalGeometry = -> [Pad009]
  FullyConstrained = true
  MakeInternals = false
  MapMode = 5
  Placement = pos=(0,3.6,-8e-16) rot=(0,0.707107,0.707107;3.14159rad)
  sketch-geometry (21):
    g0: LineSegment [constr] StartX=97 StartY=36.8 StartZ=0 EndX=97 EndY=26.8 EndZ=0
    g1: LineSegment StartX=97 StartY=28.6 StartZ=0 EndX=97 EndY=27.8 EndZ=0
    g2: LineSegment StartX=97 StartY=27.8 StartZ=0 EndX=108 EndY=27.8 EndZ=0
    g3: LineSegment StartX=108 StartY=27.8 StartZ=0 EndX=108 EndY=28.6 EndZ=0
    g4: LineSegment StartX=108 StartY=28.6 StartZ=0 EndX=97 EndY=28.6 EndZ=0
    g5: LineSegment StartX=97 StartY=35.8 StartZ=0 EndX=97 EndY=35 EndZ=0
    g6: LineSegment StartX=97 StartY=35 StartZ=0 EndX=108 EndY=35 EndZ=0
    g7: LineSegment StartX=108 StartY=35 StartZ=0 EndX=108 EndY=35.8 EndZ=0
    g8: LineSegment StartX=108 StartY=35.8 StartZ=0 EndX=97 EndY=35.8 EndZ=0
    g9: LineSegment StartX=97 StartY=30.4 StartZ=0 EndX=97 EndY=29.6 EndZ=0
    g10: LineSegment StartX=97 StartY=29.6 StartZ=0 EndX=108 EndY=29.6 EndZ=0
    g11: LineSegment StartX=108 StartY=29.6 StartZ=0 EndX=108 EndY=30.4 EndZ=0
    g12: LineSegment StartX=108 StartY=30.4 StartZ=0 EndX=97 EndY=30.4 EndZ=0
    g13: LineSegment StartX=97 StartY=34 StartZ=0 EndX=97 EndY=33.2 EndZ=0
    g14: LineSegment StartX=97 StartY=33.2 StartZ=0 EndX=108 EndY=33.2 EndZ=0
    g15: LineSegment StartX=108 StartY=33.2 StartZ=0 EndX=108 EndY=34 EndZ=0
    g16: LineSegment StartX=108 StartY=34 StartZ=0 EndX=97 EndY=34 EndZ=0
    g17: LineSegment StartX=97 StartY=32.2 StartZ=0 EndX=97 EndY=31.4 EndZ=0
    g18: LineSegment StartX=97 StartY=31.4 StartZ=0 EndX=108 EndY=31.4 EndZ=0
    g19: LineSegment StartX=108 StartY=31.4 StartZ=0 EndX=108 EndY=32.2 EndZ=0
    g20: LineSegment StartX=108 StartY=32.2 StartZ=0 EndX=97 EndY=32.2 EndZ=0
  constraints (54):
    c: Vertical(g0)
    c: PointOnObject(g0,g-3)
    c: PointOnObject(g0,g-4)
    c: DistanceX(g0,g-5) = 11
    c: Coincident(g1,g2)
    c: Coincident(g2,g3)
    c: Coincident(g3,g4)
    c: Coincident(g4,g1)
    c: Horizontal(g2)
    c: Horizontal(g4)
    c: Tangent(g1,g0)
    c: Tangent(g3,g-5)
    c: DistanceY(g2,g3) = 0.8
    c: Coincident(g5,g6)
    c: Coincident(g6,g7)
    c: Coincident(g7,g8)
    c: Coincident(g8,g5)
    c: Horizontal(g6)
    c: Horizontal(g8)
    c: DistanceY(g6,g7) = 0.8
    c: Coincident(g9,g10)
    c: Coincident(g10,g11)
    c: Coincident(g11,g12)
    c: Coincident(g12,g9)
    c: Horizontal(g10)
    c: Horizontal(g12)
    c: DistanceY(g10,g11) = 0.8
    c: Tangent(g5,g0)
    c: Tangent(g7,g-5)
    c: Tangent(g9,g0)
    c: Tangent(g11,g-5)
    c: Coincident(g13,g14)
    c: Coincident(g14,g15)
    c: Coincident(g15,g16)
    c: Coincident(g16,g13)
    c: Horizontal(g14)
    c: Horizontal(g16)
    c: DistanceY(g14,g15) = 0.8
    c: Tangent(g13,g0)
    c: Tangent(g15,g-5)
    c: Coincident(g17,g18)
    c: Coincident(g18,g19)
    c: Coincident(g19,g20)
    c: Coincident(g20,g17)
    c: Horizontal(g18)
    c: Horizontal(g20)
    c: DistanceY(g18,g19) = 0.8
    c: Tangent(g17,g0)
    c: Tangent(g19,g-5)
    c: DistanceY(g1,g9) = 1
    c: DistanceY(g9,g17) = 1
    c: DistanceY(g17,g13) = 1
    c: DistanceY(g13,g5) = 1
    c: DistanceY(g0,g1) = 1
FEATURE [PartDesign::Pocket] Pocket004
  BaseFeature = -> Chamfer005
  Direction = (0,-1,2e-16)
  Length = 1
  Length2 = 5
  Profile = -> Sketch111
  ReferenceAxis = -> Sketch111 [N_Axis]
  Refine = true
  Suppressed = false
  Type = 0
FEATURE [PartDesign::Pad] Pad010
  BaseFeature = -> Pocket004
  Direction = (0,1,-2e-16)
  Length = 1.2
  Length2 = 10
  Profile = -> Sketch098
  ReferenceAxis = -> Sketch098 [N_Axis]
  Refine = true
  Suppressed = false
  Type = 0
FEATURE [PartDesign::Chamfer] Chamfer006
  Angle = 45
  Base = -> Pad010 [Edge291]
  BaseFeature = -> Pad010
  ChamferType = 1
  FlipDirection = false
  Refine = true
  Size = 1
  Size2 = 6
  SupportTransform = false
  Suppressed = false
  UseAllEdges = false
FEATURE [Sketcher::SketchObject] Sketch110
  ArcFitTolerance = 1e-06
  AttachmentSupport = -> [Pad010]
  ExternalGeometry = -> [Sketch098]
  FullyConstrained = true
  MakeInternals = false
  MapMode = 5
  Placement = pos=(0,4,-9e-16) rot=(0,0.707107,0.707107;3.14159rad)
  sketch-geometry (8):
    g0: LineSegment StartX=119.69 StartY=34 StartZ=0 EndX=130.69 EndY=34 EndZ=0
    g1: LineSegment StartX=119.95 StartY=33.2 StartZ=0 EndX=130.95 EndY=33.2 EndZ=0
    g2: LineSegment StartX=119.137 StartY=35.7 StartZ=0 EndX=130.137 EndY=35.7 EndZ=0
    g3: LineSegment StartX=118.877 StartY=36.5 StartZ=0 EndX=129.877 EndY=36.5 EndZ=0
    g4: LineSegment StartX=118.877 StartY=36.5 StartZ=0 EndX=119.137 EndY=35.7 EndZ=0
    g5: LineSegment StartX=129.877 StartY=36.5 StartZ=0 EndX=130.137 EndY=35.7 EndZ=0
    g6: LineSegment StartX=119.69 StartY=34 StartZ=0 EndX=119.95 EndY=33.2 EndZ=0
    g7: LineSegment StartX=130.69 StartY=34 StartZ=0 EndX=130.95 EndY=33.2 EndZ=0
  constraints (24):
    c: Horizontal(g0)
    c: Horizontal(g1)
    c: Horizontal(g2)
    c: Horizontal(g3)
    c: Equal(g1,g-5)
    c: Equal(g0,g-5)
    c: Equal(g2,g-5)
    c: Equal(g3,g-5)
    c: PointOnObject(g0,g-3)
    c: PointOnObject(g1,g-3)
    c: PointOnObject(g2,g-3)
    c: PointOnObject(g3,g-3)
    c: Coincident(g4,g3)
    c: Coincident(g4,g2)
    c: Coincident(g5,g3)
    c: Coincident(g5,g2)
    c: Coincident(g6,g0)
    c: Coincident(g6,g1)
    c: Coincident(g7,g0)
    c: Coincident(g7,g1)
    c: DistanceY(g1,g0) = 0.8
    c: DistanceY(g2,g3) = 0.8
    c: DistanceY(g-5,g1) = 2
    c: DistanceY(g-5,g2) = 4.5
FEATURE [PartDesign::Pocket] Pocket003
  BaseFeature = -> Chamfer006
  Direction = (0,-1,2e-16)
  Length = 1
  Length2 = 5
  Profile = -> Sketch110
  ReferenceAxis = -> Sketch110 [N_Axis]
  Refine = true
  Suppressed = false
  Type = 0
FEATURE [PartDesign::SubtractivePipe] SubtractivePipe
  AuxilleryCurvelinear = true
  AuxillerySpineTangent = false
  BaseFeature = -> Pocket003
  Binormal = (0,0,0)
  Mode = 0
  Profile = -> Sketch106
  Refine = true
  Spine = -> Pad008 [Edge215]
  SpineTangent = false
  Suppressed = false
  Transformation = 0
  Transition = 0
FEATURE [PartDesign::SubtractivePipe] SubtractivePipe001
  AuxilleryCurvelinear = true
  AuxillerySpineTangent = false
  BaseFeature = -> SubtractivePipe
  Binormal = (0,0,0)
  Mode = 0
  Profile = -> Sketch107
  Refine = true
  Spine = -> Pad008 [Edge213,Edge216,Edge210]
  SpineTangent = false
  Suppressed = false
  Transformation = 0
  Transition = 0
FEATURE [PartDesign::SubtractiveLoft] SubtractiveLoft
  BaseFeature = -> SubtractivePipe001
  Closed = false
  Profile = -> Sketch099
  Refine = true
  Ruled = false
  Sections = -> [Sketch108]
  Suppressed = false
FEATURE [PartDesign::SubtractiveLoft] SubtractiveLoft001
  BaseFeature = -> SubtractiveLoft
  Closed = false
  Profile = -> Clone2D
  Refine = true
  Ruled = false
  Sections = -> [Sketch109]
  Suppressed = false
FEATURE [Sketcher::SketchObject] Sketch112
  ArcFitTolerance = 1e-06
  AttachmentSupport = -> [Pad008]
  ExternalGeometry = -> [Binder]
  FullyConstrained = true
  MakeInternals = false
  MapMode = 5
  Placement = pos=(0,3.6,0) rot=(0,0.707107,0.707107;3.14159rad)
  sketch-geometry (4):
    g0: LineSegment [constr] StartX=167.782 StartY=-53.0314 StartZ=0 EndX=215.42 EndY=-53.0314 EndZ=0
    g1: GeomPoint [constr] X=191.282 Y=-53.0314 Z=0
    g2: Circle CenterX=191.282 CenterY=-53.0314 CenterZ=0 NormalX=0 NormalY=0 NormalZ=1 AngleXU=0 Radius=11.5
    g3: Circle CenterX=191.282 CenterY=-53.0314 CenterZ=0 NormalX=0 NormalY=0 NormalZ=1 AngleXU=0 Radius=10.7
  constraints (9):
    c: Horizontal(g0)
    c: PointOnObject(g0,g-3)
    c: Diameter(g2) = 23
    c: Coincident(g2,g1)
    c: Diameter(g3) = 21.4
    c: Coincident(g3,g1)
    c: DistanceX(g0,g1) = 23.5
    c: PointOnObject(g1,g0)
    c: Coincident(g0,g-4)
FEATURE [PartDesign::Chamfer] Chamfer016
  Angle = 45
  Base = -> SubtractiveLoft001 [Edge118,Edge117,Edge119,Edge120,Edge109]
  BaseFeature = -> SubtractiveLoft001
  ChamferType = 0
  FlipDirection = false
  Refine = true
  Size = 1.5
  Size2 = 1
  SupportTransform = false
  Suppressed = false
  UseAllEdges = false
FEATURE [PartDesign::Chamfer] Chamfer017
  Angle = 45
  Base = -> Chamfer016 [Edge15]
  BaseFeature = -> Chamfer016
  ChamferType = 0
  FlipDirection = false
  Refine = true
  Size = 1.6
  Size2 = 1
  SupportTransform = false
  Suppressed = false
  UseAllEdges = false
FEATURE [PartDesign::Chamfer] Chamfer018
  Angle = 45
  Base = -> Chamfer017 [Edge10]
  BaseFeature = -> Chamfer017
  ChamferType = 0
  FlipDirection = false
  Refine = true
  Size = 3.5
  Size2 = 1
  SupportTransform = false
  Suppressed = false
  UseAllEdges = false
FEATURE [PartDesign::Chamfer] Chamfer019
  Angle = 45
  Base = -> Chamfer018 [Edge94,Edge199]
  BaseFeature = -> Chamfer018
  ChamferType = 0
  FlipDirection = false
  Refine = true
  Size = 1.9
  Size2 = 1
  SupportTransform = false
  Suppressed = false
  UseAllEdges = false
FEATURE [PartDesign::Fillet] Fillet009
  Base = -> Chamfer019 [Edge83]
  BaseFeature = -> Chamfer019
  Radius = 1.1
  Refine = true
  SupportTransform = false
  Suppressed = false
  UseAllEdges = false
FEATURE [PartDesign::Fillet] Fillet010
  Base = -> Fillet009 [Edge77]
  BaseFeature = -> Fillet009
  Radius = 1.9
  Refine = true
  SupportTransform = false
  Suppressed = false
  UseAllEdges = false
FEATURE [PartDesign::Pocket] Pocket005
  BaseFeature = -> Fillet010
  Direction = (0,-1,2e-16)
  Length = 0.8
  Length2 = 5
  Profile = -> Sketch112
  ReferenceAxis = -> Sketch112 [N_Axis]
  Refine = true
  Suppressed = false
  Type = 0
FEATURE [Part::Part2DObjectPython] ShapeString001  # Draft 2D object (typed FeaturePython)
  FontFile = <path>
  Fuse = false
  Justification = 6
  JustificationReference = 0
  KeepLeftMargin = false
  MakeFace = true
  ObliqueAngle = 0
  Placement = pos=(-183.5,3.6,-57.5) rot=(0,0.707107,0.707107;3.14159rad)
  ScaleToSize = true
  Size = 10
  String = AS
  Tracking = 0
FEATURE [PartDesign::Pocket] Pocket013
  BaseFeature = -> Pocket005
  Direction = (-1e-16,-1,2e-16)
  Length = 1
  Length2 = 5
  Profile = -> ShapeString001
  ReferenceAxis = -> ShapeString001 [N_Axis]
  Refine = true
  Suppressed = false
  Type = 0
FEATURE [PartDesign::Body] Body006  label="lato SX"
  AllowCompound = false
  Group = -> [Binder,Pad019,Chamfer015,Pocket002,Sketch133,Sketch091,Pad005,Sketch092,Pocket001,Sketch093,Sketch094,Pad006,Sketch095,Pad007,Sketch096,Pad008,Sketch097,Pad009,Chamfer005,Pocket004,Sketch098,Pad010,Chamfer006,Pocket003,SubtractivePipe,SubtractivePipe001,Sketch099,Sketch106,Sketch107,Sketch108,Clone2D,Sketch109,SubtractiveLoft,SubtractiveLoft001,Sketch110,Sketch111,Sketch112,Chamfer016,Chamfer017,+7 more]
  Origin = -> Origin006
  Tip = -> Pocket013
FEATURE [PartDesign::Pad] Pad020
  Direction = (0,-1,2e-16)
  Length = 25.2
  Length2 = 10
  Midplane = true
  Placement = pos=(0,0,0) rot=(1,0,0;1.5708rad)
  Profile = -> Sketch021
  ReferenceAxis = -> Sketch021 [N_Axis]
  Refine = true
  Suppressed = false
  Type = 0
FEATURE [PartDesign::Body] Body001  label="perno fermo rumble e driver solenoide"
  AllowCompound = false
  Group = -> [Sketch021,Pad020]
  Origin = -> Origin001
  Tip = -> Pad020
FEATURE [PartDesign::Pad] Pad021
  Direction = (0,-1,2e-16)
  Length = 16.8
  Length2 = 10
  Midplane = true
  Placement = pos=(0,0,0) rot=(1,0,0;1.5708rad)
  Profile = -> Sketch061
  ReferenceAxis = -> Sketch061 [N_Axis]
  Refine = true
  Suppressed = false
  Type = 0
FEATURE [PartDesign::Pocket] Pocket014
  BaseFeature = -> Pad021
  Direction = (0,1,-2e-16)
  Length = 12.8
  Length2 = 5
  Midplane = true
  Placement = pos=(0,0,0) rot=(1,0,0;1.5708rad)
  Profile = -> Sketch062
  ReferenceAxis = -> Sketch062 [N_Axis]
  Refine = true
  Suppressed = false
  Type = 0
FEATURE [PartDesign::Pad] Pad022
  BaseFeature = -> Pocket014
  Direction = (0,-1,2e-16)
  Length = 7.6
  Length2 = 10
  Midplane = true
  Placement = pos=(0,0,0) rot=(1,0,0;1.5708rad)
  Profile = -> Sketch063
  ReferenceAxis = -> Sketch063 [N_Axis]
  Refine = true
  Suppressed = false
  Type = 0
FEATURE [PartDesign::Body] Body003  label="blocco switch"
  AllowCompound = false
  Group = -> [Sketch061,Sketch062,Sketch063,Pad021,Pocket014,Pad022]
  Origin = -> Origin003
  Tip = -> Pad022
FEATURE [PartDesign::Pad] Pad024
  Direction = (0,-1,2e-16)
  Length = 17
  Length2 = 10
  Midplane = true
  Placement = pos=(0,0,0) rot=(1,0,0;1.5708rad)
  Profile = -> Sketch045
  ReferenceAxis = -> Sketch045 [N_Axis]
  Refine = true
  Suppressed = false
  Type = 0
FEATURE [PartDesign::Pocket] Pocket015
  BaseFeature = -> Pad024
  Direction = (-1,0,0)
  Length = 8
  Length2 = 5
  Placement = pos=(0,0,0) rot=(1,0,0;1.5708rad)
  Profile = -> Sketch047
  ReferenceAxis = -> Sketch047 [N_Axis]
  Refine = true
  Reversed = true
  Suppressed = false
  Type = 0
FEATURE [PartDesign::Pocket] Pocket016
  BaseFeature = -> Pocket015
  Direction = (-1,0,0)
  Length = 1
  Length2 = 5
  Placement = pos=(0,0,0) rot=(1,0,0;1.5708rad)
  Profile = -> Sketch046
  ReferenceAxis = -> Sketch046 [N_Axis]
  Refine = true
  Reversed = true
  Suppressed = false
  Type = 0
FEATURE [PartDesign::Pocket] Pocket017
  BaseFeature = -> Pocket016
  Direction = (0,1,-2e-16)
  Length = 17
  Length2 = 5
  Midplane = true
  Placement = pos=(0,0,0) rot=(1,0,0;1.5708rad)
  Profile = -> Sketch048
  ReferenceAxis = -> Sketch048 [N_Axis]
  Refine = true
  Suppressed = false
  Type = 0
FEATURE [PartDesign::Pad] Pad025
  BaseFeature = -> Pocket017
  Direction = (0,-1,2e-16)
  Length = 17
  Length2 = 10
  Midplane = true
  Placement = pos=(0,0,0) rot=(1,0,0;1.5708rad)
  Profile = -> Sketch049
  ReferenceAxis = -> Sketch049 [N_Axis]
  Refine = true
  Suppressed = false
  Type = 0
FEATURE [PartDesign::Pad] Pad026
  BaseFeature = -> Pad025
  Direction = (0,-1,2e-16)
  Length = 17
  Length2 = 10
  Midplane = true
  Placement = pos=(0,0,0) rot=(1,0,0;1.5708rad)
  Profile = -> Sketch066
  ReferenceAxis = -> Sketch066 [N_Axis]
  Refine = true
  Suppressed = false
  Type = 0
FEATURE [PartDesign::Pad] Pad027
  BaseFeature = -> Pad026
  Direction = (0,-1,2e-16)
  Length = 5
  Length2 = 10
  Midplane = true
  Placement = pos=(0,0,0) rot=(1,0,0;1.5708rad)
  Profile = -> Sketch064
  ReferenceAxis = -> Sketch064 [N_Axis]
  Refine = true
  Suppressed = false
  Type = 0
FEATURE [PartDesign::Pad] Pad028
  BaseFeature = -> Pad027
  Direction = (1,0,0)
  Length = 1
  Length2 = 10
  Placement = pos=(0,0,0) rot=(1,0,0;1.5708rad)
  Profile = -> Sketch068
  ReferenceAxis = -> Sketch068 [N_Axis]
  Refine = true
  Reversed = true
  Suppressed = false
  Type = 0
FEATURE [PartDesign::Chamfer] Chamfer020
  Angle = 45
  Base = -> Pad028 [Edge73,Edge75,Edge78,Edge77]
  BaseFeature = -> Pad028
  ChamferType = 0
  FlipDirection = false
  Placement = pos=(0,0,0) rot=(1,0,0;1.5708rad)
  Refine = true
  Size = 0.5
  Size2 = 1
  SupportTransform = false
  Suppressed = false
  UseAllEdges = false
FEATURE [PartDesign::Body] Body002  label="supporto per neopixel"
  AllowCompound = false
  Group = -> [Sketch045,Sketch047,Sketch046,Sketch048,Sketch049,Sketch066,Sketch064,Sketch068,Pad024,Pocket015,Pocket016,Pocket017,Pad025,Pad026,Pad027,Pad028,Chamfer020]
  Origin = -> Origin002
  Tip = -> Chamfer020
FEATURE [Sketcher::SketchObject] Sketch134  label="perno fermo rumble002"
  ArcFitTolerance = 1e-06
  AttachmentSupport = -> [XZ_Plane008]
  FullyConstrained = true
  MakeInternals = false
  MapMode = 5
  Placement = pos=(0,0,0) rot=(1,0,0;1.5708rad)
  sketch-geometry (16):
    g0: LineSegment StartX=0 StartY=0.45 StartZ=0 EndX=0 EndY=1.55 EndZ=0
    g1: LineSegment StartX=0.45 StartY=2 StartZ=0 EndX=1.55 EndY=2 EndZ=0
    g2: LineSegment StartX=2 StartY=1.55 StartZ=0 EndX=2 EndY=0.45 EndZ=0
    g3: LineSegment StartX=1.55 StartY=0 StartZ=0 EndX=0.45 EndY=0 EndZ=0
    g4: ArcOfCircle [constr] CenterX=0.45 CenterY=1.55 CenterZ=0 NormalX=0 NormalY=0 NormalZ=1 AngleXU=0 Radius=0.45 StartAngle=1.5708 EndAngle=3.14159
    g5: GeomPoint [constr] X=0 Y=2 Z=0
    g6: LineSegment StartX=0.45 StartY=2 StartZ=0 EndX=0 EndY=1.55 EndZ=0
    g7: ArcOfCircle [constr] CenterX=1.55 CenterY=1.55 CenterZ=0 NormalX=0 NormalY=0 NormalZ=1 AngleXU=0 Radius=0.45 StartAngle=0 EndAngle=1.5708
    g8: GeomPoint [constr] X=2 Y=2 Z=0
    g9: LineSegment StartX=2 StartY=1.55 StartZ=0 EndX=1.55 EndY=2 EndZ=0
    g10: ArcOfCircle [constr] CenterX=1.55 CenterY=0.45 CenterZ=0 NormalX=0 NormalY=0 NormalZ=1 AngleXU=0 Radius=0.45 StartAngle=4.71239 EndAngle=6.28319
    g11: GeomPoint [constr] X=2 Y=0 Z=0
    g12: LineSegment StartX=1.55 StartY=0 StartZ=0 EndX=2 EndY=0.45 EndZ=0
    g13: ArcOfCircle [constr] CenterX=0.45 CenterY=0.45 CenterZ=0 NormalX=0 NormalY=0 NormalZ=1 AngleXU=0 Radius=0.45 StartAngle=3.14159 EndAngle=4.71239
    g14: GeomPoint [constr] X=0 Y=0 Z=0
    g15: LineSegment StartX=0 StartY=0.45 StartZ=0 EndX=0.45 EndY=0 EndZ=0
  constraints (35):
    c: Coincident(g14,g-1)
    c: PointOnObject(g5,g-2)
    c: Horizontal(g1)
    c: Vertical(g2)
    c: Horizontal(g3)
    c: DistanceX(g5,g8) = 2
    c: DistanceY(g11,g8) = 2
    c: PointOnObject(g5,g0)
    c: PointOnObject(g5,g1)
    c: Tangent(g0,g4) = 1.5708
    c: Tangent(g1,g4) = 1.5708
    c: Coincident(g6,g0)
    c: Coincident(g6,g1)
    c: PointOnObject(g8,g2)
    c: PointOnObject(g8,g1)
    c: Tangent(g2,g7) = 1.5708
    c: Tangent(g1,g7) = 1.5708
    c: Coincident(g9,g2)
    c: Coincident(g9,g1)
    c: PointOnObject(g11,g2)
    c: PointOnObject(g11,g3)
    c: Tangent(g2,g10) = 1.5708
    c: Tangent(g3,g10) = 1.5708
    c: Coincident(g12,g2)
    c: Coincident(g12,g3)
    c: PointOnObject(g14,g0)
    c: PointOnObject(g14,g3)
    c: Tangent(g0,g13) = 1.5708
    c: Tangent(g3,g13) = 1.5708
    c: Coincident(g15,g0)
    c: Coincident(g15,g3)
    c: Equal(g6,g9)
    c: Equal(g9,g12)
    c: Equal(g12,g15)
    c: DistanceX(g14,g3) = 0.45
FEATURE [PartDesign::Pad] Pad029
  Direction = (0,-1,2e-16)
  Length = 17
  Length2 = 10
  Midplane = true
  Placement = pos=(0,0,0) rot=(1,0,0;1.5708rad)
  Profile = -> Sketch134
  ReferenceAxis = -> Sketch134 [N_Axis]
  Refine = true
  Suppressed = false
  Type = 0
FEATURE [PartDesign::Body] Body008  label="perno fermo neopixel"
  AllowCompound = false
  Group = -> [Sketch134,Pad029]
  Origin = -> Origin008
  Tip = -> Pad029
FEATURE [Sketcher::SketchObject] Sketch135  label="perno fermo rumble003"
  ArcFitTolerance = 1e-06
  AttachmentSupport = -> [XZ_Plane009]
  FullyConstrained = true
  MakeInternals = false
  MapMode = 5
  Placement = pos=(0,0,0) rot=(1,0,0;1.5708rad)
  sketch-geometry (16):
    g0: LineSegment StartX=4.69e-14 StartY=0.8 StartZ=0 EndX=-3.04e-14 EndY=3.1 EndZ=0
    g1: LineSegment StartX=0.8 StartY=3.9 StartZ=0 EndX=3.1 EndY=3.9 EndZ=0
    g2: LineSegment StartX=3.9 StartY=3.1 StartZ=0 EndX=3.9 EndY=0.8 EndZ=0
    g3: LineSegment StartX=3.1 StartY=0 StartZ=0 EndX=0.8 EndY=0 EndZ=0
    g4: ArcOfCircle [constr] CenterX=0.8 CenterY=3.1 CenterZ=0 NormalX=0 NormalY=0 NormalZ=1 AngleXU=0 Radius=0.8 StartAngle=1.5708 EndAngle=3.14159
    g5: GeomPoint [constr] X=0 Y=3.9 Z=0
    g6: LineSegment StartX=0.8 StartY=3.9 StartZ=0 EndX=-3.04e-14 EndY=3.1 EndZ=0
    g7: ArcOfCircle [constr] CenterX=3.1 CenterY=3.1 CenterZ=0 NormalX=0 NormalY=0 NormalZ=1 AngleXU=0 Radius=0.8 StartAngle=-2.4e-14 EndAngle=1.5708
    g8: GeomPoint [constr] X=3.9 Y=3.9 Z=0
    g9: LineSegment StartX=3.9 StartY=3.1 StartZ=0 EndX=3.1 EndY=3.9 EndZ=0
    g10: ArcOfCircle [constr] CenterX=3.1 CenterY=0.8 CenterZ=0 NormalX=0 NormalY=0 NormalZ=1 AngleXU=0 Radius=0.8 StartAngle=4.71239 EndAngle=6.28319
    g11: GeomPoint [constr] X=3.9 Y=0 Z=0
    g12: LineSegment StartX=3.1 StartY=0 StartZ=0 EndX=3.9 EndY=0.8 EndZ=0
    g13: ArcOfCircle [constr] CenterX=0.8 CenterY=0.8 CenterZ=0 NormalX=0 NormalY=0 NormalZ=1 AngleXU=0 Radius=0.8 StartAngle=3.14159 EndAngle=4.71239
    g14: GeomPoint [constr] X=0 Y=0 Z=0
    g15: LineSegment StartX=4.69e-14 StartY=0.8 StartZ=0 EndX=0.8 EndY=0 EndZ=0
  constraints (35):
    c: Coincident(g14,g-1)
    c: PointOnObject(g5,g-2)
    c: Horizontal(g1)
    c: Vertical(g2)
    c: Horizontal(g3)
    c: DistanceX(g5,g8) = 3.9
    c: DistanceY(g11,g8) = 3.9
    c: PointOnObject(g5,g0)
    c: PointOnObject(g5,g1)
    c: Tangent(g0,g4) = 1.5708
    c: Tangent(g1,g4) = 1.5708
    c: Coincident(g6,g0)
    c: Coincident(g6,g1)
    c: PointOnObject(g8,g2)
    c: PointOnObject(g8,g1)
    c: Tangent(g2,g7) = 1.5708
    c: Tangent(g1,g7) = 1.5708
    c: Coincident(g9,g2)
    c: Coincident(g9,g1)
    c: PointOnObject(g11,g2)
    c: PointOnObject(g11,g3)
    c: Tangent(g2,g10) = 1.5708
    c: Tangent(g3,g10) = 1.5708
    c: Coincident(g12,g2)
    c: Coincident(g12,g3)
    c: PointOnObject(g14,g0)
    c: PointOnObject(g14,g3)
    c: Tangent(g0,g13) = 1.5708
    c: Tangent(g3,g13) = 1.5708
    c: Coincident(g15,g0)
    c: Coincident(g15,g3)
    c: Equal(g6,g9)
    c: Equal(g9,g12)
    c: Equal(g12,g15)
    c: DistanceX(g14,g3) = 0.8
FEATURE [PartDesign::Pad] Pad030
  Direction = (0,-1,2e-16)
  Length = 25.2
  Length2 = 10
  Midplane = true
  Placement = pos=(0,0,0) rot=(1,0,0;1.5708rad)
  Profile = -> Sketch135
  ReferenceAxis = -> Sketch135 [N_Axis]
  Refine = true
  Suppressed = false
  Type = 0
FEATURE [PartDesign::Body] Body009  label="perno fermo switch - caricabatterie - grilletto"
  AllowCompound = false
  Group = -> [Sketch135,Pad030]
  Origin = -> Origin009
  Tip = -> Pad030
FEATURE [Sketcher::SketchObject] Sketch136  label="scavo_rele"
  ArcFitTolerance = 1e-06
  AttachmentSupport = -> [XZ_Plane]
  ExternalGeometry = -> [Sketch]
  FullyConstrained = true
  MakeInternals = false
  MapMode = 5
  Placement = pos=(0,0,0) rot=(1,0,0;1.5708rad)
  sketch-geometry (7):
    g0: LineSegment [constr] StartX=-173.013 StartY=-62.644 StartZ=0 EndX=-176.535 EndY=-73.4861 EndZ=0
    g1: LineSegment [constr] StartX=-173.013 StartY=-62.644 StartZ=0 EndX=-170.35 EndY=-63.5093 EndZ=0
    g2: LineSegment [constr] StartX=-173.013 StartY=-62.644 StartZ=0 EndX=-176.627 EndY=-61.4698 EndZ=0
    g3: LineSegment StartX=-176.627 StartY=-61.4698 StartZ=0 EndX=-170.35 EndY=-63.5093 EndZ=0
    g4: LineSegment StartX=-176.627 StartY=-61.4698 StartZ=0 EndX=-180.149 EndY=-72.3118 EndZ=0
    g5: LineSegment StartX=-170.35 StartY=-63.5093 StartZ=0 EndX=-173.872 EndY=-74.3513 EndZ=0
    g6: LineSegment StartX=-180.149 StartY=-72.3118 StartZ=0 EndX=-173.872 EndY=-74.3513 EndZ=0
  constraints (19):
    c: Tangent(g0,g-3)
    c: Distance(g0,g-3) = 89
    c: Distance(g0,g0) = 11.4
    c: Coincident(g1,g0)
    c: Coincident(g2,g0)
    c: Distance(g2) = 3.8
    c: Distance(g1) = 2.8
    c: Perpendicular(g0,g1)
    c: Perpendicular(g0,g2)
    c: Coincident(g3,g2)
    c: Coincident(g3,g1)
    c: Equal(g4,g0)
    c: Equal(g5,g0)
    c: Parallel(g4,g0)
    c: Parallel(g5,g0)
    c: Coincident(g4,g2)
    c: Coincident(g5,g1)
    c: Coincident(g6,g4)
    c: Coincident(g6,g5)
FEATURE [Part::Extrusion] Extrude076  label="Extrude076 - scavo_rele"
  Base = -> Sketch136
  Dir = (0,-1,2e-16)
  DirMode = 2
  FaceMakerClass = Part::FaceMakerBullseye
  FaceMakerMode = 3
  LengthFwd = 17.8
  LengthRev = 0
  Solid = true
  Symmetric = true
FEATURE [Sketcher::SketchObject] Sketch137  label="scavo_nuovo_driver"
  ArcFitTolerance = 1e-06
  AttachmentSupport = -> [XZ_Plane]
  ExternalGeometry = -> [Sketch]
  FullyConstrained = true
  MakeInternals = false
  MapMode = 5
  Placement = pos=(0,0,0) rot=(1,0,0;1.5708rad)
  sketch-geometry (7):
    g0: LineSegment [constr] StartX=-167.759 StartY=-46.4761 StartZ=0 EndX=-172.58 EndY=-61.3126 EndZ=0
    g1: LineSegment [constr] StartX=-167.759 StartY=-46.4761 StartZ=0 EndX=-165.477 EndY=-47.2177 EndZ=0
    g2: LineSegment [constr] StartX=-167.759 StartY=-46.4761 StartZ=0 EndX=-171.373 EndY=-45.3018 EndZ=0
    g3: LineSegment StartX=-171.373 StartY=-45.3018 StartZ=0 EndX=-165.477 EndY=-47.2177 EndZ=0
    g4: LineSegment StartX=-171.373 StartY=-45.3018 StartZ=0 EndX=-176.194 EndY=-60.1383 EndZ=0
    g5: LineSegment StartX=-165.477 StartY=-47.2177 StartZ=0 EndX=-170.297 EndY=-62.0542 EndZ=0
    g6: LineSegment StartX=-176.194 StartY=-60.1383 StartZ=0 EndX=-170.297 EndY=-62.0542 EndZ=0
  constraints (19):
    c: Distance(g0,g-3) = 72
    c: Distance(g0) = 15.6
    c: Tangent(g0,g-3)
    c: Coincident(g1,g0)
    c: Coincident(g2,g0)
    c: Distance(g1) = 2.4
    c: Distance(g2) = 3.8
    c: Perpendicular(g0,g1)
    c: Perpendicular(g0,g2)
    c: Coincident(g3,g2)
    c: Coincident(g3,g1)
    c: Equal(g4,g0)
    c: Equal(g5,g0)
    c: Parallel(g4,g0)
    c: Parallel(g5,g0)
    c: Coincident(g4,g2)
    c: Coincident(g5,g1)
    c: Coincident(g6,g4)
    c: Coincident(g6,g5)
FEATURE [Part::Extrusion] Extrude077  label="Extrude077 - scavo_nuovo_driver"
  Base = -> Sketch137
  Dir = (0,-1,2e-16)
  DirMode = 2
  FaceMakerClass = Part::FaceMakerBullseye
  FaceMakerMode = 3
  LengthFwd = 20.8
  LengthRev = 0
  Solid = true
  Symmetric = true
FEATURE [Sketcher::SketchObject] Sketch138  label="scavo_nuovo_driver_alto"
  ArcFitTolerance = 1e-06
  AttachmentSupport = -> [XZ_Plane]
  ExternalGeometry = -> [Sketch]
  FullyConstrained = true
  MakeInternals = false
  MapMode = 5
  Placement = pos=(0,0,0) rot=(1,0,0;1.5708rad)
  sketch-geometry (7):
    g0: LineSegment [constr] StartX=-188.796 StartY=17.7274 StartZ=0 EndX=-187.75 EndY=4.97025 EndZ=0
    g1: LineSegment StartX=-187.75 StartY=4.97025 StartZ=0 EndX=-189.743 EndY=4.8067 EndZ=0
    g2: LineSegment StartX=-187.75 StartY=4.97025 StartZ=0 EndX=-182.766 EndY=5.37913 EndZ=0
    g3: LineSegment StartX=-190.79 StartY=17.5638 StartZ=0 EndX=-189.743 EndY=4.8067 EndZ=0
    g4: LineSegment StartX=-183.813 StartY=18.1363 StartZ=0 EndX=-182.766 EndY=5.37913 EndZ=0
    g5: LineSegment StartX=-190.79 StartY=17.5638 StartZ=0 EndX=-188.796 EndY=17.7274 EndZ=0
    g6: LineSegment StartX=-188.796 StartY=17.7274 StartZ=0 EndX=-183.813 EndY=18.1363 EndZ=0
  constraints (20):
    c: Distance(g0) = 12.8
    c: DistanceY(g-3,g0) = 9
    c: PointOnObject(g0,g-4)
    c: PointOnObject(g0,g-4)
    c: Coincident(g1,g0)
    c: Coincident(g2,g0)
    c: Distance(g1) = 2
    c: Distance(g2) = 5
    c: Perpendicular(g0,g1)
    c: Perpendicular(g0,g2)
    c: Equal(g3,g0)
    c: Parallel(g3,g0)
    c: Coincident(g3,g1)
    c: Equal(g4,g0)
    c: Parallel(g4,g0)
    c: Coincident(g4,g2)
    c: Coincident(g5,g3)
    c: Coincident(g5,g0)
    c: Coincident(g6,g0)
    c: Coincident(g6,g4)
FEATURE [Part::Extrusion] Extrude078  label="Extrude078 - scavo_nuovo_driver_alto"
  Base = -> Sketch138
  Dir = (0,-1,2e-16)
  DirMode = 2
  FaceMakerClass = Part::FaceMakerBullseye
  FaceMakerMode = 3
  LengthFwd = 16.6
  LengthRev = 0
  Solid = true
  Symmetric = true
FEATURE [Sketcher::SketchObject] Sketch139  label="fermi_nuovo_driver_alto"
  ArcFitTolerance = 1e-06
  AttachmentSupport = -> [XZ_Plane]
  ExternalGeometry = -> [Sketch138,Sketch]
  FullyConstrained = true
  MakeInternals = false
  MapMode = 5
  Placement = pos=(0,0,0) rot=(1,0,0;1.5708rad)
  sketch-geometry (17):
    g0: LineSegment [constr] StartX=-188.314 StartY=16.4295 StartZ=0 EndX=-187.885 EndY=13.7638 EndZ=0
    g1: LineSegment [constr] StartX=-187.885 StartY=13.7638 StartZ=0 EndX=-187.456 EndY=11.0981 EndZ=0
    g2: LineSegment StartX=-187.885 StartY=13.7638 StartZ=0 EndX=-187.71 EndY=12.6778 EndZ=0
    g3: LineSegment StartX=-187.885 StartY=13.7638 StartZ=0 EndX=-188.06 EndY=14.8499 EndZ=0
    g4: LineSegment StartX=-187.71 StartY=12.6778 StartZ=0 EndX=-185.538 EndY=13.0274 EndZ=0
    g5: LineSegment StartX=-188.06 StartY=14.8499 StartZ=0 EndX=-185.888 EndY=15.1994 EndZ=0
    g6: LineSegment StartX=-185.888 StartY=15.1994 StartZ=0 EndX=-185.538 EndY=13.0274 EndZ=0
    g7: LineSegment StartX=-187.456 StartY=11.0981 StartZ=0 EndX=-189.035 EndY=10.8439 EndZ=0
    g8: LineSegment StartX=-188.314 StartY=16.4295 StartZ=0 EndX=-189.893 EndY=16.1753 EndZ=0
    g9: LineSegment StartX=-189.893 StartY=16.1753 StartZ=0 EndX=-189.035 EndY=10.8439 EndZ=0
    g10: LineSegment StartX=-187.456 StartY=11.0981 StartZ=0 EndX=-185.284 EndY=11.4477 EndZ=0
    g11: LineSegment StartX=-188.314 StartY=16.4295 StartZ=0 EndX=-186.142 EndY=16.7791 EndZ=0
    g12: LineSegment StartX=-184.308 StartY=15.4537 StartZ=0 EndX=-183.958 EndY=13.2816 EndZ=0
    g13: ArcOfCircle CenterX=-185.888 CenterY=15.1994 CenterZ=0 NormalX=0 NormalY=0 NormalZ=1 AngleXU=0 Radius=1.6 StartAngle=0.15957 EndAngle=1.73037
    g14: GeomPoint [constr] X=-184.562 Y=17.0333 Z=0
    g15: ArcOfCircle CenterX=-185.538 CenterY=13.0274 CenterZ=0 NormalX=0 NormalY=0 NormalZ=1 AngleXU=0 Radius=1.6 StartAngle=4.87196 EndAngle=6.44276
    g16: GeomPoint [constr] X=-183.704 Y=11.7019 Z=0
  constraints (43):
    c: Tangent(g1,g0) = -1.5708
    c: Distance(g0) = 2.7
    c: Equal(g1,g0)
    c: Tangent(g1,g-5)
    c: Coincident(g2,g0)
    c: Coincident(g3,g0)
    c: Distance(g2) = 1.1
    c: Equal(g3,g2)
    c: PointOnObject(g3,g2)
    c: Coincident(g4,g2)
    c: Coincident(g5,g3)
    c: Distance(g4) = 2.2
    c: Equal(g4,g5)
    c: Perpendicular(g1,g4)
    c: Perpendicular(g0,g5)
    c: Coincident(g6,g5)
    c: Coincident(g6,g4)
    c: Coincident(g7,g1)
    c: Coincident(g8,g0)
    c: Distance(g7) = 1.6
    c: Equal(g7,g8)
    c: Perpendicular(g1,g7)
    c: Perpendicular(g8,g0)
    c: Coincident(g9,g8)
    c: Coincident(g9,g7)
    c: Coincident(g10,g1)
    c: Coincident(g11,g0)
    c: Distance(g10,g16) = 3.8
    c: Perpendicular(g1,g10)
    c: Perpendicular(g1,g11)
    c: DistanceY(g0,g-4) = 3.8
    c: PointOnObject(g14,g12)
    c: PointOnObject(g14,g11)
    c: Tangent(g12,g13) = 1.5708
    c: Tangent(g11,g13) = 1.5708
    c: PointOnObject(g16,g12)
    c: PointOnObject(g16,g10)
    c: Tangent(g12,g15) = 1.5708
    c: Tangent(g10,g15) = -1.5708
    c: Equal(g13,g15)
    c: Coincident(g13,g5)
    c: Parallel(g2,g0)
    c: PointOnObject(g0,g-5)
FEATURE [Part::Extrusion] Extrude079  label="Extrude079 - fermi_nuovo_driver_alto"
  Base = -> Sketch139
  Dir = (0,-1,2e-16)
  DirMode = 2
  FaceMakerClass = Part::FaceMakerBullseye
  FaceMakerMode = 3
  LengthFwd = 25.2
  LengthRev = 0
  Solid = true
  Symmetric = true
FEATURE [Sketcher::SketchObject] Sketch140  label="scavo_diodo_nuovo_driver_alto"
  ArcFitTolerance = 1e-06
  AttachmentSupport = -> [XZ_Plane]
  ExternalGeometry = -> [Sketch138]
  FullyConstrained = true
  MakeInternals = false
  MapMode = 5
  Placement = pos=(0,0,0) rot=(1,0,0;1.5708rad)
  sketch-geometry (4):
    g0: LineSegment StartX=-190.79 StartY=17.5638 StartZ=0 EndX=-189.743 EndY=4.8067 EndZ=0
    g1: LineSegment StartX=-193.78 StartY=17.3185 StartZ=0 EndX=-192.733 EndY=4.56137 EndZ=0
    g2: LineSegment StartX=-190.79 StartY=17.5638 StartZ=0 EndX=-193.78 EndY=17.3185 EndZ=0
    g3: LineSegment StartX=-192.733 StartY=4.56137 StartZ=0 EndX=-189.743 EndY=4.8067 EndZ=0
  constraints (11):
    c: Equal(g0,g-3)
    c: Parallel(g0,g-3)
    c: Equal(g1,g-3)
    c: Parallel(g1,g-3)
    c: Coincident(g2,g0)
    c: Distance(g2) = 3
    c: Perpendicular(g0,g2)
    c: Coincident(g1,g2)
    c: Coincident(g3,g1)
    c: Coincident(g3,g0)
    c: Coincident(g0,g-3)
FEATURE [Part::Extrusion] Extrude080  label="Extrude080 - scavo_diodo_nuovo_driver_alto"
  Base = -> Sketch140
  Dir = (0,-1,2e-16)
  DirMode = 2
  FaceMakerClass = Part::FaceMakerBullseye
  FaceMakerMode = 3
  LengthFwd = 4
  LengthRev = 0
  Placement = pos=(0,7.8,0) rot=(0,0,1;0rad)
  Solid = true
  Symmetric = false
FEATURE [Part::MultiFuse] Fusion001
  Refine = true
  Shapes = -> [Cut043,Extrude079]
FEATURE [Part::Cut] Cut044
  Base = -> Fusion001
  Refine = true
  Tool = -> Extrude078
FEATURE [Part::Cut] Cut045
  Base = -> Cut044
  Refine = true
  Tool = -> Extrude080
FEATURE [Sketcher::SketchObject] Sketch141  label="fermi_nuovo_driver"
  ArcFitTolerance = 1e-06
  AttachmentSupport = -> [XZ_Plane]
  ExternalGeometry = -> [Sketch,Sketch137]
  FullyConstrained = true
  MakeInternals = false
  MapMode = 5
  Placement = pos=(0,0,0) rot=(1,0,0;1.5708rad)
  sketch-geometry (16):
    g0: LineSegment [constr] StartX=-165.477 StartY=-47.2177 StartZ=0 EndX=-167.759 EndY=-46.4761 EndZ=0
    g1: LineSegment [constr] StartX=-167.759 StartY=-46.4761 StartZ=0 EndX=-168.006 EndY=-47.2369 EndZ=0
    g2: LineSegment [constr] StartX=-168.006 StartY=-47.2369 StartZ=0 EndX=-169.675 EndY=-52.3726 EndZ=0
    g3: LineSegment StartX=-169.675 StartY=-52.3726 StartZ=0 EndX=-171.767 EndY=-51.6928 EndZ=0
    g4: LineSegment StartX=-172.795 StartY=-49.6767 StartZ=0 EndX=-172.115 EndY=-47.5843 EndZ=0
    g5: LineSegment StartX=-170.099 StartY=-46.5571 StartZ=0 EndX=-166.485 EndY=-47.7313 EndZ=0
    g6: LineSegment StartX=-166.485 StartY=-47.7313 StartZ=0 EndX=-168.153 EndY=-52.867 EndZ=0
    g7: LineSegment StartX=-169.675 StartY=-52.3726 StartZ=0 EndX=-168.153 EndY=-52.867 EndZ=0
    g8: LineSegment StartX=-170.593 StartY=-48.0788 StartZ=0 EndX=-171.273 EndY=-50.1711 EndZ=0
    g9: LineSegment StartX=-171.273 StartY=-50.1711 StartZ=0 EndX=-169.181 EndY=-50.8509 EndZ=0
    g10: LineSegment StartX=-169.181 StartY=-50.8509 StartZ=0 EndX=-168.501 EndY=-48.7586 EndZ=0
    g11: LineSegment StartX=-168.501 StartY=-48.7586 StartZ=0 EndX=-170.593 EndY=-48.0788 EndZ=0
    g12: ArcOfCircle CenterX=-170.593 CenterY=-48.0788 CenterZ=0 NormalX=0 NormalY=0 NormalZ=1 AngleXU=0 Radius=1.6 StartAngle=1.25664 EndAngle=2.82743
    g13: GeomPoint [constr] X=-171.62 Y=-46.0626 Z=0
    g14: ArcOfCircle CenterX=-171.273 CenterY=-50.1711 CenterZ=0 NormalX=0 NormalY=0 NormalZ=1 AngleXU=0 Radius=1.6 StartAngle=2.82743 EndAngle=4.39823
    g15: GeomPoint [constr] X=-173.289 Y=-51.1984 Z=0
  constraints (41):
    c: Coincident(g0,g-4)
    c: PointOnObject(g0,g-3)
    c: Parallel(g0,g-4)
    c: Coincident(g1,g0)
    c: Parallel(g1,g-3)
    c: Distance(g1) = 0.8
    c: Coincident(g2,g1)
    c: Distance(g2) = 5.4
    c: Coincident(g3,g2)
    c: Parallel(g2,g-3)
    c: Distance(g15,g13) = 5.4
    c: Perpendicular(g3,g2)
    c: Parallel(g4,g2)
    c: Distance(g5,g13) = 5.4
    c: Distance(g3,g15) = 3.8
    c: Perpendicular(g4,g5)
    c: Coincident(g6,g5)
    c: Distance(g6) = 5.4
    c: Parallel(g6,g4)
    c: Coincident(g7,g2)
    c: Coincident(g7,g6)
    c: Coincident(g8,g9)
    c: Coincident(g9,g10)
    c: Coincident(g10,g11)
    c: Coincident(g11,g8)
    c: Distance(g8,g10) = 2.2
    c: Distance(g9,g11) = 2.2
    c: Perpendicular(g11,g8)
    c: Equal(g8,g10)
    c: Equal(g11,g9)
    c: Tangent(g10,g2)
    c: Distance(g10,g1) = 1.6
    c: PointOnObject(g13,g4)
    c: PointOnObject(g13,g5)
    c: Tangent(g4,g12) = 1.5708
    c: Tangent(g5,g12) = 1.5708
    c: PointOnObject(g15,g4)
    c: Tangent(g4,g14) = 1.5708
    c: Tangent(g3,g14) = 1.5708
    c: Equal(g14,g12)
    c: Coincident(g12,g8)
FEATURE [Part::Extrusion] Extrude081  label="Extrude081 - fermi_nuovo_driver"
  Base = -> Sketch141
  Dir = (0,-1,2e-16)
  DirMode = 2
  FaceMakerClass = Part::FaceMakerBullseye
  FaceMakerMode = 3
  LengthFwd = 25.2
  LengthRev = 0
  Solid = true
  Symmetric = true
FEATURE [Part::MultiFuse] Fusion002
  Refine = true
  Shapes = -> [Cut045,Extrude081]
FEATURE [Part::Cut] Cut046
  Base = -> Fusion002
  Refine = true
  Tool = -> Extrude077
FEATURE [Sketcher::SketchObject] Sketch142  label="fermi_rele"
  ArcFitTolerance = 1e-06
  AttachmentSupport = -> [XZ_Plane]
  ExternalGeometry = -> [Sketch,Sketch136]
  FullyConstrained = true
  MakeInternals = false
  MapMode = 5
  Placement = pos=(0,0,0) rot=(1,0,0;1.5708rad)
  sketch-geometry (15):
    g0: LineSegment StartX=-177.245 StartY=-63.3719 StartZ=0 EndX=-177.924 EndY=-65.4642 EndZ=0
    g1: LineSegment StartX=-175.228 StartY=-62.3446 StartZ=0 EndX=-171.614 EndY=-63.5189 EndZ=0
    g2: LineSegment StartX=-171.614 StartY=-63.5189 StartZ=0 EndX=-173.283 EndY=-68.6546 EndZ=0
    g3: LineSegment StartX=-176.897 StartY=-67.4803 StartZ=0 EndX=-173.283 EndY=-68.6546 EndZ=0
    g4: LineSegment StartX=-175.723 StartY=-63.8663 StartZ=0 EndX=-173.631 EndY=-64.5461 EndZ=0
    g5: LineSegment StartX=-175.723 StartY=-63.8663 StartZ=0 EndX=-176.403 EndY=-65.9586 EndZ=0
    g6: LineSegment StartX=-173.631 StartY=-64.5461 StartZ=0 EndX=-174.31 EndY=-66.6385 EndZ=0
    g7: LineSegment StartX=-176.403 StartY=-65.9586 StartZ=0 EndX=-174.31 EndY=-66.6385 EndZ=0
    g8: LineSegment [constr] StartX=-173.631 StartY=-64.5461 StartZ=0 EndX=-173.136 EndY=-63.0245 EndZ=0
    g9: LineSegment [constr] StartX=-173.631 StartY=-64.5461 StartZ=0 EndX=-172.109 EndY=-65.0406 EndZ=0
    g10: LineSegment [constr] StartX=-170.35 StartY=-63.5093 StartZ=0 EndX=-173.013 EndY=-62.644 EndZ=0
    g11: ArcOfCircle CenterX=-175.723 CenterY=-63.8663 CenterZ=0 NormalX=0 NormalY=0 NormalZ=1 AngleXU=0 Radius=1.6 StartAngle=1.25664 EndAngle=2.82743
    g12: GeomPoint [constr] X=-176.75 Y=-61.8502 Z=0
    g13: ArcOfCircle CenterX=-176.403 CenterY=-65.9586 CenterZ=0 NormalX=0 NormalY=0 NormalZ=1 AngleXU=0 Radius=1.6 StartAngle=2.82743 EndAngle=4.39823
    g14: GeomPoint [constr] X=-178.419 Y=-66.9859 Z=0
  constraints (39):
    c: Distance(g14,g12) = 5.4
    c: Distance(g1,g12) = 5.4
    c: Perpendicular(g1,g0)
    c: Coincident(g2,g1)
    c: Parallel(g2,g0)
    c: Coincident(g3,g2)
    c: Parallel(g2,g-3)
    c: Coincident(g5,g4)
    c: Distance(g5) = 2.2
    c: Distance(g4) = 2.2
    c: Perpendicular(g4,g5)
    c: Coincident(g6,g4)
    c: Equal(g6,g5)
    c: Parallel(g6,g5)
    c: Coincident(g7,g5)
    c: Coincident(g7,g6)
    c: Coincident(g8,g4)
    c: Coincident(g9,g4)
    c: Distance(g8) = 1.6
    c: Distance(g9) = 1.6
    c: Parallel(g8,g6)
    c: Parallel(g9,g4)
    c: PointOnObject(g8,g1)
    c: PointOnObject(g9,g2)
    c: Coincident(g10,g-4)
    c: Parallel(g10,g-4)
    c: PointOnObject(g10,g-3)
    c: Tangent(g6,g-3) = 1.5708
    c: Distance(g4,g10) = 2
    c: PointOnObject(g12,g1)
    c: Tangent(g1,g11) = 1.5708
    c: Tangent(g0,g11) = -1.5708
    c: PointOnObject(g14,g3)
    c: PointOnObject(g14,g0)
    c: Tangent(g3,g13) = -1.5708
    c: Tangent(g0,g13) = -1.5708
    c: Equal(g11,g13)
    c: Coincident(g11,g4)
    c: Parallel(g3,g1)
FEATURE [PartDesign::Body] Body  label="Struttura pistola"
  AllowCompound = false
  Group = -> [Sketch,Sketch002,Sketch004,DatumPlane,Sketch005,DatumPlane001,CopyCut,Sketch008,Sketch009,Sketch010,Sketch011,Sketch012,Sketch013,Sketch014,Sketch015,Sketch016,Sketch017,Sketch018,Sketch019,Sketch020,Sketch022,Sketch023,Sketch024,Sketch025,Sketch026,Sketch027,Sketch029,Sketch030,Sketch031,Sketch032,Sketch033,Sketch034,Sketch035,Sketch036,Sketch037,Sketch038,Sketch039,Sketch040,Sketch041,Sketch042,+22 more]
  Origin = -> Origin
FEATURE [Part::Extrusion] Extrude082  label="Extrude082 - fermi_rele"
  Base = -> Sketch142
  Dir = (0,-1,2e-16)
  DirMode = 2
  FaceMakerClass = Part::FaceMakerBullseye
  FaceMakerMode = 3
  LengthFwd = 25.2
  LengthRev = 0
  Solid = true
  Symmetric = true
FEATURE [Part::MultiFuse] Fusion003
  Refine = true
  Shapes = -> [Cut046,Extrude082]
FEATURE [Part::Cut] Cut047
  Base = -> Fusion003
  Refine = true
  Tool = -> Extrude076
note: 2 file-system paths scrubbed to <path> (originals preserved in the JSON sidecar)
